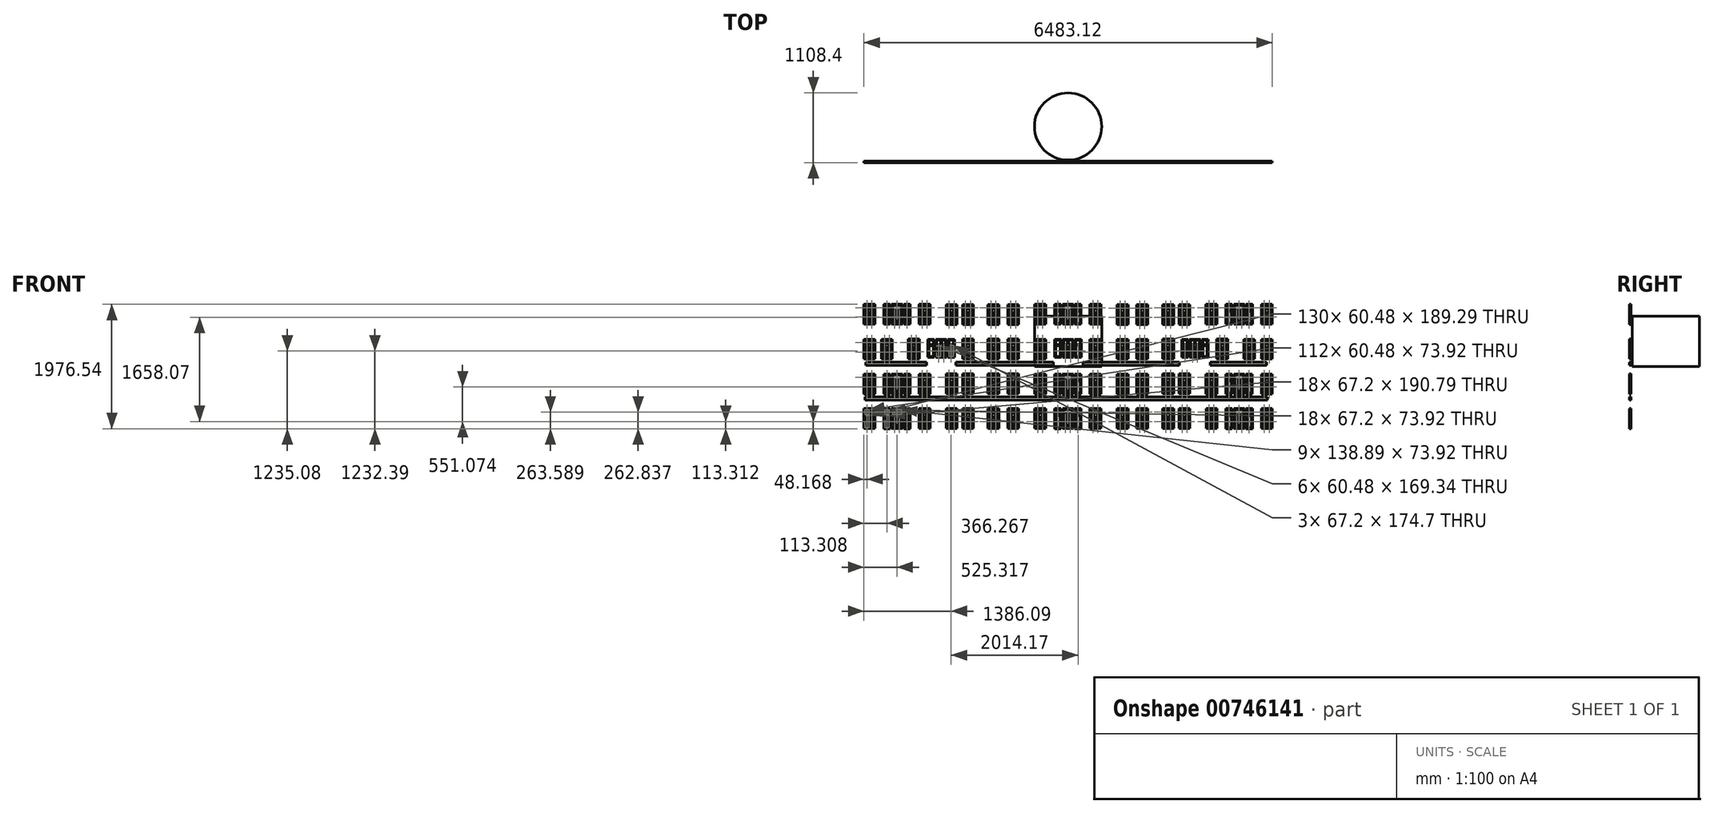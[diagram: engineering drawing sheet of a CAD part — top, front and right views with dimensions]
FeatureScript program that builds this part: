
annotation { "Feature Type Name" : "Feature", "Feature Type Description" : "" }
export const myFeature = defineFeature(function(context is Context, id is Id, definition is map)
    precondition{}
    {
        {
            var Q0;
            Q0=qCreatedBy(makeId("Top.planeOp"),FACE);
            var sketch = newSketch(context, id + "F0", { "sketchPlane" : qUnion([Q0])});
            skCircle(sketch, "E0", {"center": v(0, 0) * mm, "radius": 533.4 * mm});
            skSolve(sketch);
        }
        {
            var Q0;
            Q0 = qSketchRegion(id + "F0", true);
            extrude(context, id + "F1", {"entities" : qUnion([Q0]), "depth" : 800 * mm, "offsetDistance" : 25.4 * mm});
        }
        {
            var Q0;
            Q0=qCreatedBy(makeId("Front.planeOp"),FACE);
            cPlane(context, id + "F2", {"entities" : qUnion([Q0]), "cplaneType" : CPlaneType.OFFSET, "offset" : 50 * mm, "width" : 150 * mm, "height" : 150 * mm});
        }
        {
            var Q0;
            Q0=qCreatedBy(id+"F2.planeOp",FACE);
            cPlane(context, id + "F3", {"entities" : qUnion([Q0]), "cplaneType" : CPlaneType.OFFSET, "offset" : 500 * mm, "width" : 150 * mm, "height" : 150 * mm});
        }
        {
            var Q0;
            Q0=qCreatedBy(id+"F3.planeOp",FACE);
            var sketch = newSketch(context, id + "F4", { "sketchPlane" : qUnion([Q0])});
            skLineSegment(sketch, "E1", {"start": v(777, -987.53) * mm, "end": v(951.73, -987.53) * mm});
            skLineSegment(sketch, "E2", {"start": v(951.73, -987.53) * mm, "end": v(951.73, -670.55) * mm});
            skLineSegment(sketch, "E3", {"start": v(951.73, -670.55) * mm, "end": v(777, -670.55) * mm});
            skLineSegment(sketch, "E4", {"start": v(777, -670.55) * mm, "end": v(777, -987.53) * mm});
            skLineSegment(sketch, "E5", {"start": v(794.92, -780.32) * mm, "end": v(855.4, -780.32) * mm});
            skLineSegment(sketch, "E6", {"start": v(855.4, -780.32) * mm, "end": v(855.4, -969.6) * mm});
            skLineSegment(sketch, "E7", {"start": v(855.4, -969.6) * mm, "end": v(794.92, -969.6) * mm});
            skLineSegment(sketch, "E8", {"start": v(794.92, -969.6) * mm, "end": v(794.92, -780.32) * mm});
            skLineSegment(sketch, "E9", {"start": v(873.33, -969.6) * mm, "end": v(873.33, -780.32) * mm});
            skLineSegment(sketch, "E10", {"start": v(873.33, -780.32) * mm, "end": v(933.8, -780.32) * mm});
            skLineSegment(sketch, "E11", {"start": v(933.8, -780.32) * mm, "end": v(933.8, -969.6) * mm});
            skLineSegment(sketch, "E12", {"start": v(933.8, -969.6) * mm, "end": v(873.33, -969.6) * mm});
            skLineSegment(sketch, "E13", {"start": v(933.8, -762.4) * mm, "end": v(873.33, -762.4) * mm});
            skLineSegment(sketch, "E14", {"start": v(873.33, -762.4) * mm, "end": v(873.33, -688.47) * mm});
            skLineSegment(sketch, "E15", {"start": v(873.33, -688.47) * mm, "end": v(933.8, -688.47) * mm});
            skLineSegment(sketch, "E16", {"start": v(933.8, -688.47) * mm, "end": v(933.8, -762.4) * mm});
            skLineSegment(sketch, "E17", {"start": v(855.4, -688.47) * mm, "end": v(855.4, -762.4) * mm});
            skLineSegment(sketch, "E18", {"start": v(855.4, -762.4) * mm, "end": v(794.92, -762.4) * mm});
            skLineSegment(sketch, "E19", {"start": v(794.92, -762.4) * mm, "end": v(794.92, -688.47) * mm});
            skLineSegment(sketch, "E20", {"start": v(794.92, -688.47) * mm, "end": v(855.4, -688.47) * mm});
            skLineSegment(sketch, "E21", {"start": v(1090.62, -987.53) * mm, "end": v(1265.35, -987.53) * mm});
            skLineSegment(sketch, "E22", {"start": v(1265.35, -987.53) * mm, "end": v(1265.35, -670.55) * mm});
            skLineSegment(sketch, "E23", {"start": v(1265.35, -670.55) * mm, "end": v(1090.62, -670.55) * mm});
            skLineSegment(sketch, "E24", {"start": v(1090.62, -670.55) * mm, "end": v(1090.62, -987.53) * mm});
            skLineSegment(sketch, "E25", {"start": v(1108.54, -780.32) * mm, "end": v(1169.02, -780.32) * mm});
            skLineSegment(sketch, "E26", {"start": v(1169.02, -780.32) * mm, "end": v(1169.02, -969.6) * mm});
            skLineSegment(sketch, "E27", {"start": v(1169.02, -969.6) * mm, "end": v(1108.54, -969.6) * mm});
            skLineSegment(sketch, "E28", {"start": v(1108.54, -969.6) * mm, "end": v(1108.54, -780.32) * mm});
            skLineSegment(sketch, "E29", {"start": v(1186.95, -969.6) * mm, "end": v(1186.95, -780.32) * mm});
            skLineSegment(sketch, "E30", {"start": v(1186.95, -780.32) * mm, "end": v(1247.43, -780.32) * mm});
            skLineSegment(sketch, "E31", {"start": v(1247.43, -780.32) * mm, "end": v(1247.43, -969.6) * mm});
            skLineSegment(sketch, "E32", {"start": v(1247.43, -969.6) * mm, "end": v(1186.95, -969.6) * mm});
            skLineSegment(sketch, "E33", {"start": v(1247.43, -762.4) * mm, "end": v(1186.95, -762.4) * mm});
            skLineSegment(sketch, "E34", {"start": v(1186.95, -762.4) * mm, "end": v(1186.95, -688.47) * mm});
            skLineSegment(sketch, "E35", {"start": v(1186.95, -688.47) * mm, "end": v(1247.43, -688.47) * mm});
            skLineSegment(sketch, "E36", {"start": v(1247.43, -688.47) * mm, "end": v(1247.43, -762.4) * mm});
            skLineSegment(sketch, "E37", {"start": v(1169.02, -688.47) * mm, "end": v(1169.02, -762.4) * mm});
            skLineSegment(sketch, "E38", {"start": v(1169.02, -762.4) * mm, "end": v(1108.54, -762.4) * mm});
            skLineSegment(sketch, "E39", {"start": v(1108.54, -762.4) * mm, "end": v(1108.54, -688.47) * mm});
            skLineSegment(sketch, "E40", {"start": v(1108.54, -688.47) * mm, "end": v(1169.02, -688.47) * mm});
            skLineSegment(sketch, "E41", {"start": v(951.73, -436.46) * mm, "end": v(951.73, -119.48) * mm});
            skLineSegment(sketch, "E42", {"start": v(951.73, -119.48) * mm, "end": v(777, -119.48) * mm});
            skLineSegment(sketch, "E43", {"start": v(777, -119.48) * mm, "end": v(777, -436.46) * mm});
            skLineSegment(sketch, "E44", {"start": v(777, -436.46) * mm, "end": v(951.73, -436.46) * mm});
            skLineSegment(sketch, "E45", {"start": v(794.92, -229.24) * mm, "end": v(855.4, -229.24) * mm});
            skLineSegment(sketch, "E46", {"start": v(855.4, -229.24) * mm, "end": v(855.4, -418.53) * mm});
            skLineSegment(sketch, "E47", {"start": v(855.4, -418.53) * mm, "end": v(794.92, -418.53) * mm});
            skLineSegment(sketch, "E48", {"start": v(794.92, -418.53) * mm, "end": v(794.92, -229.24) * mm});
            skLineSegment(sketch, "E49", {"start": v(873.33, -418.53) * mm, "end": v(873.33, -229.24) * mm});
            skLineSegment(sketch, "E50", {"start": v(873.33, -229.24) * mm, "end": v(933.8, -229.24) * mm});
            skLineSegment(sketch, "E51", {"start": v(933.8, -229.24) * mm, "end": v(933.8, -418.53) * mm});
            skLineSegment(sketch, "E52", {"start": v(933.8, -418.53) * mm, "end": v(873.33, -418.53) * mm});
            skLineSegment(sketch, "E53", {"start": v(933.8, -211.32) * mm, "end": v(873.33, -211.32) * mm});
            skLineSegment(sketch, "E54", {"start": v(873.33, -211.32) * mm, "end": v(873.33, -137.4) * mm});
            skLineSegment(sketch, "E55", {"start": v(873.33, -137.4) * mm, "end": v(933.8, -137.4) * mm});
            skLineSegment(sketch, "E56", {"start": v(933.8, -137.4) * mm, "end": v(933.8, -211.32) * mm});
            skLineSegment(sketch, "E57", {"start": v(855.4, -137.4) * mm, "end": v(855.4, -211.32) * mm});
            skLineSegment(sketch, "E58", {"start": v(855.4, -211.32) * mm, "end": v(794.92, -211.32) * mm});
            skLineSegment(sketch, "E59", {"start": v(794.92, -211.32) * mm, "end": v(794.92, -137.4) * mm});
            skLineSegment(sketch, "E60", {"start": v(794.92, -137.4) * mm, "end": v(855.4, -137.4) * mm});
            skLineSegment(sketch, "E61", {"start": v(1265.35, -436.46) * mm, "end": v(1265.35, -119.48) * mm});
            skLineSegment(sketch, "E62", {"start": v(1265.35, -119.48) * mm, "end": v(1090.62, -119.48) * mm});
            skLineSegment(sketch, "E63", {"start": v(1090.62, -119.48) * mm, "end": v(1090.62, -436.46) * mm});
            skLineSegment(sketch, "E64", {"start": v(1090.62, -436.46) * mm, "end": v(1265.35, -436.46) * mm});
            skLineSegment(sketch, "E65", {"start": v(1108.54, -229.24) * mm, "end": v(1169.02, -229.24) * mm});
            skLineSegment(sketch, "E66", {"start": v(1169.02, -229.24) * mm, "end": v(1169.02, -418.53) * mm});
            skLineSegment(sketch, "E67", {"start": v(1169.02, -418.53) * mm, "end": v(1108.54, -418.53) * mm});
            skLineSegment(sketch, "E68", {"start": v(1108.54, -418.53) * mm, "end": v(1108.54, -229.24) * mm});
            skLineSegment(sketch, "E69", {"start": v(1186.95, -418.53) * mm, "end": v(1186.95, -229.24) * mm});
            skLineSegment(sketch, "E70", {"start": v(1186.95, -229.24) * mm, "end": v(1247.43, -229.24) * mm});
            skLineSegment(sketch, "E71", {"start": v(1247.43, -229.24) * mm, "end": v(1247.43, -418.53) * mm});
            skLineSegment(sketch, "E72", {"start": v(1247.43, -418.53) * mm, "end": v(1186.95, -418.53) * mm});
            skLineSegment(sketch, "E73", {"start": v(1247.43, -211.32) * mm, "end": v(1186.95, -211.32) * mm});
            skLineSegment(sketch, "E74", {"start": v(1186.95, -211.32) * mm, "end": v(1186.95, -137.4) * mm});
            skLineSegment(sketch, "E75", {"start": v(1186.95, -137.4) * mm, "end": v(1247.43, -137.4) * mm});
            skLineSegment(sketch, "E76", {"start": v(1247.43, -137.4) * mm, "end": v(1247.43, -211.32) * mm});
            skLineSegment(sketch, "E77", {"start": v(1169.02, -137.4) * mm, "end": v(1169.02, -211.32) * mm});
            skLineSegment(sketch, "E78", {"start": v(1169.02, -211.32) * mm, "end": v(1108.54, -211.32) * mm});
            skLineSegment(sketch, "E79", {"start": v(1108.54, -211.32) * mm, "end": v(1108.54, -137.4) * mm});
            skLineSegment(sketch, "E80", {"start": v(1108.54, -137.4) * mm, "end": v(1169.02, -137.4) * mm});
            skLineSegment(sketch, "E81", {"start": v(951.73, 433.84) * mm, "end": v(777, 433.84) * mm});
            skLineSegment(sketch, "E82", {"start": v(777, 433.84) * mm, "end": v(777, 116.86) * mm});
            skLineSegment(sketch, "E83", {"start": v(777, 116.86) * mm, "end": v(951.73, 116.86) * mm});
            skLineSegment(sketch, "E84", {"start": v(951.73, 116.86) * mm, "end": v(951.73, 433.84) * mm});
            skLineSegment(sketch, "E85", {"start": v(933.8, 342) * mm, "end": v(873.33, 342) * mm});
            skLineSegment(sketch, "E86", {"start": v(873.33, 342) * mm, "end": v(873.33, 415.92) * mm});
            skLineSegment(sketch, "E87", {"start": v(873.33, 415.92) * mm, "end": v(933.8, 415.92) * mm});
            skLineSegment(sketch, "E88", {"start": v(933.8, 415.92) * mm, "end": v(933.8, 342) * mm});
            skLineSegment(sketch, "E89", {"start": v(855.4, 415.92) * mm, "end": v(855.4, 342) * mm});
            skLineSegment(sketch, "E90", {"start": v(855.4, 342) * mm, "end": v(794.92, 342) * mm});
            skLineSegment(sketch, "E91", {"start": v(794.92, 342) * mm, "end": v(794.92, 415.92) * mm});
            skLineSegment(sketch, "E92", {"start": v(794.92, 415.92) * mm, "end": v(855.4, 415.92) * mm});
            skLineSegment(sketch, "E93", {"start": v(794.92, 324.07) * mm, "end": v(855.4, 324.07) * mm});
            skLineSegment(sketch, "E94", {"start": v(855.4, 324.07) * mm, "end": v(855.4, 134.78) * mm});
            skLineSegment(sketch, "E95", {"start": v(855.4, 134.78) * mm, "end": v(794.92, 134.78) * mm});
            skLineSegment(sketch, "E96", {"start": v(794.92, 134.78) * mm, "end": v(794.92, 324.07) * mm});
            skLineSegment(sketch, "E97", {"start": v(873.33, 134.78) * mm, "end": v(873.33, 324.07) * mm});
            skLineSegment(sketch, "E98", {"start": v(873.33, 324.07) * mm, "end": v(933.8, 324.07) * mm});
            skLineSegment(sketch, "E99", {"start": v(933.8, 324.07) * mm, "end": v(933.8, 134.78) * mm});
            skLineSegment(sketch, "E100", {"start": v(933.8, 134.78) * mm, "end": v(873.33, 134.78) * mm});
            skLineSegment(sketch, "E101", {"start": v(522.74, 433.84) * mm, "end": v(348.01, 433.84) * mm});
            skLineSegment(sketch, "E102", {"start": v(348.01, 433.84) * mm, "end": v(348.01, 116.86) * mm});
            skLineSegment(sketch, "E103", {"start": v(348.01, 116.86) * mm, "end": v(522.74, 116.86) * mm});
            skLineSegment(sketch, "E104", {"start": v(522.74, 116.86) * mm, "end": v(522.74, 433.84) * mm});
            skLineSegment(sketch, "E105", {"start": v(504.82, 342) * mm, "end": v(444.34, 342) * mm});
            skLineSegment(sketch, "E106", {"start": v(444.34, 342) * mm, "end": v(444.34, 415.92) * mm});
            skLineSegment(sketch, "E107", {"start": v(444.34, 415.92) * mm, "end": v(504.82, 415.92) * mm});
            skLineSegment(sketch, "E108", {"start": v(504.82, 415.92) * mm, "end": v(504.82, 342) * mm});
            skLineSegment(sketch, "E109", {"start": v(426.42, 415.92) * mm, "end": v(426.42, 342) * mm});
            skLineSegment(sketch, "E110", {"start": v(426.42, 342) * mm, "end": v(365.93, 342) * mm});
            skLineSegment(sketch, "E111", {"start": v(365.93, 342) * mm, "end": v(365.93, 415.92) * mm});
            skLineSegment(sketch, "E112", {"start": v(365.93, 415.92) * mm, "end": v(426.42, 415.92) * mm});
            skLineSegment(sketch, "E113", {"start": v(365.93, 324.07) * mm, "end": v(426.42, 324.07) * mm});
            skLineSegment(sketch, "E114", {"start": v(426.42, 324.07) * mm, "end": v(426.42, 134.78) * mm});
            skLineSegment(sketch, "E115", {"start": v(426.42, 134.78) * mm, "end": v(365.93, 134.78) * mm});
            skLineSegment(sketch, "E116", {"start": v(365.93, 134.78) * mm, "end": v(365.93, 324.07) * mm});
            skLineSegment(sketch, "E117", {"start": v(444.34, 134.78) * mm, "end": v(444.34, 324.07) * mm});
            skLineSegment(sketch, "E118", {"start": v(444.34, 324.07) * mm, "end": v(504.82, 324.07) * mm});
            skLineSegment(sketch, "E119", {"start": v(504.82, 324.07) * mm, "end": v(504.82, 134.78) * mm});
            skLineSegment(sketch, "E120", {"start": v(504.82, 134.78) * mm, "end": v(444.34, 134.78) * mm});
            skLineSegment(sketch, "E121", {"start": v(522.74, 988.27) * mm, "end": v(348.01, 988.27) * mm});
            skLineSegment(sketch, "E122", {"start": v(348.01, 988.27) * mm, "end": v(348.01, 671.3) * mm});
            skLineSegment(sketch, "E123", {"start": v(348.01, 671.3) * mm, "end": v(522.74, 671.3) * mm});
            skLineSegment(sketch, "E124", {"start": v(522.74, 671.3) * mm, "end": v(522.74, 988.27) * mm});
            skLineSegment(sketch, "E125", {"start": v(504.82, 896.43) * mm, "end": v(444.34, 896.43) * mm});
            skLineSegment(sketch, "E126", {"start": v(444.34, 896.43) * mm, "end": v(444.34, 970.35) * mm});
            skLineSegment(sketch, "E127", {"start": v(444.34, 970.35) * mm, "end": v(504.82, 970.35) * mm});
            skLineSegment(sketch, "E128", {"start": v(504.82, 970.35) * mm, "end": v(504.82, 896.43) * mm});
            skLineSegment(sketch, "E129", {"start": v(426.42, 970.35) * mm, "end": v(426.42, 896.43) * mm});
            skLineSegment(sketch, "E130", {"start": v(426.42, 896.43) * mm, "end": v(365.93, 896.43) * mm});
            skLineSegment(sketch, "E131", {"start": v(365.93, 896.43) * mm, "end": v(365.93, 970.35) * mm});
            skLineSegment(sketch, "E132", {"start": v(365.93, 970.35) * mm, "end": v(426.42, 970.35) * mm});
            skLineSegment(sketch, "E133", {"start": v(365.93, 878.5) * mm, "end": v(426.42, 878.5) * mm});
            skLineSegment(sketch, "E134", {"start": v(426.42, 878.5) * mm, "end": v(426.42, 689.21) * mm});
            skLineSegment(sketch, "E135", {"start": v(426.42, 689.21) * mm, "end": v(365.93, 689.21) * mm});
            skLineSegment(sketch, "E136", {"start": v(365.93, 689.21) * mm, "end": v(365.93, 878.5) * mm});
            skLineSegment(sketch, "E137", {"start": v(444.34, 689.21) * mm, "end": v(444.34, 878.5) * mm});
            skLineSegment(sketch, "E138", {"start": v(444.34, 878.5) * mm, "end": v(504.82, 878.5) * mm});
            skLineSegment(sketch, "E139", {"start": v(504.82, 878.5) * mm, "end": v(504.82, 689.21) * mm});
            skLineSegment(sketch, "E140", {"start": v(504.82, 689.21) * mm, "end": v(444.34, 689.21) * mm});
            skLineSegment(sketch, "E141", {"start": v(-355.39, 433.84) * mm, "end": v(-530.12, 433.84) * mm});
            skLineSegment(sketch, "E142", {"start": v(-530.12, 433.84) * mm, "end": v(-530.12, 116.86) * mm});
            skLineSegment(sketch, "E143", {"start": v(-530.12, 116.86) * mm, "end": v(-355.39, 116.86) * mm});
            skLineSegment(sketch, "E144", {"start": v(-355.39, 116.86) * mm, "end": v(-355.39, 433.84) * mm});
            skLineSegment(sketch, "E145", {"start": v(-373.3, 342) * mm, "end": v(-433.8, 342) * mm});
            skLineSegment(sketch, "E146", {"start": v(-433.8, 342) * mm, "end": v(-433.8, 415.92) * mm});
            skLineSegment(sketch, "E147", {"start": v(-433.8, 415.92) * mm, "end": v(-373.3, 415.92) * mm});
            skLineSegment(sketch, "E148", {"start": v(-373.3, 415.92) * mm, "end": v(-373.3, 342) * mm});
            skLineSegment(sketch, "E149", {"start": v(-451.71, 415.92) * mm, "end": v(-451.71, 342) * mm});
            skLineSegment(sketch, "E150", {"start": v(-451.71, 342) * mm, "end": v(-512.2, 342) * mm});
            skLineSegment(sketch, "E151", {"start": v(-512.2, 342) * mm, "end": v(-512.2, 415.92) * mm});
            skLineSegment(sketch, "E152", {"start": v(-512.2, 415.92) * mm, "end": v(-451.71, 415.92) * mm});
            skLineSegment(sketch, "E153", {"start": v(-512.2, 324.07) * mm, "end": v(-451.71, 324.07) * mm});
            skLineSegment(sketch, "E154", {"start": v(-451.71, 324.07) * mm, "end": v(-451.71, 134.78) * mm});
            skLineSegment(sketch, "E155", {"start": v(-451.71, 134.78) * mm, "end": v(-512.2, 134.78) * mm});
            skLineSegment(sketch, "E156", {"start": v(-512.2, 134.78) * mm, "end": v(-512.2, 324.07) * mm});
            skLineSegment(sketch, "E157", {"start": v(-433.8, 134.78) * mm, "end": v(-433.8, 324.07) * mm});
            skLineSegment(sketch, "E158", {"start": v(-433.8, 324.07) * mm, "end": v(-373.3, 324.07) * mm});
            skLineSegment(sketch, "E159", {"start": v(-373.3, 324.07) * mm, "end": v(-373.3, 134.78) * mm});
            skLineSegment(sketch, "E160", {"start": v(-373.3, 134.78) * mm, "end": v(-433.8, 134.78) * mm});
            skLineSegment(sketch, "E161", {"start": v(-355.39, -436.46) * mm, "end": v(-355.39, -119.48) * mm});
            skLineSegment(sketch, "E162", {"start": v(-355.39, -119.48) * mm, "end": v(-530.12, -119.48) * mm});
            skLineSegment(sketch, "E163", {"start": v(-530.12, -119.48) * mm, "end": v(-530.12, -436.46) * mm});
            skLineSegment(sketch, "E164", {"start": v(-530.12, -436.46) * mm, "end": v(-355.39, -436.46) * mm});
            skLineSegment(sketch, "E165", {"start": v(-512.2, -229.24) * mm, "end": v(-451.71, -229.24) * mm});
            skLineSegment(sketch, "E166", {"start": v(-451.71, -229.24) * mm, "end": v(-451.71, -418.53) * mm});
            skLineSegment(sketch, "E167", {"start": v(-451.71, -418.53) * mm, "end": v(-512.2, -418.53) * mm});
            skLineSegment(sketch, "E168", {"start": v(-512.2, -418.53) * mm, "end": v(-512.2, -229.24) * mm});
            skLineSegment(sketch, "E169", {"start": v(-433.8, -418.53) * mm, "end": v(-433.8, -229.24) * mm});
            skLineSegment(sketch, "E170", {"start": v(-433.8, -229.24) * mm, "end": v(-373.3, -229.24) * mm});
            skLineSegment(sketch, "E171", {"start": v(-373.3, -229.24) * mm, "end": v(-373.3, -418.53) * mm});
            skLineSegment(sketch, "E172", {"start": v(-373.3, -418.53) * mm, "end": v(-433.8, -418.53) * mm});
            skLineSegment(sketch, "E173", {"start": v(-373.3, -211.32) * mm, "end": v(-433.8, -211.32) * mm});
            skLineSegment(sketch, "E174", {"start": v(-433.8, -211.32) * mm, "end": v(-433.8, -137.4) * mm});
            skLineSegment(sketch, "E175", {"start": v(-433.8, -137.4) * mm, "end": v(-373.3, -137.4) * mm});
            skLineSegment(sketch, "E176", {"start": v(-373.3, -137.4) * mm, "end": v(-373.3, -211.32) * mm});
            skLineSegment(sketch, "E177", {"start": v(-451.71, -137.4) * mm, "end": v(-451.71, -211.32) * mm});
            skLineSegment(sketch, "E178", {"start": v(-451.71, -211.32) * mm, "end": v(-512.2, -211.32) * mm});
            skLineSegment(sketch, "E179", {"start": v(-512.2, -211.32) * mm, "end": v(-512.2, -137.4) * mm});
            skLineSegment(sketch, "E180", {"start": v(-512.2, -137.4) * mm, "end": v(-451.71, -137.4) * mm});
            skLineSegment(sketch, "E181", {"start": v(-355.39, 988.27) * mm, "end": v(-530.12, 988.27) * mm});
            skLineSegment(sketch, "E182", {"start": v(-530.12, 988.27) * mm, "end": v(-530.12, 671.3) * mm});
            skLineSegment(sketch, "E183", {"start": v(-530.12, 671.3) * mm, "end": v(-355.39, 671.3) * mm});
            skLineSegment(sketch, "E184", {"start": v(-355.39, 671.3) * mm, "end": v(-355.39, 988.27) * mm});
            skLineSegment(sketch, "E185", {"start": v(-373.3, 896.43) * mm, "end": v(-433.8, 896.43) * mm});
            skLineSegment(sketch, "E186", {"start": v(-433.8, 896.43) * mm, "end": v(-433.8, 970.35) * mm});
            skLineSegment(sketch, "E187", {"start": v(-433.8, 970.35) * mm, "end": v(-373.3, 970.35) * mm});
            skLineSegment(sketch, "E188", {"start": v(-373.3, 970.35) * mm, "end": v(-373.3, 896.43) * mm});
            skLineSegment(sketch, "E189", {"start": v(-451.71, 970.35) * mm, "end": v(-451.71, 896.43) * mm});
            skLineSegment(sketch, "E190", {"start": v(-451.71, 896.43) * mm, "end": v(-512.2, 896.43) * mm});
            skLineSegment(sketch, "E191", {"start": v(-512.2, 896.43) * mm, "end": v(-512.2, 970.35) * mm});
            skLineSegment(sketch, "E192", {"start": v(-512.2, 970.35) * mm, "end": v(-451.71, 970.35) * mm});
            skLineSegment(sketch, "E193", {"start": v(-512.2, 878.5) * mm, "end": v(-451.71, 878.5) * mm});
            skLineSegment(sketch, "E194", {"start": v(-451.71, 878.5) * mm, "end": v(-451.71, 689.21) * mm});
            skLineSegment(sketch, "E195", {"start": v(-451.71, 689.21) * mm, "end": v(-512.2, 689.21) * mm});
            skLineSegment(sketch, "E196", {"start": v(-512.2, 689.21) * mm, "end": v(-512.2, 878.5) * mm});
            skLineSegment(sketch, "E197", {"start": v(-433.8, 689.21) * mm, "end": v(-433.8, 878.5) * mm});
            skLineSegment(sketch, "E198", {"start": v(-433.8, 878.5) * mm, "end": v(-373.3, 878.5) * mm});
            skLineSegment(sketch, "E199", {"start": v(-373.3, 878.5) * mm, "end": v(-373.3, 689.21) * mm});
            skLineSegment(sketch, "E200", {"start": v(-373.3, 689.21) * mm, "end": v(-433.8, 689.21) * mm});
            skLineSegment(sketch, "E201", {"start": v(84.8, 988.27) * mm, "end": v(-89.93, 988.27) * mm});
            skLineSegment(sketch, "E202", {"start": v(-89.93, 988.27) * mm, "end": v(-89.93, 671.3) * mm});
            skLineSegment(sketch, "E203", {"start": v(-89.93, 671.3) * mm, "end": v(84.8, 671.3) * mm});
            skLineSegment(sketch, "E204", {"start": v(84.8, 671.3) * mm, "end": v(84.8, 988.27) * mm});
            skLineSegment(sketch, "E205", {"start": v(66.88, 970.35) * mm, "end": v(66.88, 896.43) * mm});
            skLineSegment(sketch, "E206", {"start": v(66.88, 896.43) * mm, "end": v(-72, 896.43) * mm});
            skLineSegment(sketch, "E207", {"start": v(-72, 896.43) * mm, "end": v(-72, 970.35) * mm});
            skLineSegment(sketch, "E208", {"start": v(-72, 970.35) * mm, "end": v(66.88, 970.35) * mm});
            skLineSegment(sketch, "E209", {"start": v(-72, 878.5) * mm, "end": v(-11.52, 878.5) * mm});
            skLineSegment(sketch, "E210", {"start": v(-11.52, 878.5) * mm, "end": v(-11.52, 689.21) * mm});
            skLineSegment(sketch, "E211", {"start": v(-11.52, 689.21) * mm, "end": v(-72, 689.21) * mm});
            skLineSegment(sketch, "E212", {"start": v(-72, 689.21) * mm, "end": v(-72, 878.5) * mm});
            skLineSegment(sketch, "E213", {"start": v(6.4, 689.21) * mm, "end": v(6.4, 878.5) * mm});
            skLineSegment(sketch, "E214", {"start": v(6.4, 878.5) * mm, "end": v(66.88, 878.5) * mm});
            skLineSegment(sketch, "E215", {"start": v(66.88, 878.5) * mm, "end": v(66.88, 689.21) * mm});
            skLineSegment(sketch, "E216", {"start": v(66.88, 689.21) * mm, "end": v(6.4, 689.21) * mm});
            skLineSegment(sketch, "E217", {"start": v(522.74, -436.46) * mm, "end": v(522.74, -119.48) * mm});
            skLineSegment(sketch, "E218", {"start": v(522.74, -119.48) * mm, "end": v(348.01, -119.48) * mm});
            skLineSegment(sketch, "E219", {"start": v(348.01, -119.48) * mm, "end": v(348.01, -436.46) * mm});
            skLineSegment(sketch, "E220", {"start": v(348.01, -436.46) * mm, "end": v(522.74, -436.46) * mm});
            skLineSegment(sketch, "E221", {"start": v(365.93, -229.24) * mm, "end": v(426.42, -229.24) * mm});
            skLineSegment(sketch, "E222", {"start": v(426.42, -229.24) * mm, "end": v(426.42, -418.53) * mm});
            skLineSegment(sketch, "E223", {"start": v(426.42, -418.53) * mm, "end": v(365.93, -418.53) * mm});
            skLineSegment(sketch, "E224", {"start": v(365.93, -418.53) * mm, "end": v(365.93, -229.24) * mm});
            skLineSegment(sketch, "E225", {"start": v(444.34, -418.53) * mm, "end": v(444.34, -229.24) * mm});
            skLineSegment(sketch, "E226", {"start": v(444.34, -229.24) * mm, "end": v(504.82, -229.24) * mm});
            skLineSegment(sketch, "E227", {"start": v(504.82, -229.24) * mm, "end": v(504.82, -418.53) * mm});
            skLineSegment(sketch, "E228", {"start": v(504.82, -418.53) * mm, "end": v(444.34, -418.53) * mm});
            skLineSegment(sketch, "E229", {"start": v(504.82, -211.32) * mm, "end": v(444.34, -211.32) * mm});
            skLineSegment(sketch, "E230", {"start": v(444.34, -211.32) * mm, "end": v(444.34, -137.4) * mm});
            skLineSegment(sketch, "E231", {"start": v(444.34, -137.4) * mm, "end": v(504.82, -137.4) * mm});
            skLineSegment(sketch, "E232", {"start": v(504.82, -137.4) * mm, "end": v(504.82, -211.32) * mm});
            skLineSegment(sketch, "E233", {"start": v(426.42, -137.4) * mm, "end": v(426.42, -211.32) * mm});
            skLineSegment(sketch, "E234", {"start": v(426.42, -211.32) * mm, "end": v(365.93, -211.32) * mm});
            skLineSegment(sketch, "E235", {"start": v(365.93, -211.32) * mm, "end": v(365.93, -137.4) * mm});
            skLineSegment(sketch, "E236", {"start": v(365.93, -137.4) * mm, "end": v(426.42, -137.4) * mm});
            skLineSegment(sketch, "E237", {"start": v(1265.35, 433.84) * mm, "end": v(1090.62, 433.84) * mm});
            skLineSegment(sketch, "E238", {"start": v(1090.62, 433.84) * mm, "end": v(1090.62, 116.86) * mm});
            skLineSegment(sketch, "E239", {"start": v(1090.62, 116.86) * mm, "end": v(1265.35, 116.86) * mm});
            skLineSegment(sketch, "E240", {"start": v(1265.35, 116.86) * mm, "end": v(1265.35, 433.84) * mm});
            skLineSegment(sketch, "E241", {"start": v(1247.43, 342) * mm, "end": v(1186.95, 342) * mm});
            skLineSegment(sketch, "E242", {"start": v(1186.95, 342) * mm, "end": v(1186.95, 415.92) * mm});
            skLineSegment(sketch, "E243", {"start": v(1186.95, 415.92) * mm, "end": v(1247.43, 415.92) * mm});
            skLineSegment(sketch, "E244", {"start": v(1247.43, 415.92) * mm, "end": v(1247.43, 342) * mm});
            skLineSegment(sketch, "E245", {"start": v(1169.02, 415.92) * mm, "end": v(1169.02, 342) * mm});
            skLineSegment(sketch, "E246", {"start": v(1169.02, 342) * mm, "end": v(1108.54, 342) * mm});
            skLineSegment(sketch, "E247", {"start": v(1108.54, 342) * mm, "end": v(1108.54, 415.92) * mm});
            skLineSegment(sketch, "E248", {"start": v(1108.54, 415.92) * mm, "end": v(1169.02, 415.92) * mm});
            skLineSegment(sketch, "E249", {"start": v(1108.54, 324.07) * mm, "end": v(1169.02, 324.07) * mm});
            skLineSegment(sketch, "E250", {"start": v(1169.02, 324.07) * mm, "end": v(1169.02, 134.78) * mm});
            skLineSegment(sketch, "E251", {"start": v(1169.02, 134.78) * mm, "end": v(1108.54, 134.78) * mm});
            skLineSegment(sketch, "E252", {"start": v(1108.54, 134.78) * mm, "end": v(1108.54, 324.07) * mm});
            skLineSegment(sketch, "E253", {"start": v(1186.95, 134.78) * mm, "end": v(1186.95, 324.07) * mm});
            skLineSegment(sketch, "E254", {"start": v(1186.95, 324.07) * mm, "end": v(1247.43, 324.07) * mm});
            skLineSegment(sketch, "E255", {"start": v(1247.43, 324.07) * mm, "end": v(1247.43, 134.78) * mm});
            skLineSegment(sketch, "E256", {"start": v(1247.43, 134.78) * mm, "end": v(1186.95, 134.78) * mm});
            skLineSegment(sketch, "E257", {"start": v(951.73, 983.8) * mm, "end": v(777, 983.8) * mm});
            skLineSegment(sketch, "E258", {"start": v(777, 983.8) * mm, "end": v(777, 666.81) * mm});
            skLineSegment(sketch, "E259", {"start": v(777, 666.81) * mm, "end": v(951.73, 666.81) * mm});
            skLineSegment(sketch, "E260", {"start": v(951.73, 666.81) * mm, "end": v(951.73, 983.8) * mm});
            skLineSegment(sketch, "E261", {"start": v(933.8, 891.95) * mm, "end": v(873.33, 891.95) * mm});
            skLineSegment(sketch, "E262", {"start": v(873.33, 891.95) * mm, "end": v(873.33, 965.87) * mm});
            skLineSegment(sketch, "E263", {"start": v(873.33, 965.87) * mm, "end": v(933.8, 965.87) * mm});
            skLineSegment(sketch, "E264", {"start": v(933.8, 965.87) * mm, "end": v(933.8, 891.95) * mm});
            skLineSegment(sketch, "E265", {"start": v(855.4, 965.87) * mm, "end": v(855.4, 891.95) * mm});
            skLineSegment(sketch, "E266", {"start": v(855.4, 891.95) * mm, "end": v(794.92, 891.95) * mm});
            skLineSegment(sketch, "E267", {"start": v(794.92, 891.95) * mm, "end": v(794.92, 965.87) * mm});
            skLineSegment(sketch, "E268", {"start": v(794.92, 965.87) * mm, "end": v(855.4, 965.87) * mm});
            skLineSegment(sketch, "E269", {"start": v(794.92, 874.03) * mm, "end": v(855.4, 874.03) * mm});
            skLineSegment(sketch, "E270", {"start": v(855.4, 874.03) * mm, "end": v(855.4, 684.73) * mm});
            skLineSegment(sketch, "E271", {"start": v(855.4, 684.73) * mm, "end": v(794.92, 684.73) * mm});
            skLineSegment(sketch, "E272", {"start": v(794.92, 684.73) * mm, "end": v(794.92, 874.03) * mm});
            skLineSegment(sketch, "E273", {"start": v(873.33, 684.73) * mm, "end": v(873.33, 874.03) * mm});
            skLineSegment(sketch, "E274", {"start": v(873.33, 874.03) * mm, "end": v(933.8, 874.03) * mm});
            skLineSegment(sketch, "E275", {"start": v(933.8, 874.03) * mm, "end": v(933.8, 684.73) * mm});
            skLineSegment(sketch, "E276", {"start": v(933.8, 684.73) * mm, "end": v(873.33, 684.73) * mm});
            skLineSegment(sketch, "E277", {"start": v(1265.35, 983.8) * mm, "end": v(1090.62, 983.8) * mm});
            skLineSegment(sketch, "E278", {"start": v(1090.62, 983.8) * mm, "end": v(1090.62, 666.81) * mm});
            skLineSegment(sketch, "E279", {"start": v(1090.62, 666.81) * mm, "end": v(1265.35, 666.81) * mm});
            skLineSegment(sketch, "E280", {"start": v(1265.35, 666.81) * mm, "end": v(1265.35, 983.8) * mm});
            skLineSegment(sketch, "E281", {"start": v(1247.43, 891.95) * mm, "end": v(1186.95, 891.95) * mm});
            skLineSegment(sketch, "E282", {"start": v(1186.95, 891.95) * mm, "end": v(1186.95, 965.87) * mm});
            skLineSegment(sketch, "E283", {"start": v(1186.95, 965.87) * mm, "end": v(1247.43, 965.87) * mm});
            skLineSegment(sketch, "E284", {"start": v(1247.43, 965.87) * mm, "end": v(1247.43, 891.95) * mm});
            skLineSegment(sketch, "E285", {"start": v(1169.02, 965.87) * mm, "end": v(1169.02, 891.95) * mm});
            skLineSegment(sketch, "E286", {"start": v(1169.02, 891.95) * mm, "end": v(1108.54, 891.95) * mm});
            skLineSegment(sketch, "E287", {"start": v(1108.54, 891.95) * mm, "end": v(1108.54, 965.87) * mm});
            skLineSegment(sketch, "E288", {"start": v(1108.54, 965.87) * mm, "end": v(1169.02, 965.87) * mm});
            skLineSegment(sketch, "E289", {"start": v(1108.54, 874.03) * mm, "end": v(1169.02, 874.03) * mm});
            skLineSegment(sketch, "E290", {"start": v(1169.02, 874.03) * mm, "end": v(1169.02, 684.73) * mm});
            skLineSegment(sketch, "E291", {"start": v(1169.02, 684.73) * mm, "end": v(1108.54, 684.73) * mm});
            skLineSegment(sketch, "E292", {"start": v(1108.54, 684.73) * mm, "end": v(1108.54, 874.03) * mm});
            skLineSegment(sketch, "E293", {"start": v(1186.95, 684.73) * mm, "end": v(1186.95, 874.03) * mm});
            skLineSegment(sketch, "E294", {"start": v(1186.95, 874.03) * mm, "end": v(1247.43, 874.03) * mm});
            skLineSegment(sketch, "E295", {"start": v(1247.43, 874.03) * mm, "end": v(1247.43, 684.73) * mm});
            skLineSegment(sketch, "E296", {"start": v(1247.43, 684.73) * mm, "end": v(1186.95, 684.73) * mm});
            skLineSegment(sketch, "E297", {"start": v(-1096.87, -434.78) * mm, "end": v(-1096.87, -117.8) * mm});
            skLineSegment(sketch, "E298", {"start": v(-1096.87, -117.8) * mm, "end": v(-1271.6, -117.8) * mm});
            skLineSegment(sketch, "E299", {"start": v(-1271.6, -117.8) * mm, "end": v(-1271.6, -434.78) * mm});
            skLineSegment(sketch, "E300", {"start": v(-1271.6, -434.78) * mm, "end": v(-1096.87, -434.78) * mm});
            skLineSegment(sketch, "E301", {"start": v(-1253.68, -227.56) * mm, "end": v(-1193.2, -227.56) * mm});
            skLineSegment(sketch, "E302", {"start": v(-1193.2, -227.56) * mm, "end": v(-1193.2, -416.85) * mm});
            skLineSegment(sketch, "E303", {"start": v(-1193.2, -416.85) * mm, "end": v(-1253.68, -416.85) * mm});
            skLineSegment(sketch, "E304", {"start": v(-1253.68, -416.85) * mm, "end": v(-1253.68, -227.56) * mm});
            skLineSegment(sketch, "E305", {"start": v(-1175.28, -416.85) * mm, "end": v(-1175.28, -227.56) * mm});
            skLineSegment(sketch, "E306", {"start": v(-1175.28, -227.56) * mm, "end": v(-1114.8, -227.56) * mm});
            skLineSegment(sketch, "E307", {"start": v(-1114.8, -227.56) * mm, "end": v(-1114.8, -416.85) * mm});
            skLineSegment(sketch, "E308", {"start": v(-1114.8, -416.85) * mm, "end": v(-1175.28, -416.85) * mm});
            skLineSegment(sketch, "E309", {"start": v(-1114.8, -209.64) * mm, "end": v(-1175.28, -209.64) * mm});
            skLineSegment(sketch, "E310", {"start": v(-1175.28, -209.64) * mm, "end": v(-1175.28, -135.72) * mm});
            skLineSegment(sketch, "E311", {"start": v(-1175.28, -135.72) * mm, "end": v(-1114.8, -135.72) * mm});
            skLineSegment(sketch, "E312", {"start": v(-1114.8, -135.72) * mm, "end": v(-1114.8, -209.64) * mm});
            skLineSegment(sketch, "E313", {"start": v(-1193.2, -135.72) * mm, "end": v(-1193.2, -209.64) * mm});
            skLineSegment(sketch, "E314", {"start": v(-1193.2, -209.64) * mm, "end": v(-1253.68, -209.64) * mm});
            skLineSegment(sketch, "E315", {"start": v(-1253.68, -209.64) * mm, "end": v(-1253.68, -135.72) * mm});
            skLineSegment(sketch, "E316", {"start": v(-1253.68, -135.72) * mm, "end": v(-1193.2, -135.72) * mm});
            skLineSegment(sketch, "E317", {"start": v(-783.25, -434.78) * mm, "end": v(-783.25, -117.8) * mm});
            skLineSegment(sketch, "E318", {"start": v(-783.25, -117.8) * mm, "end": v(-957.98, -117.8) * mm});
            skLineSegment(sketch, "E319", {"start": v(-957.98, -117.8) * mm, "end": v(-957.98, -434.78) * mm});
            skLineSegment(sketch, "E320", {"start": v(-957.98, -434.78) * mm, "end": v(-783.25, -434.78) * mm});
            skLineSegment(sketch, "E321", {"start": v(-940.06, -227.56) * mm, "end": v(-879.58, -227.56) * mm});
            skLineSegment(sketch, "E322", {"start": v(-879.58, -227.56) * mm, "end": v(-879.58, -416.85) * mm});
            skLineSegment(sketch, "E323", {"start": v(-879.58, -416.85) * mm, "end": v(-940.06, -416.85) * mm});
            skLineSegment(sketch, "E324", {"start": v(-940.06, -416.85) * mm, "end": v(-940.06, -227.56) * mm});
            skLineSegment(sketch, "E325", {"start": v(-861.66, -416.85) * mm, "end": v(-861.66, -227.56) * mm});
            skLineSegment(sketch, "E326", {"start": v(-861.66, -227.56) * mm, "end": v(-801.17, -227.56) * mm});
            skLineSegment(sketch, "E327", {"start": v(-801.17, -227.56) * mm, "end": v(-801.17, -416.85) * mm});
            skLineSegment(sketch, "E328", {"start": v(-801.17, -416.85) * mm, "end": v(-861.66, -416.85) * mm});
            skLineSegment(sketch, "E329", {"start": v(-801.17, -209.64) * mm, "end": v(-861.66, -209.64) * mm});
            skLineSegment(sketch, "E330", {"start": v(-861.66, -209.64) * mm, "end": v(-861.66, -135.72) * mm});
            skLineSegment(sketch, "E331", {"start": v(-861.66, -135.72) * mm, "end": v(-801.17, -135.72) * mm});
            skLineSegment(sketch, "E332", {"start": v(-801.17, -135.72) * mm, "end": v(-801.17, -209.64) * mm});
            skLineSegment(sketch, "E333", {"start": v(-879.58, -135.72) * mm, "end": v(-879.58, -209.64) * mm});
            skLineSegment(sketch, "E334", {"start": v(-879.58, -209.64) * mm, "end": v(-940.06, -209.64) * mm});
            skLineSegment(sketch, "E335", {"start": v(-940.06, -209.64) * mm, "end": v(-940.06, -135.72) * mm});
            skLineSegment(sketch, "E336", {"start": v(-940.06, -135.72) * mm, "end": v(-879.58, -135.72) * mm});
            skLineSegment(sketch, "E337", {"start": v(-1096.87, 435.52) * mm, "end": v(-1271.6, 435.52) * mm});
            skLineSegment(sketch, "E338", {"start": v(-1271.6, 435.52) * mm, "end": v(-1271.6, 118.54) * mm});
            skLineSegment(sketch, "E339", {"start": v(-1271.6, 118.54) * mm, "end": v(-1096.87, 118.54) * mm});
            skLineSegment(sketch, "E340", {"start": v(-1096.87, 118.54) * mm, "end": v(-1096.87, 435.52) * mm});
            skLineSegment(sketch, "E341", {"start": v(-1114.8, 343.67) * mm, "end": v(-1175.28, 343.67) * mm});
            skLineSegment(sketch, "E342", {"start": v(-1175.28, 343.67) * mm, "end": v(-1175.28, 417.6) * mm});
            skLineSegment(sketch, "E343", {"start": v(-1175.28, 417.6) * mm, "end": v(-1114.8, 417.6) * mm});
            skLineSegment(sketch, "E344", {"start": v(-1114.8, 417.6) * mm, "end": v(-1114.8, 343.67) * mm});
            skLineSegment(sketch, "E345", {"start": v(-1193.2, 417.6) * mm, "end": v(-1193.2, 343.67) * mm});
            skLineSegment(sketch, "E346", {"start": v(-1193.2, 343.67) * mm, "end": v(-1253.68, 343.67) * mm});
            skLineSegment(sketch, "E347", {"start": v(-1253.68, 343.67) * mm, "end": v(-1253.68, 417.6) * mm});
            skLineSegment(sketch, "E348", {"start": v(-1253.68, 417.6) * mm, "end": v(-1193.2, 417.6) * mm});
            skLineSegment(sketch, "E349", {"start": v(-1253.68, 325.75) * mm, "end": v(-1193.2, 325.75) * mm});
            skLineSegment(sketch, "E350", {"start": v(-1193.2, 325.75) * mm, "end": v(-1193.2, 136.46) * mm});
            skLineSegment(sketch, "E351", {"start": v(-1193.2, 136.46) * mm, "end": v(-1253.68, 136.46) * mm});
            skLineSegment(sketch, "E352", {"start": v(-1253.68, 136.46) * mm, "end": v(-1253.68, 325.75) * mm});
            skLineSegment(sketch, "E353", {"start": v(-1175.28, 136.46) * mm, "end": v(-1175.28, 325.75) * mm});
            skLineSegment(sketch, "E354", {"start": v(-1175.28, 325.75) * mm, "end": v(-1114.8, 325.75) * mm});
            skLineSegment(sketch, "E355", {"start": v(-1114.8, 325.75) * mm, "end": v(-1114.8, 136.46) * mm});
            skLineSegment(sketch, "E356", {"start": v(-1114.8, 136.46) * mm, "end": v(-1175.28, 136.46) * mm});
            skLineSegment(sketch, "E357", {"start": v(-783.25, 435.52) * mm, "end": v(-957.98, 435.52) * mm});
            skLineSegment(sketch, "E358", {"start": v(-957.98, 435.52) * mm, "end": v(-957.98, 118.54) * mm});
            skLineSegment(sketch, "E359", {"start": v(-957.98, 118.54) * mm, "end": v(-783.25, 118.54) * mm});
            skLineSegment(sketch, "E360", {"start": v(-783.25, 118.54) * mm, "end": v(-783.25, 435.52) * mm});
            skLineSegment(sketch, "E361", {"start": v(-801.17, 343.67) * mm, "end": v(-861.66, 343.67) * mm});
            skLineSegment(sketch, "E362", {"start": v(-861.66, 343.67) * mm, "end": v(-861.66, 417.6) * mm});
            skLineSegment(sketch, "E363", {"start": v(-861.66, 417.6) * mm, "end": v(-801.17, 417.6) * mm});
            skLineSegment(sketch, "E364", {"start": v(-801.17, 417.6) * mm, "end": v(-801.17, 343.67) * mm});
            skLineSegment(sketch, "E365", {"start": v(-879.58, 417.6) * mm, "end": v(-879.58, 343.67) * mm});
            skLineSegment(sketch, "E366", {"start": v(-879.58, 343.67) * mm, "end": v(-940.06, 343.67) * mm});
            skLineSegment(sketch, "E367", {"start": v(-940.06, 343.67) * mm, "end": v(-940.06, 417.6) * mm});
            skLineSegment(sketch, "E368", {"start": v(-940.06, 417.6) * mm, "end": v(-879.58, 417.6) * mm});
            skLineSegment(sketch, "E369", {"start": v(-940.06, 325.75) * mm, "end": v(-879.58, 325.75) * mm});
            skLineSegment(sketch, "E370", {"start": v(-879.58, 325.75) * mm, "end": v(-879.58, 136.46) * mm});
            skLineSegment(sketch, "E371", {"start": v(-879.58, 136.46) * mm, "end": v(-940.06, 136.46) * mm});
            skLineSegment(sketch, "E372", {"start": v(-940.06, 136.46) * mm, "end": v(-940.06, 325.75) * mm});
            skLineSegment(sketch, "E373", {"start": v(-861.66, 136.46) * mm, "end": v(-861.66, 325.75) * mm});
            skLineSegment(sketch, "E374", {"start": v(-861.66, 325.75) * mm, "end": v(-801.17, 325.75) * mm});
            skLineSegment(sketch, "E375", {"start": v(-801.17, 325.75) * mm, "end": v(-801.17, 136.46) * mm});
            skLineSegment(sketch, "E376", {"start": v(-801.17, 136.46) * mm, "end": v(-861.66, 136.46) * mm});
            skLineSegment(sketch, "E377", {"start": v(-1096.87, 985.47) * mm, "end": v(-1271.6, 985.47) * mm});
            skLineSegment(sketch, "E378", {"start": v(-1271.6, 985.47) * mm, "end": v(-1271.6, 668.5) * mm});
            skLineSegment(sketch, "E379", {"start": v(-1271.6, 668.5) * mm, "end": v(-1096.87, 668.5) * mm});
            skLineSegment(sketch, "E380", {"start": v(-1096.87, 668.5) * mm, "end": v(-1096.87, 985.47) * mm});
            skLineSegment(sketch, "E381", {"start": v(-1114.8, 893.63) * mm, "end": v(-1175.28, 893.63) * mm});
            skLineSegment(sketch, "E382", {"start": v(-1175.28, 893.63) * mm, "end": v(-1175.28, 967.55) * mm});
            skLineSegment(sketch, "E383", {"start": v(-1175.28, 967.55) * mm, "end": v(-1114.8, 967.55) * mm});
            skLineSegment(sketch, "E384", {"start": v(-1114.8, 967.55) * mm, "end": v(-1114.8, 893.63) * mm});
            skLineSegment(sketch, "E385", {"start": v(-1193.2, 967.55) * mm, "end": v(-1193.2, 893.63) * mm});
            skLineSegment(sketch, "E386", {"start": v(-1193.2, 893.63) * mm, "end": v(-1253.68, 893.63) * mm});
            skLineSegment(sketch, "E387", {"start": v(-1253.68, 893.63) * mm, "end": v(-1253.68, 967.55) * mm});
            skLineSegment(sketch, "E388", {"start": v(-1253.68, 967.55) * mm, "end": v(-1193.2, 967.55) * mm});
            skLineSegment(sketch, "E389", {"start": v(-1253.68, 875.7) * mm, "end": v(-1193.2, 875.7) * mm});
            skLineSegment(sketch, "E390", {"start": v(-1193.2, 875.7) * mm, "end": v(-1193.2, 686.41) * mm});
            skLineSegment(sketch, "E391", {"start": v(-1193.2, 686.41) * mm, "end": v(-1253.68, 686.41) * mm});
            skLineSegment(sketch, "E392", {"start": v(-1253.68, 686.41) * mm, "end": v(-1253.68, 875.7) * mm});
            skLineSegment(sketch, "E393", {"start": v(-1175.28, 686.41) * mm, "end": v(-1175.28, 875.7) * mm});
            skLineSegment(sketch, "E394", {"start": v(-1175.28, 875.7) * mm, "end": v(-1114.8, 875.7) * mm});
            skLineSegment(sketch, "E395", {"start": v(-1114.8, 875.7) * mm, "end": v(-1114.8, 686.41) * mm});
            skLineSegment(sketch, "E396", {"start": v(-1114.8, 686.41) * mm, "end": v(-1175.28, 686.41) * mm});
            skLineSegment(sketch, "E397", {"start": v(-783.25, 985.47) * mm, "end": v(-957.98, 985.47) * mm});
            skLineSegment(sketch, "E398", {"start": v(-957.98, 985.47) * mm, "end": v(-957.98, 668.5) * mm});
            skLineSegment(sketch, "E399", {"start": v(-957.98, 668.5) * mm, "end": v(-783.25, 668.5) * mm});
            skLineSegment(sketch, "E400", {"start": v(-783.25, 668.5) * mm, "end": v(-783.25, 985.47) * mm});
            skLineSegment(sketch, "E401", {"start": v(-801.17, 893.63) * mm, "end": v(-861.66, 893.63) * mm});
            skLineSegment(sketch, "E402", {"start": v(-861.66, 893.63) * mm, "end": v(-861.66, 967.55) * mm});
            skLineSegment(sketch, "E403", {"start": v(-861.66, 967.55) * mm, "end": v(-801.17, 967.55) * mm});
            skLineSegment(sketch, "E404", {"start": v(-801.17, 967.55) * mm, "end": v(-801.17, 893.63) * mm});
            skLineSegment(sketch, "E405", {"start": v(-879.58, 967.55) * mm, "end": v(-879.58, 893.63) * mm});
            skLineSegment(sketch, "E406", {"start": v(-879.58, 893.63) * mm, "end": v(-940.06, 893.63) * mm});
            skLineSegment(sketch, "E407", {"start": v(-940.06, 893.63) * mm, "end": v(-940.06, 967.55) * mm});
            skLineSegment(sketch, "E408", {"start": v(-940.06, 967.55) * mm, "end": v(-879.58, 967.55) * mm});
            skLineSegment(sketch, "E409", {"start": v(-940.06, 875.7) * mm, "end": v(-879.58, 875.7) * mm});
            skLineSegment(sketch, "E410", {"start": v(-879.58, 875.7) * mm, "end": v(-879.58, 686.41) * mm});
            skLineSegment(sketch, "E411", {"start": v(-879.58, 686.41) * mm, "end": v(-940.06, 686.41) * mm});
            skLineSegment(sketch, "E412", {"start": v(-940.06, 686.41) * mm, "end": v(-940.06, 875.7) * mm});
            skLineSegment(sketch, "E413", {"start": v(-861.66, 686.41) * mm, "end": v(-861.66, 875.7) * mm});
            skLineSegment(sketch, "E414", {"start": v(-861.66, 875.7) * mm, "end": v(-801.17, 875.7) * mm});
            skLineSegment(sketch, "E415", {"start": v(-801.17, 875.7) * mm, "end": v(-801.17, 686.41) * mm});
            skLineSegment(sketch, "E416", {"start": v(-801.17, 686.41) * mm, "end": v(-861.66, 686.41) * mm});
            skLineSegment(sketch, "E417", {"start": v(348.01, -987.53) * mm, "end": v(522.74, -987.53) * mm});
            skLineSegment(sketch, "E418", {"start": v(522.74, -987.53) * mm, "end": v(522.74, -670.55) * mm});
            skLineSegment(sketch, "E419", {"start": v(522.74, -670.55) * mm, "end": v(348.01, -670.55) * mm});
            skLineSegment(sketch, "E420", {"start": v(348.01, -670.55) * mm, "end": v(348.01, -987.53) * mm});
            skLineSegment(sketch, "E421", {"start": v(365.93, -780.32) * mm, "end": v(426.42, -780.32) * mm});
            skLineSegment(sketch, "E422", {"start": v(426.42, -780.32) * mm, "end": v(426.42, -969.6) * mm});
            skLineSegment(sketch, "E423", {"start": v(426.42, -969.6) * mm, "end": v(365.93, -969.6) * mm});
            skLineSegment(sketch, "E424", {"start": v(365.93, -969.6) * mm, "end": v(365.93, -780.32) * mm});
            skLineSegment(sketch, "E425", {"start": v(444.34, -969.6) * mm, "end": v(444.34, -780.32) * mm});
            skLineSegment(sketch, "E426", {"start": v(444.34, -780.32) * mm, "end": v(504.82, -780.32) * mm});
            skLineSegment(sketch, "E427", {"start": v(504.82, -780.32) * mm, "end": v(504.82, -969.6) * mm});
            skLineSegment(sketch, "E428", {"start": v(504.82, -969.6) * mm, "end": v(444.34, -969.6) * mm});
            skLineSegment(sketch, "E429", {"start": v(504.82, -762.4) * mm, "end": v(444.34, -762.4) * mm});
            skLineSegment(sketch, "E430", {"start": v(444.34, -762.4) * mm, "end": v(444.34, -688.47) * mm});
            skLineSegment(sketch, "E431", {"start": v(444.34, -688.47) * mm, "end": v(504.82, -688.47) * mm});
            skLineSegment(sketch, "E432", {"start": v(504.82, -688.47) * mm, "end": v(504.82, -762.4) * mm});
            skLineSegment(sketch, "E433", {"start": v(426.42, -688.47) * mm, "end": v(426.42, -762.4) * mm});
            skLineSegment(sketch, "E434", {"start": v(426.42, -762.4) * mm, "end": v(365.93, -762.4) * mm});
            skLineSegment(sketch, "E435", {"start": v(365.93, -762.4) * mm, "end": v(365.93, -688.47) * mm});
            skLineSegment(sketch, "E436", {"start": v(365.93, -688.47) * mm, "end": v(426.42, -688.47) * mm});
            skLineSegment(sketch, "E437", {"start": v(-529, -987.53) * mm, "end": v(-354.27, -987.53) * mm});
            skLineSegment(sketch, "E438", {"start": v(-354.27, -987.53) * mm, "end": v(-354.27, -670.55) * mm});
            skLineSegment(sketch, "E439", {"start": v(-354.27, -670.55) * mm, "end": v(-529, -670.55) * mm});
            skLineSegment(sketch, "E440", {"start": v(-529, -670.55) * mm, "end": v(-529, -987.53) * mm});
            skLineSegment(sketch, "E441", {"start": v(-511.08, -780.32) * mm, "end": v(-450.6, -780.32) * mm});
            skLineSegment(sketch, "E442", {"start": v(-450.6, -780.32) * mm, "end": v(-450.6, -969.6) * mm});
            skLineSegment(sketch, "E443", {"start": v(-450.6, -969.6) * mm, "end": v(-511.08, -969.6) * mm});
            skLineSegment(sketch, "E444", {"start": v(-511.08, -969.6) * mm, "end": v(-511.08, -780.32) * mm});
            skLineSegment(sketch, "E445", {"start": v(-432.67, -969.6) * mm, "end": v(-432.67, -780.32) * mm});
            skLineSegment(sketch, "E446", {"start": v(-432.67, -780.32) * mm, "end": v(-372.19, -780.32) * mm});
            skLineSegment(sketch, "E447", {"start": v(-372.19, -780.32) * mm, "end": v(-372.19, -969.6) * mm});
            skLineSegment(sketch, "E448", {"start": v(-372.19, -969.6) * mm, "end": v(-432.67, -969.6) * mm});
            skLineSegment(sketch, "E449", {"start": v(-372.19, -762.4) * mm, "end": v(-432.67, -762.4) * mm});
            skLineSegment(sketch, "E450", {"start": v(-432.67, -762.4) * mm, "end": v(-432.67, -688.47) * mm});
            skLineSegment(sketch, "E451", {"start": v(-432.67, -688.47) * mm, "end": v(-372.19, -688.47) * mm});
            skLineSegment(sketch, "E452", {"start": v(-372.19, -688.47) * mm, "end": v(-372.19, -762.4) * mm});
            skLineSegment(sketch, "E453", {"start": v(-450.6, -688.47) * mm, "end": v(-450.6, -762.4) * mm});
            skLineSegment(sketch, "E454", {"start": v(-450.6, -762.4) * mm, "end": v(-511.08, -762.4) * mm});
            skLineSegment(sketch, "E455", {"start": v(-511.08, -762.4) * mm, "end": v(-511.08, -688.47) * mm});
            skLineSegment(sketch, "E456", {"start": v(-511.08, -688.47) * mm, "end": v(-450.6, -688.47) * mm});
            skLineSegment(sketch, "E457", {"start": v(-957.98, -987.53) * mm, "end": v(-783.25, -987.53) * mm});
            skLineSegment(sketch, "E458", {"start": v(-783.25, -987.53) * mm, "end": v(-783.25, -670.55) * mm});
            skLineSegment(sketch, "E459", {"start": v(-783.25, -670.55) * mm, "end": v(-957.98, -670.55) * mm});
            skLineSegment(sketch, "E460", {"start": v(-957.98, -670.55) * mm, "end": v(-957.98, -987.53) * mm});
            skLineSegment(sketch, "E461", {"start": v(-940.06, -780.32) * mm, "end": v(-879.58, -780.32) * mm});
            skLineSegment(sketch, "E462", {"start": v(-879.58, -780.32) * mm, "end": v(-879.58, -969.6) * mm});
            skLineSegment(sketch, "E463", {"start": v(-879.58, -969.6) * mm, "end": v(-940.06, -969.6) * mm});
            skLineSegment(sketch, "E464", {"start": v(-940.06, -969.6) * mm, "end": v(-940.06, -780.32) * mm});
            skLineSegment(sketch, "E465", {"start": v(-861.66, -969.6) * mm, "end": v(-861.66, -780.32) * mm});
            skLineSegment(sketch, "E466", {"start": v(-861.66, -780.32) * mm, "end": v(-801.17, -780.32) * mm});
            skLineSegment(sketch, "E467", {"start": v(-801.17, -780.32) * mm, "end": v(-801.17, -969.6) * mm});
            skLineSegment(sketch, "E468", {"start": v(-801.17, -969.6) * mm, "end": v(-861.66, -969.6) * mm});
            skLineSegment(sketch, "E469", {"start": v(-801.17, -762.4) * mm, "end": v(-861.66, -762.4) * mm});
            skLineSegment(sketch, "E470", {"start": v(-861.66, -762.4) * mm, "end": v(-861.66, -688.47) * mm});
            skLineSegment(sketch, "E471", {"start": v(-861.66, -688.47) * mm, "end": v(-801.17, -688.47) * mm});
            skLineSegment(sketch, "E472", {"start": v(-801.17, -688.47) * mm, "end": v(-801.17, -762.4) * mm});
            skLineSegment(sketch, "E473", {"start": v(-879.58, -688.47) * mm, "end": v(-879.58, -762.4) * mm});
            skLineSegment(sketch, "E474", {"start": v(-879.58, -762.4) * mm, "end": v(-940.06, -762.4) * mm});
            skLineSegment(sketch, "E475", {"start": v(-940.06, -762.4) * mm, "end": v(-940.06, -688.47) * mm});
            skLineSegment(sketch, "E476", {"start": v(-940.06, -688.47) * mm, "end": v(-879.58, -688.47) * mm});
            skLineSegment(sketch, "E477", {"start": v(-1271.6, -987.53) * mm, "end": v(-1096.87, -987.53) * mm});
            skLineSegment(sketch, "E478", {"start": v(-1096.87, -987.53) * mm, "end": v(-1096.87, -670.55) * mm});
            skLineSegment(sketch, "E479", {"start": v(-1096.87, -670.55) * mm, "end": v(-1271.6, -670.55) * mm});
            skLineSegment(sketch, "E480", {"start": v(-1271.6, -670.55) * mm, "end": v(-1271.6, -987.53) * mm});
            skLineSegment(sketch, "E481", {"start": v(-1253.68, -780.32) * mm, "end": v(-1193.2, -780.32) * mm});
            skLineSegment(sketch, "E482", {"start": v(-1193.2, -780.32) * mm, "end": v(-1193.2, -969.6) * mm});
            skLineSegment(sketch, "E483", {"start": v(-1193.2, -969.6) * mm, "end": v(-1253.68, -969.6) * mm});
            skLineSegment(sketch, "E484", {"start": v(-1253.68, -969.6) * mm, "end": v(-1253.68, -780.32) * mm});
            skLineSegment(sketch, "E485", {"start": v(-1175.28, -969.6) * mm, "end": v(-1175.28, -780.32) * mm});
            skLineSegment(sketch, "E486", {"start": v(-1175.28, -780.32) * mm, "end": v(-1114.8, -780.32) * mm});
            skLineSegment(sketch, "E487", {"start": v(-1114.8, -780.32) * mm, "end": v(-1114.8, -969.6) * mm});
            skLineSegment(sketch, "E488", {"start": v(-1114.8, -969.6) * mm, "end": v(-1175.28, -969.6) * mm});
            skLineSegment(sketch, "E489", {"start": v(-1114.8, -762.4) * mm, "end": v(-1175.28, -762.4) * mm});
            skLineSegment(sketch, "E490", {"start": v(-1175.28, -762.4) * mm, "end": v(-1175.28, -688.47) * mm});
            skLineSegment(sketch, "E491", {"start": v(-1175.28, -688.47) * mm, "end": v(-1114.8, -688.47) * mm});
            skLineSegment(sketch, "E492", {"start": v(-1114.8, -688.47) * mm, "end": v(-1114.8, -762.4) * mm});
            skLineSegment(sketch, "E493", {"start": v(-1193.2, -688.47) * mm, "end": v(-1193.2, -762.4) * mm});
            skLineSegment(sketch, "E494", {"start": v(-1193.2, -762.4) * mm, "end": v(-1253.68, -762.4) * mm});
            skLineSegment(sketch, "E495", {"start": v(-1253.68, -762.4) * mm, "end": v(-1253.68, -688.47) * mm});
            skLineSegment(sketch, "E496", {"start": v(-1253.68, -688.47) * mm, "end": v(-1193.2, -688.47) * mm});
            skLineSegment(sketch, "E497", {"start": v(208, 988.27) * mm, "end": v(104.97, 988.27) * mm});
            skLineSegment(sketch, "E498", {"start": v(104.97, 988.27) * mm, "end": v(104.97, 669.8) * mm});
            skLineSegment(sketch, "E499", {"start": v(104.97, 669.8) * mm, "end": v(208, 669.8) * mm});
            skLineSegment(sketch, "E500", {"start": v(208, 669.8) * mm, "end": v(208, 988.27) * mm});
            skLineSegment(sketch, "E501", {"start": v(190.08, 970.35) * mm, "end": v(190.08, 896.43) * mm});
            skLineSegment(sketch, "E502", {"start": v(190.08, 896.43) * mm, "end": v(122.88, 896.43) * mm});
            skLineSegment(sketch, "E503", {"start": v(122.88, 896.43) * mm, "end": v(122.88, 970.35) * mm});
            skLineSegment(sketch, "E504", {"start": v(122.88, 970.35) * mm, "end": v(190.08, 970.35) * mm});
            skLineSegment(sketch, "E505", {"start": v(122.88, 687.72) * mm, "end": v(122.88, 878.5) * mm});
            skLineSegment(sketch, "E506", {"start": v(122.88, 878.5) * mm, "end": v(190.08, 878.5) * mm});
            skLineSegment(sketch, "E507", {"start": v(190.08, 878.5) * mm, "end": v(190.08, 687.72) * mm});
            skLineSegment(sketch, "E508", {"start": v(190.08, 687.72) * mm, "end": v(122.88, 687.72) * mm});
            skLineSegment(sketch, "E509", {"start": v(-110.1, 988.27) * mm, "end": v(-213.14, 988.27) * mm});
            skLineSegment(sketch, "E510", {"start": v(-213.14, 988.27) * mm, "end": v(-213.14, 669.8) * mm});
            skLineSegment(sketch, "E511", {"start": v(-213.14, 669.8) * mm, "end": v(-110.1, 669.8) * mm});
            skLineSegment(sketch, "E512", {"start": v(-110.1, 669.8) * mm, "end": v(-110.1, 988.27) * mm});
            skLineSegment(sketch, "E513", {"start": v(-128.01, 970.35) * mm, "end": v(-128.01, 896.43) * mm});
            skLineSegment(sketch, "E514", {"start": v(-128.01, 896.43) * mm, "end": v(-195.22, 896.43) * mm});
            skLineSegment(sketch, "E515", {"start": v(-195.22, 896.43) * mm, "end": v(-195.22, 970.35) * mm});
            skLineSegment(sketch, "E516", {"start": v(-195.22, 970.35) * mm, "end": v(-128.01, 970.35) * mm});
            skLineSegment(sketch, "E517", {"start": v(-195.22, 687.72) * mm, "end": v(-195.22, 878.5) * mm});
            skLineSegment(sketch, "E518", {"start": v(-195.22, 878.5) * mm, "end": v(-128.01, 878.5) * mm});
            skLineSegment(sketch, "E519", {"start": v(-128.01, 878.5) * mm, "end": v(-128.01, 687.72) * mm});
            skLineSegment(sketch, "E520", {"start": v(-128.01, 687.72) * mm, "end": v(-195.22, 687.72) * mm});
            skLineSegment(sketch, "E521", {"start": v(84.25, -118.72) * mm, "end": v(-90.49, -118.72) * mm});
            skLineSegment(sketch, "E522", {"start": v(-90.49, -118.72) * mm, "end": v(-90.49, -435.7) * mm});
            skLineSegment(sketch, "E523", {"start": v(-90.49, -435.7) * mm, "end": v(84.25, -435.7) * mm});
            skLineSegment(sketch, "E524", {"start": v(84.25, -435.7) * mm, "end": v(84.25, -118.72) * mm});
            skLineSegment(sketch, "E525", {"start": v(66.32, -136.64) * mm, "end": v(66.32, -210.57) * mm});
            skLineSegment(sketch, "E526", {"start": v(66.32, -210.57) * mm, "end": v(-72.57, -210.57) * mm});
            skLineSegment(sketch, "E527", {"start": v(-72.57, -210.57) * mm, "end": v(-72.57, -136.64) * mm});
            skLineSegment(sketch, "E528", {"start": v(-72.57, -136.64) * mm, "end": v(66.32, -136.64) * mm});
            skLineSegment(sketch, "E529", {"start": v(-72.57, -228.49) * mm, "end": v(-12.08, -228.49) * mm});
            skLineSegment(sketch, "E530", {"start": v(-12.08, -228.49) * mm, "end": v(-12.08, -417.78) * mm});
            skLineSegment(sketch, "E531", {"start": v(-12.08, -417.78) * mm, "end": v(-72.57, -417.78) * mm});
            skLineSegment(sketch, "E532", {"start": v(-72.57, -417.78) * mm, "end": v(-72.57, -228.49) * mm});
            skLineSegment(sketch, "E533", {"start": v(5.84, -417.78) * mm, "end": v(5.84, -228.49) * mm});
            skLineSegment(sketch, "E534", {"start": v(5.84, -228.49) * mm, "end": v(66.32, -228.49) * mm});
            skLineSegment(sketch, "E535", {"start": v(66.32, -228.49) * mm, "end": v(66.32, -417.78) * mm});
            skLineSegment(sketch, "E536", {"start": v(66.32, -417.78) * mm, "end": v(5.84, -417.78) * mm});
            skLineSegment(sketch, "E537", {"start": v(207.44, -118.72) * mm, "end": v(104.4, -118.72) * mm});
            skLineSegment(sketch, "E538", {"start": v(104.4, -118.72) * mm, "end": v(104.4, -437.2) * mm});
            skLineSegment(sketch, "E539", {"start": v(104.4, -437.2) * mm, "end": v(207.44, -437.2) * mm});
            skLineSegment(sketch, "E540", {"start": v(207.44, -437.2) * mm, "end": v(207.44, -118.72) * mm});
            skLineSegment(sketch, "E541", {"start": v(189.52, -136.64) * mm, "end": v(189.52, -210.57) * mm});
            skLineSegment(sketch, "E542", {"start": v(189.52, -210.57) * mm, "end": v(122.32, -210.57) * mm});
            skLineSegment(sketch, "E543", {"start": v(122.32, -210.57) * mm, "end": v(122.32, -136.64) * mm});
            skLineSegment(sketch, "E544", {"start": v(122.32, -136.64) * mm, "end": v(189.52, -136.64) * mm});
            skLineSegment(sketch, "E545", {"start": v(122.32, -419.28) * mm, "end": v(122.32, -228.49) * mm});
            skLineSegment(sketch, "E546", {"start": v(122.32, -228.49) * mm, "end": v(189.52, -228.49) * mm});
            skLineSegment(sketch, "E547", {"start": v(189.52, -228.49) * mm, "end": v(189.52, -419.28) * mm});
            skLineSegment(sketch, "E548", {"start": v(189.52, -419.28) * mm, "end": v(122.32, -419.28) * mm});
            skLineSegment(sketch, "E549", {"start": v(-110.65, -118.72) * mm, "end": v(-213.7, -118.72) * mm});
            skLineSegment(sketch, "E550", {"start": v(-213.7, -118.72) * mm, "end": v(-213.7, -437.2) * mm});
            skLineSegment(sketch, "E551", {"start": v(-213.7, -437.2) * mm, "end": v(-110.65, -437.2) * mm});
            skLineSegment(sketch, "E552", {"start": v(-110.65, -437.2) * mm, "end": v(-110.65, -118.72) * mm});
            skLineSegment(sketch, "E553", {"start": v(-128.57, -136.64) * mm, "end": v(-128.57, -210.57) * mm});
            skLineSegment(sketch, "E554", {"start": v(-128.57, -210.57) * mm, "end": v(-195.78, -210.57) * mm});
            skLineSegment(sketch, "E555", {"start": v(-195.78, -210.57) * mm, "end": v(-195.78, -136.64) * mm});
            skLineSegment(sketch, "E556", {"start": v(-195.78, -136.64) * mm, "end": v(-128.57, -136.64) * mm});
            skLineSegment(sketch, "E557", {"start": v(-195.78, -419.28) * mm, "end": v(-195.78, -228.49) * mm});
            skLineSegment(sketch, "E558", {"start": v(-195.78, -228.49) * mm, "end": v(-128.57, -228.49) * mm});
            skLineSegment(sketch, "E559", {"start": v(-128.57, -228.49) * mm, "end": v(-128.57, -419.28) * mm});
            skLineSegment(sketch, "E560", {"start": v(-128.57, -419.28) * mm, "end": v(-195.78, -419.28) * mm});
            skLineSegment(sketch, "E561", {"start": v(-89.93, -986.78) * mm, "end": v(84.8, -986.78) * mm});
            skLineSegment(sketch, "E562", {"start": v(84.8, -986.78) * mm, "end": v(84.8, -669.8) * mm});
            skLineSegment(sketch, "E563", {"start": v(84.8, -669.8) * mm, "end": v(-89.93, -669.8) * mm});
            skLineSegment(sketch, "E564", {"start": v(-89.93, -669.8) * mm, "end": v(-89.93, -986.78) * mm});
            skLineSegment(sketch, "E565", {"start": v(-72, -779.56) * mm, "end": v(-11.52, -779.56) * mm});
            skLineSegment(sketch, "E566", {"start": v(-11.52, -779.56) * mm, "end": v(-11.52, -968.86) * mm});
            skLineSegment(sketch, "E567", {"start": v(-11.52, -968.86) * mm, "end": v(-72, -968.86) * mm});
            skLineSegment(sketch, "E568", {"start": v(-72, -968.86) * mm, "end": v(-72, -779.56) * mm});
            skLineSegment(sketch, "E569", {"start": v(6.4, -968.86) * mm, "end": v(6.4, -779.56) * mm});
            skLineSegment(sketch, "E570", {"start": v(6.4, -779.56) * mm, "end": v(66.88, -779.56) * mm});
            skLineSegment(sketch, "E571", {"start": v(66.88, -779.56) * mm, "end": v(66.88, -968.86) * mm});
            skLineSegment(sketch, "E572", {"start": v(66.88, -968.86) * mm, "end": v(6.4, -968.86) * mm});
            skLineSegment(sketch, "E573", {"start": v(66.88, -687.72) * mm, "end": v(66.88, -761.64) * mm});
            skLineSegment(sketch, "E574", {"start": v(66.88, -761.64) * mm, "end": v(-72, -761.64) * mm});
            skLineSegment(sketch, "E575", {"start": v(-72, -761.64) * mm, "end": v(-72, -687.72) * mm});
            skLineSegment(sketch, "E576", {"start": v(-72, -687.72) * mm, "end": v(66.88, -687.72) * mm});
            skLineSegment(sketch, "E577", {"start": v(104.97, -988.27) * mm, "end": v(208, -988.27) * mm});
            skLineSegment(sketch, "E578", {"start": v(208, -988.27) * mm, "end": v(208, -669.8) * mm});
            skLineSegment(sketch, "E579", {"start": v(208, -669.8) * mm, "end": v(104.97, -669.8) * mm});
            skLineSegment(sketch, "E580", {"start": v(104.97, -669.8) * mm, "end": v(104.97, -988.27) * mm});
            skLineSegment(sketch, "E581", {"start": v(122.88, -970.35) * mm, "end": v(122.88, -779.56) * mm});
            skLineSegment(sketch, "E582", {"start": v(122.88, -779.56) * mm, "end": v(190.08, -779.56) * mm});
            skLineSegment(sketch, "E583", {"start": v(190.08, -779.56) * mm, "end": v(190.08, -970.35) * mm});
            skLineSegment(sketch, "E584", {"start": v(190.08, -970.35) * mm, "end": v(122.88, -970.35) * mm});
            skLineSegment(sketch, "E585", {"start": v(190.08, -687.72) * mm, "end": v(190.08, -761.64) * mm});
            skLineSegment(sketch, "E586", {"start": v(190.08, -761.64) * mm, "end": v(122.88, -761.64) * mm});
            skLineSegment(sketch, "E587", {"start": v(122.88, -761.64) * mm, "end": v(122.88, -687.72) * mm});
            skLineSegment(sketch, "E588", {"start": v(122.88, -687.72) * mm, "end": v(190.08, -687.72) * mm});
            skLineSegment(sketch, "E589", {"start": v(-213.14, -988.27) * mm, "end": v(-110.1, -988.27) * mm});
            skLineSegment(sketch, "E590", {"start": v(-110.1, -988.27) * mm, "end": v(-110.1, -669.8) * mm});
            skLineSegment(sketch, "E591", {"start": v(-110.1, -669.8) * mm, "end": v(-213.14, -669.8) * mm});
            skLineSegment(sketch, "E592", {"start": v(-213.14, -669.8) * mm, "end": v(-213.14, -988.27) * mm});
            skLineSegment(sketch, "E593", {"start": v(-195.22, -970.35) * mm, "end": v(-195.22, -779.56) * mm});
            skLineSegment(sketch, "E594", {"start": v(-195.22, -779.56) * mm, "end": v(-128.01, -779.56) * mm});
            skLineSegment(sketch, "E595", {"start": v(-128.01, -779.56) * mm, "end": v(-128.01, -970.35) * mm});
            skLineSegment(sketch, "E596", {"start": v(-128.01, -970.35) * mm, "end": v(-195.22, -970.35) * mm});
            skLineSegment(sketch, "E597", {"start": v(-128.01, -687.72) * mm, "end": v(-128.01, -761.64) * mm});
            skLineSegment(sketch, "E598", {"start": v(-128.01, -761.64) * mm, "end": v(-195.22, -761.64) * mm});
            skLineSegment(sketch, "E599", {"start": v(-195.22, -761.64) * mm, "end": v(-195.22, -687.72) * mm});
            skLineSegment(sketch, "E600", {"start": v(-195.22, -687.72) * mm, "end": v(-128.01, -687.72) * mm});
            skLineSegment(sketch, "E601", {"start": v(3163.15, -482.38) * mm, "end": v(1424.02, -482.38) * mm});
            skLineSegment(sketch, "E602", {"start": v(1424.02, -482.38) * mm, "end": v(1374, -482.38) * mm});
            skLineSegment(sketch, "E603", {"start": v(1374, -482.38) * mm, "end": v(1321.36, -482.38) * mm});
            skLineSegment(sketch, "E604", {"start": v(1321.36, -482.38) * mm, "end": v(-1323.31, -482.38) * mm});
            skLineSegment(sketch, "E605", {"start": v(-1323.31, -482.38) * mm, "end": v(-3221.18, -482.38) * mm});
            skLineSegment(sketch, "E606", {"start": v(-3221.18, -482.38) * mm, "end": v(-3221.18, -535.39) * mm});
            skLineSegment(sketch, "E607", {"start": v(-3221.18, -535.39) * mm, "end": v(-1323.31, -535.39) * mm});
            skLineSegment(sketch, "E608", {"start": v(-1323.31, -535.39) * mm, "end": v(1321.36, -535.39) * mm});
            skLineSegment(sketch, "E609", {"start": v(1321.36, -535.39) * mm, "end": v(1374, -535.39) * mm});
            skLineSegment(sketch, "E610", {"start": v(1374, -535.39) * mm, "end": v(1424.02, -535.39) * mm});
            skLineSegment(sketch, "E611", {"start": v(1424.02, -535.39) * mm, "end": v(3163.15, -535.39) * mm});
            skLineSegment(sketch, "E612", {"start": v(3163.15, -535.39) * mm, "end": v(3163.15, -482.38) * mm});
            skLineSegment(sketch, "E613", {"start": v(-2246.37, 70.18) * mm, "end": v(-3207.95, 70.18) * mm});
            skLineSegment(sketch, "E614", {"start": v(-3207.95, 70.18) * mm, "end": v(-3207.95, 17.17) * mm});
            skLineSegment(sketch, "E615", {"start": v(-3207.95, 17.17) * mm, "end": v(-2246.37, 17.17) * mm});
            skLineSegment(sketch, "E616", {"start": v(-2246.37, 17.17) * mm, "end": v(-2246.37, 70.18) * mm});
            skLineSegment(sketch, "E617", {"start": v(-1783.01, 17.17) * mm, "end": v(-1323.31, 17.17) * mm});
            skLineSegment(sketch, "E618", {"start": v(-1323.31, 17.17) * mm, "end": v(-235.54, 17.17) * mm});
            skLineSegment(sketch, "E619", {"start": v(-235.54, 17.17) * mm, "end": v(-235.54, 70.18) * mm});
            skLineSegment(sketch, "E620", {"start": v(-235.54, 70.18) * mm, "end": v(-1323.31, 70.18) * mm});
            skLineSegment(sketch, "E621", {"start": v(-1323.31, 70.18) * mm, "end": v(-1783.01, 70.18) * mm});
            skLineSegment(sketch, "E622", {"start": v(-1783.01, 70.18) * mm, "end": v(-1783.01, 17.17) * mm});
            skLineSegment(sketch, "E623", {"start": v(1374, 17.17) * mm, "end": v(1433.66, 17.17) * mm});
            skLineSegment(sketch, "E624", {"start": v(1433.66, 17.17) * mm, "end": v(1769.78, 17.17) * mm});
            skLineSegment(sketch, "E625", {"start": v(1769.78, 17.17) * mm, "end": v(1769.78, 70.18) * mm});
            skLineSegment(sketch, "E626", {"start": v(1769.78, 70.18) * mm, "end": v(1433.66, 70.18) * mm});
            skLineSegment(sketch, "E627", {"start": v(1433.66, 70.18) * mm, "end": v(1374, 70.18) * mm});
            skLineSegment(sketch, "E628", {"start": v(1374, 70.18) * mm, "end": v(1318.75, 70.18) * mm});
            skLineSegment(sketch, "E629", {"start": v(1318.75, 70.18) * mm, "end": v(238.92, 70.18) * mm});
            skLineSegment(sketch, "E630", {"start": v(238.92, 70.18) * mm, "end": v(238.92, 17.17) * mm});
            skLineSegment(sketch, "E631", {"start": v(238.92, 17.17) * mm, "end": v(1321.36, 17.17) * mm});
            skLineSegment(sketch, "E632", {"start": v(1321.36, 17.17) * mm, "end": v(1374, 17.17) * mm});
            skLineSegment(sketch, "E633", {"start": v(-3066.82, 433.84) * mm, "end": v(-3241.56, 433.84) * mm});
            skLineSegment(sketch, "E634", {"start": v(-3241.56, 433.84) * mm, "end": v(-3241.56, 116.86) * mm});
            skLineSegment(sketch, "E635", {"start": v(-3241.56, 116.86) * mm, "end": v(-3066.82, 116.86) * mm});
            skLineSegment(sketch, "E636", {"start": v(-3066.82, 116.86) * mm, "end": v(-3066.82, 433.84) * mm});
            skLineSegment(sketch, "E637", {"start": v(-3084.75, 342) * mm, "end": v(-3145.23, 342) * mm});
            skLineSegment(sketch, "E638", {"start": v(-3145.23, 342) * mm, "end": v(-3145.23, 415.92) * mm});
            skLineSegment(sketch, "E639", {"start": v(-3145.23, 415.92) * mm, "end": v(-3084.75, 415.92) * mm});
            skLineSegment(sketch, "E640", {"start": v(-3084.75, 415.92) * mm, "end": v(-3084.75, 342) * mm});
            skLineSegment(sketch, "E641", {"start": v(-3163.15, 415.92) * mm, "end": v(-3163.15, 342) * mm});
            skLineSegment(sketch, "E642", {"start": v(-3163.15, 342) * mm, "end": v(-3223.63, 342) * mm});
            skLineSegment(sketch, "E643", {"start": v(-3223.63, 342) * mm, "end": v(-3223.63, 415.92) * mm});
            skLineSegment(sketch, "E644", {"start": v(-3223.63, 415.92) * mm, "end": v(-3163.15, 415.92) * mm});
            skLineSegment(sketch, "E645", {"start": v(-3223.63, 324.07) * mm, "end": v(-3163.15, 324.07) * mm});
            skLineSegment(sketch, "E646", {"start": v(-3163.15, 324.07) * mm, "end": v(-3163.15, 134.78) * mm});
            skLineSegment(sketch, "E647", {"start": v(-3163.15, 134.78) * mm, "end": v(-3223.63, 134.78) * mm});
            skLineSegment(sketch, "E648", {"start": v(-3223.63, 134.78) * mm, "end": v(-3223.63, 324.07) * mm});
            skLineSegment(sketch, "E649", {"start": v(-3145.23, 134.78) * mm, "end": v(-3145.23, 324.07) * mm});
            skLineSegment(sketch, "E650", {"start": v(-3145.23, 324.07) * mm, "end": v(-3084.75, 324.07) * mm});
            skLineSegment(sketch, "E651", {"start": v(-3084.75, 324.07) * mm, "end": v(-3084.75, 134.78) * mm});
            skLineSegment(sketch, "E652", {"start": v(-3084.75, 134.78) * mm, "end": v(-3145.23, 134.78) * mm});
            skLineSegment(sketch, "E653", {"start": v(-3066.82, 988.27) * mm, "end": v(-3241.56, 988.27) * mm});
            skLineSegment(sketch, "E654", {"start": v(-3241.56, 988.27) * mm, "end": v(-3241.56, 671.3) * mm});
            skLineSegment(sketch, "E655", {"start": v(-3241.56, 671.3) * mm, "end": v(-3066.82, 671.3) * mm});
            skLineSegment(sketch, "E656", {"start": v(-3066.82, 671.3) * mm, "end": v(-3066.82, 988.27) * mm});
            skLineSegment(sketch, "E657", {"start": v(-3084.75, 896.43) * mm, "end": v(-3145.23, 896.43) * mm});
            skLineSegment(sketch, "E658", {"start": v(-3145.23, 896.43) * mm, "end": v(-3145.23, 970.35) * mm});
            skLineSegment(sketch, "E659", {"start": v(-3145.23, 970.35) * mm, "end": v(-3084.75, 970.35) * mm});
            skLineSegment(sketch, "E660", {"start": v(-3084.75, 970.35) * mm, "end": v(-3084.75, 896.43) * mm});
            skLineSegment(sketch, "E661", {"start": v(-3163.15, 970.35) * mm, "end": v(-3163.15, 896.43) * mm});
            skLineSegment(sketch, "E662", {"start": v(-3163.15, 896.43) * mm, "end": v(-3223.63, 896.43) * mm});
            skLineSegment(sketch, "E663", {"start": v(-3223.63, 896.43) * mm, "end": v(-3223.63, 970.35) * mm});
            skLineSegment(sketch, "E664", {"start": v(-3223.63, 970.35) * mm, "end": v(-3163.15, 970.35) * mm});
            skLineSegment(sketch, "E665", {"start": v(-3223.63, 878.5) * mm, "end": v(-3163.15, 878.5) * mm});
            skLineSegment(sketch, "E666", {"start": v(-3163.15, 878.5) * mm, "end": v(-3163.15, 689.21) * mm});
            skLineSegment(sketch, "E667", {"start": v(-3163.15, 689.21) * mm, "end": v(-3223.63, 689.21) * mm});
            skLineSegment(sketch, "E668", {"start": v(-3223.63, 689.21) * mm, "end": v(-3223.63, 878.5) * mm});
            skLineSegment(sketch, "E669", {"start": v(-3145.23, 689.21) * mm, "end": v(-3145.23, 878.5) * mm});
            skLineSegment(sketch, "E670", {"start": v(-3145.23, 878.5) * mm, "end": v(-3084.75, 878.5) * mm});
            skLineSegment(sketch, "E671", {"start": v(-3084.75, 878.5) * mm, "end": v(-3084.75, 689.21) * mm});
            skLineSegment(sketch, "E672", {"start": v(-3084.75, 689.21) * mm, "end": v(-3145.23, 689.21) * mm});
            skLineSegment(sketch, "E673", {"start": v(-2789.05, 433.84) * mm, "end": v(-2963.78, 433.84) * mm});
            skLineSegment(sketch, "E674", {"start": v(-2963.78, 433.84) * mm, "end": v(-2963.78, 116.86) * mm});
            skLineSegment(sketch, "E675", {"start": v(-2963.78, 116.86) * mm, "end": v(-2789.05, 116.86) * mm});
            skLineSegment(sketch, "E676", {"start": v(-2789.05, 116.86) * mm, "end": v(-2789.05, 433.84) * mm});
            skLineSegment(sketch, "E677", {"start": v(-2806.97, 342) * mm, "end": v(-2867.45, 342) * mm});
            skLineSegment(sketch, "E678", {"start": v(-2867.45, 342) * mm, "end": v(-2867.45, 415.92) * mm});
            skLineSegment(sketch, "E679", {"start": v(-2867.45, 415.92) * mm, "end": v(-2806.97, 415.92) * mm});
            skLineSegment(sketch, "E680", {"start": v(-2806.97, 415.92) * mm, "end": v(-2806.97, 342) * mm});
            skLineSegment(sketch, "E681", {"start": v(-2885.37, 415.92) * mm, "end": v(-2885.37, 342) * mm});
            skLineSegment(sketch, "E682", {"start": v(-2885.37, 342) * mm, "end": v(-2945.86, 342) * mm});
            skLineSegment(sketch, "E683", {"start": v(-2945.86, 342) * mm, "end": v(-2945.86, 415.92) * mm});
            skLineSegment(sketch, "E684", {"start": v(-2945.86, 415.92) * mm, "end": v(-2885.37, 415.92) * mm});
            skLineSegment(sketch, "E685", {"start": v(-2945.86, 324.07) * mm, "end": v(-2885.37, 324.07) * mm});
            skLineSegment(sketch, "E686", {"start": v(-2885.37, 324.07) * mm, "end": v(-2885.37, 134.78) * mm});
            skLineSegment(sketch, "E687", {"start": v(-2885.37, 134.78) * mm, "end": v(-2945.86, 134.78) * mm});
            skLineSegment(sketch, "E688", {"start": v(-2945.86, 134.78) * mm, "end": v(-2945.86, 324.07) * mm});
            skLineSegment(sketch, "E689", {"start": v(-2867.45, 134.78) * mm, "end": v(-2867.45, 324.07) * mm});
            skLineSegment(sketch, "E690", {"start": v(-2867.45, 324.07) * mm, "end": v(-2806.97, 324.07) * mm});
            skLineSegment(sketch, "E691", {"start": v(-2806.97, 324.07) * mm, "end": v(-2806.97, 134.78) * mm});
            skLineSegment(sketch, "E692", {"start": v(-2806.97, 134.78) * mm, "end": v(-2867.45, 134.78) * mm});
            skLineSegment(sketch, "E693", {"start": v(-2188.7, -119.48) * mm, "end": v(-2363.42, -119.48) * mm});
            skLineSegment(sketch, "E694", {"start": v(-2363.42, -119.48) * mm, "end": v(-2363.42, -436.46) * mm});
            skLineSegment(sketch, "E695", {"start": v(-2363.42, -436.46) * mm, "end": v(-2188.7, -436.46) * mm});
            skLineSegment(sketch, "E696", {"start": v(-2188.7, -436.46) * mm, "end": v(-2188.7, -119.48) * mm});
            skLineSegment(sketch, "E697", {"start": v(-2206.61, -211.32) * mm, "end": v(-2267.1, -211.32) * mm});
            skLineSegment(sketch, "E698", {"start": v(-2267.1, -211.32) * mm, "end": v(-2267.1, -137.4) * mm});
            skLineSegment(sketch, "E699", {"start": v(-2267.1, -137.4) * mm, "end": v(-2206.61, -137.4) * mm});
            skLineSegment(sketch, "E700", {"start": v(-2206.61, -137.4) * mm, "end": v(-2206.61, -211.32) * mm});
            skLineSegment(sketch, "E701", {"start": v(-2285.02, -137.4) * mm, "end": v(-2285.02, -211.32) * mm});
            skLineSegment(sketch, "E702", {"start": v(-2285.02, -211.32) * mm, "end": v(-2345.5, -211.32) * mm});
            skLineSegment(sketch, "E703", {"start": v(-2345.5, -211.32) * mm, "end": v(-2345.5, -137.4) * mm});
            skLineSegment(sketch, "E704", {"start": v(-2345.5, -137.4) * mm, "end": v(-2285.02, -137.4) * mm});
            skLineSegment(sketch, "E705", {"start": v(-2345.5, -229.24) * mm, "end": v(-2285.02, -229.24) * mm});
            skLineSegment(sketch, "E706", {"start": v(-2285.02, -229.24) * mm, "end": v(-2285.02, -418.53) * mm});
            skLineSegment(sketch, "E707", {"start": v(-2285.02, -418.53) * mm, "end": v(-2345.5, -418.53) * mm});
            skLineSegment(sketch, "E708", {"start": v(-2345.5, -418.53) * mm, "end": v(-2345.5, -229.24) * mm});
            skLineSegment(sketch, "E709", {"start": v(-2267.1, -418.53) * mm, "end": v(-2267.1, -229.24) * mm});
            skLineSegment(sketch, "E710", {"start": v(-2267.1, -229.24) * mm, "end": v(-2206.61, -229.24) * mm});
            skLineSegment(sketch, "E711", {"start": v(-2206.61, -229.24) * mm, "end": v(-2206.61, -418.53) * mm});
            skLineSegment(sketch, "E712", {"start": v(-2206.61, -418.53) * mm, "end": v(-2267.1, -418.53) * mm});
            skLineSegment(sketch, "E713", {"start": v(-2188.7, 988.27) * mm, "end": v(-2363.42, 988.27) * mm});
            skLineSegment(sketch, "E714", {"start": v(-2363.42, 988.27) * mm, "end": v(-2363.42, 671.3) * mm});
            skLineSegment(sketch, "E715", {"start": v(-2363.42, 671.3) * mm, "end": v(-2188.7, 671.3) * mm});
            skLineSegment(sketch, "E716", {"start": v(-2188.7, 671.3) * mm, "end": v(-2188.7, 988.27) * mm});
            skLineSegment(sketch, "E717", {"start": v(-2206.61, 896.43) * mm, "end": v(-2267.1, 896.43) * mm});
            skLineSegment(sketch, "E718", {"start": v(-2267.1, 896.43) * mm, "end": v(-2267.1, 970.35) * mm});
            skLineSegment(sketch, "E719", {"start": v(-2267.1, 970.35) * mm, "end": v(-2206.61, 970.35) * mm});
            skLineSegment(sketch, "E720", {"start": v(-2206.61, 970.35) * mm, "end": v(-2206.61, 896.43) * mm});
            skLineSegment(sketch, "E721", {"start": v(-2285.02, 970.35) * mm, "end": v(-2285.02, 896.43) * mm});
            skLineSegment(sketch, "E722", {"start": v(-2285.02, 896.43) * mm, "end": v(-2345.5, 896.43) * mm});
            skLineSegment(sketch, "E723", {"start": v(-2345.5, 896.43) * mm, "end": v(-2345.5, 970.35) * mm});
            skLineSegment(sketch, "E724", {"start": v(-2345.5, 970.35) * mm, "end": v(-2285.02, 970.35) * mm});
            skLineSegment(sketch, "E725", {"start": v(-2345.5, 878.5) * mm, "end": v(-2285.02, 878.5) * mm});
            skLineSegment(sketch, "E726", {"start": v(-2285.02, 878.5) * mm, "end": v(-2285.02, 689.21) * mm});
            skLineSegment(sketch, "E727", {"start": v(-2285.02, 689.21) * mm, "end": v(-2345.5, 689.21) * mm});
            skLineSegment(sketch, "E728", {"start": v(-2345.5, 689.21) * mm, "end": v(-2345.5, 878.5) * mm});
            skLineSegment(sketch, "E729", {"start": v(-2267.1, 689.21) * mm, "end": v(-2267.1, 878.5) * mm});
            skLineSegment(sketch, "E730", {"start": v(-2267.1, 878.5) * mm, "end": v(-2206.61, 878.5) * mm});
            skLineSegment(sketch, "E731", {"start": v(-2206.61, 878.5) * mm, "end": v(-2206.61, 689.21) * mm});
            skLineSegment(sketch, "E732", {"start": v(-2206.61, 689.21) * mm, "end": v(-2267.1, 689.21) * mm});
            skLineSegment(sketch, "E733", {"start": v(-2628.88, 988.27) * mm, "end": v(-2803.6, 988.27) * mm});
            skLineSegment(sketch, "E734", {"start": v(-2803.6, 988.27) * mm, "end": v(-2803.6, 671.3) * mm});
            skLineSegment(sketch, "E735", {"start": v(-2803.6, 671.3) * mm, "end": v(-2628.88, 671.3) * mm});
            skLineSegment(sketch, "E736", {"start": v(-2628.88, 671.3) * mm, "end": v(-2628.88, 988.27) * mm});
            skLineSegment(sketch, "E737", {"start": v(-2646.8, 970.35) * mm, "end": v(-2646.8, 896.43) * mm});
            skLineSegment(sketch, "E738", {"start": v(-2646.8, 896.43) * mm, "end": v(-2785.69, 896.43) * mm});
            skLineSegment(sketch, "E739", {"start": v(-2785.69, 896.43) * mm, "end": v(-2785.69, 970.35) * mm});
            skLineSegment(sketch, "E740", {"start": v(-2785.69, 970.35) * mm, "end": v(-2646.8, 970.35) * mm});
            skLineSegment(sketch, "E741", {"start": v(-2785.69, 878.5) * mm, "end": v(-2725.2, 878.5) * mm});
            skLineSegment(sketch, "E742", {"start": v(-2725.2, 878.5) * mm, "end": v(-2725.2, 689.21) * mm});
            skLineSegment(sketch, "E743", {"start": v(-2725.2, 689.21) * mm, "end": v(-2785.69, 689.21) * mm});
            skLineSegment(sketch, "E744", {"start": v(-2785.69, 689.21) * mm, "end": v(-2785.69, 878.5) * mm});
            skLineSegment(sketch, "E745", {"start": v(-2707.28, 689.21) * mm, "end": v(-2707.28, 878.5) * mm});
            skLineSegment(sketch, "E746", {"start": v(-2707.28, 878.5) * mm, "end": v(-2646.8, 878.5) * mm});
            skLineSegment(sketch, "E747", {"start": v(-2646.8, 878.5) * mm, "end": v(-2646.8, 689.21) * mm});
            skLineSegment(sketch, "E748", {"start": v(-2646.8, 689.21) * mm, "end": v(-2707.28, 689.21) * mm});
            skLineSegment(sketch, "E749", {"start": v(-3066.82, -119.48) * mm, "end": v(-3241.56, -119.48) * mm});
            skLineSegment(sketch, "E750", {"start": v(-3241.56, -119.48) * mm, "end": v(-3241.56, -436.46) * mm});
            skLineSegment(sketch, "E751", {"start": v(-3241.56, -436.46) * mm, "end": v(-3066.82, -436.46) * mm});
            skLineSegment(sketch, "E752", {"start": v(-3066.82, -436.46) * mm, "end": v(-3066.82, -119.48) * mm});
            skLineSegment(sketch, "E753", {"start": v(-3084.75, -211.32) * mm, "end": v(-3145.23, -211.32) * mm});
            skLineSegment(sketch, "E754", {"start": v(-3145.23, -211.32) * mm, "end": v(-3145.23, -137.4) * mm});
            skLineSegment(sketch, "E755", {"start": v(-3145.23, -137.4) * mm, "end": v(-3084.75, -137.4) * mm});
            skLineSegment(sketch, "E756", {"start": v(-3084.75, -137.4) * mm, "end": v(-3084.75, -211.32) * mm});
            skLineSegment(sketch, "E757", {"start": v(-3163.15, -137.4) * mm, "end": v(-3163.15, -211.32) * mm});
            skLineSegment(sketch, "E758", {"start": v(-3163.15, -211.32) * mm, "end": v(-3223.63, -211.32) * mm});
            skLineSegment(sketch, "E759", {"start": v(-3223.63, -211.32) * mm, "end": v(-3223.63, -137.4) * mm});
            skLineSegment(sketch, "E760", {"start": v(-3223.63, -137.4) * mm, "end": v(-3163.15, -137.4) * mm});
            skLineSegment(sketch, "E761", {"start": v(-3223.63, -229.24) * mm, "end": v(-3163.15, -229.24) * mm});
            skLineSegment(sketch, "E762", {"start": v(-3163.15, -229.24) * mm, "end": v(-3163.15, -418.53) * mm});
            skLineSegment(sketch, "E763", {"start": v(-3163.15, -418.53) * mm, "end": v(-3223.63, -418.53) * mm});
            skLineSegment(sketch, "E764", {"start": v(-3223.63, -418.53) * mm, "end": v(-3223.63, -229.24) * mm});
            skLineSegment(sketch, "E765", {"start": v(-3145.23, -418.53) * mm, "end": v(-3145.23, -229.24) * mm});
            skLineSegment(sketch, "E766", {"start": v(-3145.23, -229.24) * mm, "end": v(-3084.75, -229.24) * mm});
            skLineSegment(sketch, "E767", {"start": v(-3084.75, -229.24) * mm, "end": v(-3084.75, -418.53) * mm});
            skLineSegment(sketch, "E768", {"start": v(-3084.75, -418.53) * mm, "end": v(-3145.23, -418.53) * mm});
            skLineSegment(sketch, "E769", {"start": v(-1500.97, -434.78) * mm, "end": v(-1500.97, -117.8) * mm});
            skLineSegment(sketch, "E770", {"start": v(-1500.97, -117.8) * mm, "end": v(-1675.7, -117.8) * mm});
            skLineSegment(sketch, "E771", {"start": v(-1675.7, -117.8) * mm, "end": v(-1675.7, -434.78) * mm});
            skLineSegment(sketch, "E772", {"start": v(-1675.7, -434.78) * mm, "end": v(-1500.97, -434.78) * mm});
            skLineSegment(sketch, "E773", {"start": v(-1657.78, -227.56) * mm, "end": v(-1597.3, -227.56) * mm});
            skLineSegment(sketch, "E774", {"start": v(-1597.3, -227.56) * mm, "end": v(-1597.3, -416.85) * mm});
            skLineSegment(sketch, "E775", {"start": v(-1597.3, -416.85) * mm, "end": v(-1657.78, -416.85) * mm});
            skLineSegment(sketch, "E776", {"start": v(-1657.78, -416.85) * mm, "end": v(-1657.78, -227.56) * mm});
            skLineSegment(sketch, "E777", {"start": v(-1579.37, -416.85) * mm, "end": v(-1579.37, -227.56) * mm});
            skLineSegment(sketch, "E778", {"start": v(-1579.37, -227.56) * mm, "end": v(-1518.89, -227.56) * mm});
            skLineSegment(sketch, "E779", {"start": v(-1518.89, -227.56) * mm, "end": v(-1518.89, -416.85) * mm});
            skLineSegment(sketch, "E780", {"start": v(-1518.89, -416.85) * mm, "end": v(-1579.37, -416.85) * mm});
            skLineSegment(sketch, "E781", {"start": v(-1518.89, -209.64) * mm, "end": v(-1579.37, -209.64) * mm});
            skLineSegment(sketch, "E782", {"start": v(-1579.37, -209.64) * mm, "end": v(-1579.37, -135.72) * mm});
            skLineSegment(sketch, "E783", {"start": v(-1579.37, -135.72) * mm, "end": v(-1518.89, -135.72) * mm});
            skLineSegment(sketch, "E784", {"start": v(-1518.89, -135.72) * mm, "end": v(-1518.89, -209.64) * mm});
            skLineSegment(sketch, "E785", {"start": v(-1597.3, -135.72) * mm, "end": v(-1597.3, -209.64) * mm});
            skLineSegment(sketch, "E786", {"start": v(-1597.3, -209.64) * mm, "end": v(-1657.78, -209.64) * mm});
            skLineSegment(sketch, "E787", {"start": v(-1657.78, -209.64) * mm, "end": v(-1657.78, -135.72) * mm});
            skLineSegment(sketch, "E788", {"start": v(-1657.78, -135.72) * mm, "end": v(-1597.3, -135.72) * mm});
            skLineSegment(sketch, "E789", {"start": v(-1935.55, -434.78) * mm, "end": v(-1760.82, -434.78) * mm});
            skLineSegment(sketch, "E790", {"start": v(-1760.82, -434.78) * mm, "end": v(-1760.82, -117.8) * mm});
            skLineSegment(sketch, "E791", {"start": v(-1760.82, -117.8) * mm, "end": v(-1935.55, -117.8) * mm});
            skLineSegment(sketch, "E792", {"start": v(-1935.55, -117.8) * mm, "end": v(-1935.55, -434.78) * mm});
            skLineSegment(sketch, "E793", {"start": v(-1917.63, -227.56) * mm, "end": v(-1857.15, -227.56) * mm});
            skLineSegment(sketch, "E794", {"start": v(-1857.15, -227.56) * mm, "end": v(-1857.15, -416.85) * mm});
            skLineSegment(sketch, "E795", {"start": v(-1857.15, -416.85) * mm, "end": v(-1917.63, -416.85) * mm});
            skLineSegment(sketch, "E796", {"start": v(-1917.63, -416.85) * mm, "end": v(-1917.63, -227.56) * mm});
            skLineSegment(sketch, "E797", {"start": v(-1839.23, -416.85) * mm, "end": v(-1839.23, -227.56) * mm});
            skLineSegment(sketch, "E798", {"start": v(-1839.23, -227.56) * mm, "end": v(-1778.74, -227.56) * mm});
            skLineSegment(sketch, "E799", {"start": v(-1778.74, -227.56) * mm, "end": v(-1778.74, -416.85) * mm});
            skLineSegment(sketch, "E800", {"start": v(-1778.74, -416.85) * mm, "end": v(-1839.23, -416.85) * mm});
            skLineSegment(sketch, "E801", {"start": v(-1778.74, -209.64) * mm, "end": v(-1839.23, -209.64) * mm});
            skLineSegment(sketch, "E802", {"start": v(-1839.23, -209.64) * mm, "end": v(-1839.23, -135.72) * mm});
            skLineSegment(sketch, "E803", {"start": v(-1839.23, -135.72) * mm, "end": v(-1778.74, -135.72) * mm});
            skLineSegment(sketch, "E804", {"start": v(-1778.74, -135.72) * mm, "end": v(-1778.74, -209.64) * mm});
            skLineSegment(sketch, "E805", {"start": v(-1857.15, -135.72) * mm, "end": v(-1857.15, -209.64) * mm});
            skLineSegment(sketch, "E806", {"start": v(-1857.15, -209.64) * mm, "end": v(-1917.63, -209.64) * mm});
            skLineSegment(sketch, "E807", {"start": v(-1917.63, -209.64) * mm, "end": v(-1917.63, -135.72) * mm});
            skLineSegment(sketch, "E808", {"start": v(-1917.63, -135.72) * mm, "end": v(-1857.15, -135.72) * mm});
            skLineSegment(sketch, "E809", {"start": v(-1500.97, 435.52) * mm, "end": v(-1675.7, 435.52) * mm});
            skLineSegment(sketch, "E810", {"start": v(-1675.7, 435.52) * mm, "end": v(-1675.7, 118.54) * mm});
            skLineSegment(sketch, "E811", {"start": v(-1675.7, 118.54) * mm, "end": v(-1500.97, 118.54) * mm});
            skLineSegment(sketch, "E812", {"start": v(-1500.97, 118.54) * mm, "end": v(-1500.97, 435.52) * mm});
            skLineSegment(sketch, "E813", {"start": v(-1518.89, 343.67) * mm, "end": v(-1579.37, 343.67) * mm});
            skLineSegment(sketch, "E814", {"start": v(-1579.37, 343.67) * mm, "end": v(-1579.37, 417.6) * mm});
            skLineSegment(sketch, "E815", {"start": v(-1579.37, 417.6) * mm, "end": v(-1518.89, 417.6) * mm});
            skLineSegment(sketch, "E816", {"start": v(-1518.89, 417.6) * mm, "end": v(-1518.89, 343.67) * mm});
            skLineSegment(sketch, "E817", {"start": v(-1597.3, 417.6) * mm, "end": v(-1597.3, 343.67) * mm});
            skLineSegment(sketch, "E818", {"start": v(-1597.3, 343.67) * mm, "end": v(-1657.78, 343.67) * mm});
            skLineSegment(sketch, "E819", {"start": v(-1657.78, 343.67) * mm, "end": v(-1657.78, 417.6) * mm});
            skLineSegment(sketch, "E820", {"start": v(-1657.78, 417.6) * mm, "end": v(-1597.3, 417.6) * mm});
            skLineSegment(sketch, "E821", {"start": v(-1657.78, 325.75) * mm, "end": v(-1597.3, 325.75) * mm});
            skLineSegment(sketch, "E822", {"start": v(-1597.3, 325.75) * mm, "end": v(-1597.3, 136.46) * mm});
            skLineSegment(sketch, "E823", {"start": v(-1597.3, 136.46) * mm, "end": v(-1657.78, 136.46) * mm});
            skLineSegment(sketch, "E824", {"start": v(-1657.78, 136.46) * mm, "end": v(-1657.78, 325.75) * mm});
            skLineSegment(sketch, "E825", {"start": v(-1579.37, 136.46) * mm, "end": v(-1579.37, 325.75) * mm});
            skLineSegment(sketch, "E826", {"start": v(-1579.37, 325.75) * mm, "end": v(-1518.89, 325.75) * mm});
            skLineSegment(sketch, "E827", {"start": v(-1518.89, 325.75) * mm, "end": v(-1518.89, 136.46) * mm});
            skLineSegment(sketch, "E828", {"start": v(-1518.89, 136.46) * mm, "end": v(-1579.37, 136.46) * mm});
            skLineSegment(sketch, "E829", {"start": v(-2535.91, 435.52) * mm, "end": v(-2535.91, 118.54) * mm});
            skLineSegment(sketch, "E830", {"start": v(-2535.91, 118.54) * mm, "end": v(-2361.18, 118.54) * mm});
            skLineSegment(sketch, "E831", {"start": v(-2361.18, 118.54) * mm, "end": v(-2361.18, 435.52) * mm});
            skLineSegment(sketch, "E832", {"start": v(-2361.18, 435.52) * mm, "end": v(-2535.91, 435.52) * mm});
            skLineSegment(sketch, "E833", {"start": v(-2379.1, 343.67) * mm, "end": v(-2439.59, 343.67) * mm});
            skLineSegment(sketch, "E834", {"start": v(-2439.59, 343.67) * mm, "end": v(-2439.59, 417.6) * mm});
            skLineSegment(sketch, "E835", {"start": v(-2439.59, 417.6) * mm, "end": v(-2379.1, 417.6) * mm});
            skLineSegment(sketch, "E836", {"start": v(-2379.1, 417.6) * mm, "end": v(-2379.1, 343.67) * mm});
            skLineSegment(sketch, "E837", {"start": v(-2457.5, 417.6) * mm, "end": v(-2457.5, 343.67) * mm});
            skLineSegment(sketch, "E838", {"start": v(-2457.5, 343.67) * mm, "end": v(-2518, 343.67) * mm});
            skLineSegment(sketch, "E839", {"start": v(-2518, 343.67) * mm, "end": v(-2518, 417.6) * mm});
            skLineSegment(sketch, "E840", {"start": v(-2518, 417.6) * mm, "end": v(-2457.5, 417.6) * mm});
            skLineSegment(sketch, "E841", {"start": v(-2518, 325.75) * mm, "end": v(-2457.5, 325.75) * mm});
            skLineSegment(sketch, "E842", {"start": v(-2457.5, 325.75) * mm, "end": v(-2457.5, 136.46) * mm});
            skLineSegment(sketch, "E843", {"start": v(-2457.5, 136.46) * mm, "end": v(-2518, 136.46) * mm});
            skLineSegment(sketch, "E844", {"start": v(-2518, 136.46) * mm, "end": v(-2518, 325.75) * mm});
            skLineSegment(sketch, "E845", {"start": v(-2439.59, 136.46) * mm, "end": v(-2439.59, 325.75) * mm});
            skLineSegment(sketch, "E846", {"start": v(-2439.59, 325.75) * mm, "end": v(-2379.1, 325.75) * mm});
            skLineSegment(sketch, "E847", {"start": v(-2379.1, 325.75) * mm, "end": v(-2379.1, 136.46) * mm});
            skLineSegment(sketch, "E848", {"start": v(-2379.1, 136.46) * mm, "end": v(-2439.59, 136.46) * mm});
            skLineSegment(sketch, "E849", {"start": v(-1500.97, 985.47) * mm, "end": v(-1675.7, 985.47) * mm});
            skLineSegment(sketch, "E850", {"start": v(-1675.7, 985.47) * mm, "end": v(-1675.7, 668.5) * mm});
            skLineSegment(sketch, "E851", {"start": v(-1675.7, 668.5) * mm, "end": v(-1500.97, 668.5) * mm});
            skLineSegment(sketch, "E852", {"start": v(-1500.97, 668.5) * mm, "end": v(-1500.97, 985.47) * mm});
            skLineSegment(sketch, "E853", {"start": v(-1518.89, 893.63) * mm, "end": v(-1579.37, 893.63) * mm});
            skLineSegment(sketch, "E854", {"start": v(-1579.37, 893.63) * mm, "end": v(-1579.37, 967.55) * mm});
            skLineSegment(sketch, "E855", {"start": v(-1579.37, 967.55) * mm, "end": v(-1518.89, 967.55) * mm});
            skLineSegment(sketch, "E856", {"start": v(-1518.89, 967.55) * mm, "end": v(-1518.89, 893.63) * mm});
            skLineSegment(sketch, "E857", {"start": v(-1597.3, 967.55) * mm, "end": v(-1597.3, 893.63) * mm});
            skLineSegment(sketch, "E858", {"start": v(-1597.3, 893.63) * mm, "end": v(-1657.78, 893.63) * mm});
            skLineSegment(sketch, "E859", {"start": v(-1657.78, 893.63) * mm, "end": v(-1657.78, 967.55) * mm});
            skLineSegment(sketch, "E860", {"start": v(-1657.78, 967.55) * mm, "end": v(-1597.3, 967.55) * mm});
            skLineSegment(sketch, "E861", {"start": v(-1657.78, 875.7) * mm, "end": v(-1597.3, 875.7) * mm});
            skLineSegment(sketch, "E862", {"start": v(-1597.3, 875.7) * mm, "end": v(-1597.3, 686.41) * mm});
            skLineSegment(sketch, "E863", {"start": v(-1597.3, 686.41) * mm, "end": v(-1657.78, 686.41) * mm});
            skLineSegment(sketch, "E864", {"start": v(-1657.78, 686.41) * mm, "end": v(-1657.78, 875.7) * mm});
            skLineSegment(sketch, "E865", {"start": v(-1579.37, 686.41) * mm, "end": v(-1579.37, 875.7) * mm});
            skLineSegment(sketch, "E866", {"start": v(-1579.37, 875.7) * mm, "end": v(-1518.89, 875.7) * mm});
            skLineSegment(sketch, "E867", {"start": v(-1518.89, 875.7) * mm, "end": v(-1518.89, 686.41) * mm});
            skLineSegment(sketch, "E868", {"start": v(-1518.89, 686.41) * mm, "end": v(-1579.37, 686.41) * mm});
            skLineSegment(sketch, "E869", {"start": v(-1760.82, 985.47) * mm, "end": v(-1935.55, 985.47) * mm});
            skLineSegment(sketch, "E870", {"start": v(-1935.55, 985.47) * mm, "end": v(-1935.55, 668.5) * mm});
            skLineSegment(sketch, "E871", {"start": v(-1935.55, 668.5) * mm, "end": v(-1760.82, 668.5) * mm});
            skLineSegment(sketch, "E872", {"start": v(-1760.82, 668.5) * mm, "end": v(-1760.82, 985.47) * mm});
            skLineSegment(sketch, "E873", {"start": v(-1778.74, 893.63) * mm, "end": v(-1839.23, 893.63) * mm});
            skLineSegment(sketch, "E874", {"start": v(-1839.23, 893.63) * mm, "end": v(-1839.23, 967.55) * mm});
            skLineSegment(sketch, "E875", {"start": v(-1839.23, 967.55) * mm, "end": v(-1778.74, 967.55) * mm});
            skLineSegment(sketch, "E876", {"start": v(-1778.74, 967.55) * mm, "end": v(-1778.74, 893.63) * mm});
            skLineSegment(sketch, "E877", {"start": v(-1857.15, 967.55) * mm, "end": v(-1857.15, 893.63) * mm});
            skLineSegment(sketch, "E878", {"start": v(-1857.15, 893.63) * mm, "end": v(-1917.63, 893.63) * mm});
            skLineSegment(sketch, "E879", {"start": v(-1917.63, 893.63) * mm, "end": v(-1917.63, 967.55) * mm});
            skLineSegment(sketch, "E880", {"start": v(-1917.63, 967.55) * mm, "end": v(-1857.15, 967.55) * mm});
            skLineSegment(sketch, "E881", {"start": v(-1917.63, 875.7) * mm, "end": v(-1857.15, 875.7) * mm});
            skLineSegment(sketch, "E882", {"start": v(-1857.15, 875.7) * mm, "end": v(-1857.15, 686.41) * mm});
            skLineSegment(sketch, "E883", {"start": v(-1857.15, 686.41) * mm, "end": v(-1917.63, 686.41) * mm});
            skLineSegment(sketch, "E884", {"start": v(-1917.63, 686.41) * mm, "end": v(-1917.63, 875.7) * mm});
            skLineSegment(sketch, "E885", {"start": v(-1839.23, 686.41) * mm, "end": v(-1839.23, 875.7) * mm});
            skLineSegment(sketch, "E886", {"start": v(-1839.23, 875.7) * mm, "end": v(-1778.74, 875.7) * mm});
            skLineSegment(sketch, "E887", {"start": v(-1778.74, 875.7) * mm, "end": v(-1778.74, 686.41) * mm});
            skLineSegment(sketch, "E888", {"start": v(-1778.74, 686.41) * mm, "end": v(-1839.23, 686.41) * mm});
            skLineSegment(sketch, "E889", {"start": v(-3241.56, -987.53) * mm, "end": v(-3066.82, -987.53) * mm});
            skLineSegment(sketch, "E890", {"start": v(-3066.82, -987.53) * mm, "end": v(-3066.82, -670.55) * mm});
            skLineSegment(sketch, "E891", {"start": v(-3066.82, -670.55) * mm, "end": v(-3241.56, -670.55) * mm});
            skLineSegment(sketch, "E892", {"start": v(-3241.56, -670.55) * mm, "end": v(-3241.56, -987.53) * mm});
            skLineSegment(sketch, "E893", {"start": v(-3223.63, -780.32) * mm, "end": v(-3163.15, -780.32) * mm});
            skLineSegment(sketch, "E894", {"start": v(-3163.15, -780.32) * mm, "end": v(-3163.15, -969.6) * mm});
            skLineSegment(sketch, "E895", {"start": v(-3163.15, -969.6) * mm, "end": v(-3223.63, -969.6) * mm});
            skLineSegment(sketch, "E896", {"start": v(-3223.63, -969.6) * mm, "end": v(-3223.63, -780.32) * mm});
            skLineSegment(sketch, "E897", {"start": v(-3145.23, -969.6) * mm, "end": v(-3145.23, -780.32) * mm});
            skLineSegment(sketch, "E898", {"start": v(-3145.23, -780.32) * mm, "end": v(-3084.75, -780.32) * mm});
            skLineSegment(sketch, "E899", {"start": v(-3084.75, -780.32) * mm, "end": v(-3084.75, -969.6) * mm});
            skLineSegment(sketch, "E900", {"start": v(-3084.75, -969.6) * mm, "end": v(-3145.23, -969.6) * mm});
            skLineSegment(sketch, "E901", {"start": v(-3084.75, -762.4) * mm, "end": v(-3145.23, -762.4) * mm});
            skLineSegment(sketch, "E902", {"start": v(-3145.23, -762.4) * mm, "end": v(-3145.23, -688.47) * mm});
            skLineSegment(sketch, "E903", {"start": v(-3145.23, -688.47) * mm, "end": v(-3084.75, -688.47) * mm});
            skLineSegment(sketch, "E904", {"start": v(-3084.75, -688.47) * mm, "end": v(-3084.75, -762.4) * mm});
            skLineSegment(sketch, "E905", {"start": v(-3163.15, -688.47) * mm, "end": v(-3163.15, -762.4) * mm});
            skLineSegment(sketch, "E906", {"start": v(-3163.15, -762.4) * mm, "end": v(-3223.63, -762.4) * mm});
            skLineSegment(sketch, "E907", {"start": v(-3223.63, -762.4) * mm, "end": v(-3223.63, -688.47) * mm});
            skLineSegment(sketch, "E908", {"start": v(-3223.63, -688.47) * mm, "end": v(-3163.15, -688.47) * mm});
            skLineSegment(sketch, "E909", {"start": v(-2364.54, -987.53) * mm, "end": v(-2189.81, -987.53) * mm});
            skLineSegment(sketch, "E910", {"start": v(-2189.81, -987.53) * mm, "end": v(-2189.81, -670.55) * mm});
            skLineSegment(sketch, "E911", {"start": v(-2189.81, -670.55) * mm, "end": v(-2364.54, -670.55) * mm});
            skLineSegment(sketch, "E912", {"start": v(-2364.54, -670.55) * mm, "end": v(-2364.54, -987.53) * mm});
            skLineSegment(sketch, "E913", {"start": v(-2346.62, -780.32) * mm, "end": v(-2286.14, -780.32) * mm});
            skLineSegment(sketch, "E914", {"start": v(-2286.14, -780.32) * mm, "end": v(-2286.14, -969.6) * mm});
            skLineSegment(sketch, "E915", {"start": v(-2286.14, -969.6) * mm, "end": v(-2346.62, -969.6) * mm});
            skLineSegment(sketch, "E916", {"start": v(-2346.62, -969.6) * mm, "end": v(-2346.62, -780.32) * mm});
            skLineSegment(sketch, "E917", {"start": v(-2268.22, -969.6) * mm, "end": v(-2268.22, -780.32) * mm});
            skLineSegment(sketch, "E918", {"start": v(-2268.22, -780.32) * mm, "end": v(-2207.73, -780.32) * mm});
            skLineSegment(sketch, "E919", {"start": v(-2207.73, -780.32) * mm, "end": v(-2207.73, -969.6) * mm});
            skLineSegment(sketch, "E920", {"start": v(-2207.73, -969.6) * mm, "end": v(-2268.22, -969.6) * mm});
            skLineSegment(sketch, "E921", {"start": v(-2207.73, -762.4) * mm, "end": v(-2268.22, -762.4) * mm});
            skLineSegment(sketch, "E922", {"start": v(-2268.22, -762.4) * mm, "end": v(-2268.22, -688.47) * mm});
            skLineSegment(sketch, "E923", {"start": v(-2268.22, -688.47) * mm, "end": v(-2207.73, -688.47) * mm});
            skLineSegment(sketch, "E924", {"start": v(-2207.73, -688.47) * mm, "end": v(-2207.73, -762.4) * mm});
            skLineSegment(sketch, "E925", {"start": v(-2286.14, -688.47) * mm, "end": v(-2286.14, -762.4) * mm});
            skLineSegment(sketch, "E926", {"start": v(-2286.14, -762.4) * mm, "end": v(-2346.62, -762.4) * mm});
            skLineSegment(sketch, "E927", {"start": v(-2346.62, -762.4) * mm, "end": v(-2346.62, -688.47) * mm});
            skLineSegment(sketch, "E928", {"start": v(-2346.62, -688.47) * mm, "end": v(-2286.14, -688.47) * mm});
            skLineSegment(sketch, "E929", {"start": v(-1935.55, -987.53) * mm, "end": v(-1760.82, -987.53) * mm});
            skLineSegment(sketch, "E930", {"start": v(-1760.82, -987.53) * mm, "end": v(-1760.82, -670.55) * mm});
            skLineSegment(sketch, "E931", {"start": v(-1760.82, -670.55) * mm, "end": v(-1935.55, -670.55) * mm});
            skLineSegment(sketch, "E932", {"start": v(-1935.55, -670.55) * mm, "end": v(-1935.55, -987.53) * mm});
            skLineSegment(sketch, "E933", {"start": v(-1917.63, -780.32) * mm, "end": v(-1857.15, -780.32) * mm});
            skLineSegment(sketch, "E934", {"start": v(-1857.15, -780.32) * mm, "end": v(-1857.15, -969.6) * mm});
            skLineSegment(sketch, "E935", {"start": v(-1857.15, -969.6) * mm, "end": v(-1917.63, -969.6) * mm});
            skLineSegment(sketch, "E936", {"start": v(-1917.63, -969.6) * mm, "end": v(-1917.63, -780.32) * mm});
            skLineSegment(sketch, "E937", {"start": v(-1839.23, -969.6) * mm, "end": v(-1839.23, -780.32) * mm});
            skLineSegment(sketch, "E938", {"start": v(-1839.23, -780.32) * mm, "end": v(-1778.74, -780.32) * mm});
            skLineSegment(sketch, "E939", {"start": v(-1778.74, -780.32) * mm, "end": v(-1778.74, -969.6) * mm});
            skLineSegment(sketch, "E940", {"start": v(-1778.74, -969.6) * mm, "end": v(-1839.23, -969.6) * mm});
            skLineSegment(sketch, "E941", {"start": v(-1778.74, -762.4) * mm, "end": v(-1839.23, -762.4) * mm});
            skLineSegment(sketch, "E942", {"start": v(-1839.23, -762.4) * mm, "end": v(-1839.23, -688.47) * mm});
            skLineSegment(sketch, "E943", {"start": v(-1839.23, -688.47) * mm, "end": v(-1778.74, -688.47) * mm});
            skLineSegment(sketch, "E944", {"start": v(-1778.74, -688.47) * mm, "end": v(-1778.74, -762.4) * mm});
            skLineSegment(sketch, "E945", {"start": v(-1857.15, -688.47) * mm, "end": v(-1857.15, -762.4) * mm});
            skLineSegment(sketch, "E946", {"start": v(-1857.15, -762.4) * mm, "end": v(-1917.63, -762.4) * mm});
            skLineSegment(sketch, "E947", {"start": v(-1917.63, -762.4) * mm, "end": v(-1917.63, -688.47) * mm});
            skLineSegment(sketch, "E948", {"start": v(-1917.63, -688.47) * mm, "end": v(-1857.15, -688.47) * mm});
            skLineSegment(sketch, "E949", {"start": v(-1675.7, -987.53) * mm, "end": v(-1500.97, -987.53) * mm});
            skLineSegment(sketch, "E950", {"start": v(-1500.97, -987.53) * mm, "end": v(-1500.97, -670.55) * mm});
            skLineSegment(sketch, "E951", {"start": v(-1500.97, -670.55) * mm, "end": v(-1675.7, -670.55) * mm});
            skLineSegment(sketch, "E952", {"start": v(-1675.7, -670.55) * mm, "end": v(-1675.7, -987.53) * mm});
            skLineSegment(sketch, "E953", {"start": v(-1657.78, -780.32) * mm, "end": v(-1597.3, -780.32) * mm});
            skLineSegment(sketch, "E954", {"start": v(-1597.3, -780.32) * mm, "end": v(-1597.3, -969.6) * mm});
            skLineSegment(sketch, "E955", {"start": v(-1597.3, -969.6) * mm, "end": v(-1657.78, -969.6) * mm});
            skLineSegment(sketch, "E956", {"start": v(-1657.78, -969.6) * mm, "end": v(-1657.78, -780.32) * mm});
            skLineSegment(sketch, "E957", {"start": v(-1579.37, -969.6) * mm, "end": v(-1579.37, -780.32) * mm});
            skLineSegment(sketch, "E958", {"start": v(-1579.37, -780.32) * mm, "end": v(-1518.89, -780.32) * mm});
            skLineSegment(sketch, "E959", {"start": v(-1518.89, -780.32) * mm, "end": v(-1518.89, -969.6) * mm});
            skLineSegment(sketch, "E960", {"start": v(-1518.89, -969.6) * mm, "end": v(-1579.37, -969.6) * mm});
            skLineSegment(sketch, "E961", {"start": v(-1518.89, -762.4) * mm, "end": v(-1579.37, -762.4) * mm});
            skLineSegment(sketch, "E962", {"start": v(-1579.37, -762.4) * mm, "end": v(-1579.37, -688.47) * mm});
            skLineSegment(sketch, "E963", {"start": v(-1579.37, -688.47) * mm, "end": v(-1518.89, -688.47) * mm});
            skLineSegment(sketch, "E964", {"start": v(-1518.89, -688.47) * mm, "end": v(-1518.89, -762.4) * mm});
            skLineSegment(sketch, "E965", {"start": v(-1597.3, -688.47) * mm, "end": v(-1597.3, -762.4) * mm});
            skLineSegment(sketch, "E966", {"start": v(-1597.3, -762.4) * mm, "end": v(-1657.78, -762.4) * mm});
            skLineSegment(sketch, "E967", {"start": v(-1657.78, -762.4) * mm, "end": v(-1657.78, -688.47) * mm});
            skLineSegment(sketch, "E968", {"start": v(-1657.78, -688.47) * mm, "end": v(-1597.3, -688.47) * mm});
            skLineSegment(sketch, "E969", {"start": v(-2823.77, 988.27) * mm, "end": v(-2926.82, 988.27) * mm});
            skLineSegment(sketch, "E970", {"start": v(-2926.82, 988.27) * mm, "end": v(-2926.82, 669.8) * mm});
            skLineSegment(sketch, "E971", {"start": v(-2926.82, 669.8) * mm, "end": v(-2823.77, 669.8) * mm});
            skLineSegment(sketch, "E972", {"start": v(-2823.77, 669.8) * mm, "end": v(-2823.77, 988.27) * mm});
            skLineSegment(sketch, "E973", {"start": v(-2841.7, 970.35) * mm, "end": v(-2841.7, 896.43) * mm});
            skLineSegment(sketch, "E974", {"start": v(-2841.7, 896.43) * mm, "end": v(-2908.9, 896.43) * mm});
            skLineSegment(sketch, "E975", {"start": v(-2908.9, 896.43) * mm, "end": v(-2908.9, 970.35) * mm});
            skLineSegment(sketch, "E976", {"start": v(-2908.9, 970.35) * mm, "end": v(-2841.7, 970.35) * mm});
            skLineSegment(sketch, "E977", {"start": v(-2908.9, 687.72) * mm, "end": v(-2908.9, 878.5) * mm});
            skLineSegment(sketch, "E978", {"start": v(-2908.9, 878.5) * mm, "end": v(-2841.7, 878.5) * mm});
            skLineSegment(sketch, "E979", {"start": v(-2841.7, 878.5) * mm, "end": v(-2841.7, 687.72) * mm});
            skLineSegment(sketch, "E980", {"start": v(-2841.7, 687.72) * mm, "end": v(-2908.9, 687.72) * mm});
            skLineSegment(sketch, "E981", {"start": v(-2505.67, 988.27) * mm, "end": v(-2608.72, 988.27) * mm});
            skLineSegment(sketch, "E982", {"start": v(-2608.72, 988.27) * mm, "end": v(-2608.72, 669.8) * mm});
            skLineSegment(sketch, "E983", {"start": v(-2608.72, 669.8) * mm, "end": v(-2505.67, 669.8) * mm});
            skLineSegment(sketch, "E984", {"start": v(-2505.67, 669.8) * mm, "end": v(-2505.67, 988.27) * mm});
            skLineSegment(sketch, "E985", {"start": v(-2523.6, 970.35) * mm, "end": v(-2523.6, 896.43) * mm});
            skLineSegment(sketch, "E986", {"start": v(-2523.6, 896.43) * mm, "end": v(-2590.8, 896.43) * mm});
            skLineSegment(sketch, "E987", {"start": v(-2590.8, 896.43) * mm, "end": v(-2590.8, 970.35) * mm});
            skLineSegment(sketch, "E988", {"start": v(-2590.8, 970.35) * mm, "end": v(-2523.6, 970.35) * mm});
            skLineSegment(sketch, "E989", {"start": v(-2590.8, 687.72) * mm, "end": v(-2590.8, 878.5) * mm});
            skLineSegment(sketch, "E990", {"start": v(-2590.8, 878.5) * mm, "end": v(-2523.6, 878.5) * mm});
            skLineSegment(sketch, "E991", {"start": v(-2523.6, 878.5) * mm, "end": v(-2523.6, 687.72) * mm});
            skLineSegment(sketch, "E992", {"start": v(-2523.6, 687.72) * mm, "end": v(-2590.8, 687.72) * mm});
            skLineSegment(sketch, "E993", {"start": v(-2628.32, -435.7) * mm, "end": v(-2628.32, -118.72) * mm});
            skLineSegment(sketch, "E994", {"start": v(-2628.32, -118.72) * mm, "end": v(-2803.05, -118.72) * mm});
            skLineSegment(sketch, "E995", {"start": v(-2803.05, -118.72) * mm, "end": v(-2803.05, -435.7) * mm});
            skLineSegment(sketch, "E996", {"start": v(-2803.05, -435.7) * mm, "end": v(-2628.32, -435.7) * mm});
            skLineSegment(sketch, "E997", {"start": v(-2785.13, -228.49) * mm, "end": v(-2724.64, -228.49) * mm});
            skLineSegment(sketch, "E998", {"start": v(-2724.64, -228.49) * mm, "end": v(-2724.64, -417.78) * mm});
            skLineSegment(sketch, "E999", {"start": v(-2724.64, -417.78) * mm, "end": v(-2785.13, -417.78) * mm});
            skLineSegment(sketch, "E1000", {"start": v(-2785.13, -417.78) * mm, "end": v(-2785.13, -228.49) * mm});
            skLineSegment(sketch, "E1001", {"start": v(-2706.72, -417.78) * mm, "end": v(-2706.72, -228.49) * mm});
            skLineSegment(sketch, "E1002", {"start": v(-2706.72, -228.49) * mm, "end": v(-2646.24, -228.49) * mm});
            skLineSegment(sketch, "E1003", {"start": v(-2646.24, -228.49) * mm, "end": v(-2646.24, -417.78) * mm});
            skLineSegment(sketch, "E1004", {"start": v(-2646.24, -417.78) * mm, "end": v(-2706.72, -417.78) * mm});
            skLineSegment(sketch, "E1005", {"start": v(-2646.24, -136.64) * mm, "end": v(-2646.24, -210.57) * mm});
            skLineSegment(sketch, "E1006", {"start": v(-2646.24, -210.57) * mm, "end": v(-2785.13, -210.57) * mm});
            skLineSegment(sketch, "E1007", {"start": v(-2785.13, -210.57) * mm, "end": v(-2785.13, -136.64) * mm});
            skLineSegment(sketch, "E1008", {"start": v(-2785.13, -136.64) * mm, "end": v(-2646.24, -136.64) * mm});
            skLineSegment(sketch, "E1009", {"start": v(-2823.2, -437.2) * mm, "end": v(-2823.2, -118.72) * mm});
            skLineSegment(sketch, "E1010", {"start": v(-2823.2, -118.72) * mm, "end": v(-2926.26, -118.72) * mm});
            skLineSegment(sketch, "E1011", {"start": v(-2926.26, -118.72) * mm, "end": v(-2926.26, -437.2) * mm});
            skLineSegment(sketch, "E1012", {"start": v(-2926.26, -437.2) * mm, "end": v(-2823.2, -437.2) * mm});
            skLineSegment(sketch, "E1013", {"start": v(-2908.33, -419.28) * mm, "end": v(-2908.33, -228.49) * mm});
            skLineSegment(sketch, "E1014", {"start": v(-2908.33, -228.49) * mm, "end": v(-2841.13, -228.49) * mm});
            skLineSegment(sketch, "E1015", {"start": v(-2841.13, -228.49) * mm, "end": v(-2841.13, -419.28) * mm});
            skLineSegment(sketch, "E1016", {"start": v(-2841.13, -419.28) * mm, "end": v(-2908.33, -419.28) * mm});
            skLineSegment(sketch, "E1017", {"start": v(-2841.13, -136.64) * mm, "end": v(-2841.13, -210.57) * mm});
            skLineSegment(sketch, "E1018", {"start": v(-2841.13, -210.57) * mm, "end": v(-2908.33, -210.57) * mm});
            skLineSegment(sketch, "E1019", {"start": v(-2908.33, -210.57) * mm, "end": v(-2908.33, -136.64) * mm});
            skLineSegment(sketch, "E1020", {"start": v(-2908.33, -136.64) * mm, "end": v(-2841.13, -136.64) * mm});
            skLineSegment(sketch, "E1021", {"start": v(-2505.1, -437.2) * mm, "end": v(-2505.1, -118.72) * mm});
            skLineSegment(sketch, "E1022", {"start": v(-2505.1, -118.72) * mm, "end": v(-2608.16, -118.72) * mm});
            skLineSegment(sketch, "E1023", {"start": v(-2608.16, -118.72) * mm, "end": v(-2608.16, -437.2) * mm});
            skLineSegment(sketch, "E1024", {"start": v(-2608.16, -437.2) * mm, "end": v(-2505.1, -437.2) * mm});
            skLineSegment(sketch, "E1025", {"start": v(-2590.23, -419.28) * mm, "end": v(-2590.23, -228.49) * mm});
            skLineSegment(sketch, "E1026", {"start": v(-2590.23, -228.49) * mm, "end": v(-2523.03, -228.49) * mm});
            skLineSegment(sketch, "E1027", {"start": v(-2523.03, -228.49) * mm, "end": v(-2523.03, -419.28) * mm});
            skLineSegment(sketch, "E1028", {"start": v(-2523.03, -419.28) * mm, "end": v(-2590.23, -419.28) * mm});
            skLineSegment(sketch, "E1029", {"start": v(-2523.03, -136.64) * mm, "end": v(-2523.03, -210.57) * mm});
            skLineSegment(sketch, "E1030", {"start": v(-2523.03, -210.57) * mm, "end": v(-2590.23, -210.57) * mm});
            skLineSegment(sketch, "E1031", {"start": v(-2590.23, -210.57) * mm, "end": v(-2590.23, -136.64) * mm});
            skLineSegment(sketch, "E1032", {"start": v(-2590.23, -136.64) * mm, "end": v(-2523.03, -136.64) * mm});
            skLineSegment(sketch, "E1033", {"start": v(-2803.6, -986.78) * mm, "end": v(-2628.88, -986.78) * mm});
            skLineSegment(sketch, "E1034", {"start": v(-2628.88, -986.78) * mm, "end": v(-2628.88, -669.8) * mm});
            skLineSegment(sketch, "E1035", {"start": v(-2628.88, -669.8) * mm, "end": v(-2803.6, -669.8) * mm});
            skLineSegment(sketch, "E1036", {"start": v(-2803.6, -669.8) * mm, "end": v(-2803.6, -986.78) * mm});
            skLineSegment(sketch, "E1037", {"start": v(-2785.69, -779.56) * mm, "end": v(-2725.2, -779.56) * mm});
            skLineSegment(sketch, "E1038", {"start": v(-2725.2, -779.56) * mm, "end": v(-2725.2, -968.86) * mm});
            skLineSegment(sketch, "E1039", {"start": v(-2725.2, -968.86) * mm, "end": v(-2785.69, -968.86) * mm});
            skLineSegment(sketch, "E1040", {"start": v(-2785.69, -968.86) * mm, "end": v(-2785.69, -779.56) * mm});
            skLineSegment(sketch, "E1041", {"start": v(-2707.28, -968.86) * mm, "end": v(-2707.28, -779.56) * mm});
            skLineSegment(sketch, "E1042", {"start": v(-2707.28, -779.56) * mm, "end": v(-2646.8, -779.56) * mm});
            skLineSegment(sketch, "E1043", {"start": v(-2646.8, -779.56) * mm, "end": v(-2646.8, -968.86) * mm});
            skLineSegment(sketch, "E1044", {"start": v(-2646.8, -968.86) * mm, "end": v(-2707.28, -968.86) * mm});
            skLineSegment(sketch, "E1045", {"start": v(-2646.8, -687.72) * mm, "end": v(-2646.8, -761.64) * mm});
            skLineSegment(sketch, "E1046", {"start": v(-2646.8, -761.64) * mm, "end": v(-2785.69, -761.64) * mm});
            skLineSegment(sketch, "E1047", {"start": v(-2785.69, -761.64) * mm, "end": v(-2785.69, -687.72) * mm});
            skLineSegment(sketch, "E1048", {"start": v(-2785.69, -687.72) * mm, "end": v(-2646.8, -687.72) * mm});
            skLineSegment(sketch, "E1049", {"start": v(-2926.82, -988.27) * mm, "end": v(-2823.77, -988.27) * mm});
            skLineSegment(sketch, "E1050", {"start": v(-2823.77, -988.27) * mm, "end": v(-2823.77, -669.8) * mm});
            skLineSegment(sketch, "E1051", {"start": v(-2823.77, -669.8) * mm, "end": v(-2926.82, -669.8) * mm});
            skLineSegment(sketch, "E1052", {"start": v(-2926.82, -669.8) * mm, "end": v(-2926.82, -988.27) * mm});
            skLineSegment(sketch, "E1053", {"start": v(-2908.9, -970.35) * mm, "end": v(-2908.9, -779.56) * mm});
            skLineSegment(sketch, "E1054", {"start": v(-2908.9, -779.56) * mm, "end": v(-2841.7, -779.56) * mm});
            skLineSegment(sketch, "E1055", {"start": v(-2841.7, -779.56) * mm, "end": v(-2841.7, -970.35) * mm});
            skLineSegment(sketch, "E1056", {"start": v(-2841.7, -970.35) * mm, "end": v(-2908.9, -970.35) * mm});
            skLineSegment(sketch, "E1057", {"start": v(-2841.7, -687.72) * mm, "end": v(-2841.7, -761.64) * mm});
            skLineSegment(sketch, "E1058", {"start": v(-2841.7, -761.64) * mm, "end": v(-2908.9, -761.64) * mm});
            skLineSegment(sketch, "E1059", {"start": v(-2908.9, -761.64) * mm, "end": v(-2908.9, -687.72) * mm});
            skLineSegment(sketch, "E1060", {"start": v(-2908.9, -687.72) * mm, "end": v(-2841.7, -687.72) * mm});
            skLineSegment(sketch, "E1061", {"start": v(-2608.72, -988.27) * mm, "end": v(-2505.67, -988.27) * mm});
            skLineSegment(sketch, "E1062", {"start": v(-2505.67, -988.27) * mm, "end": v(-2505.67, -669.8) * mm});
            skLineSegment(sketch, "E1063", {"start": v(-2505.67, -669.8) * mm, "end": v(-2608.72, -669.8) * mm});
            skLineSegment(sketch, "E1064", {"start": v(-2608.72, -669.8) * mm, "end": v(-2608.72, -988.27) * mm});
            skLineSegment(sketch, "E1065", {"start": v(-2590.8, -970.35) * mm, "end": v(-2590.8, -779.56) * mm});
            skLineSegment(sketch, "E1066", {"start": v(-2590.8, -779.56) * mm, "end": v(-2523.6, -779.56) * mm});
            skLineSegment(sketch, "E1067", {"start": v(-2523.6, -779.56) * mm, "end": v(-2523.6, -970.35) * mm});
            skLineSegment(sketch, "E1068", {"start": v(-2523.6, -970.35) * mm, "end": v(-2590.8, -970.35) * mm});
            skLineSegment(sketch, "E1069", {"start": v(-2523.6, -687.72) * mm, "end": v(-2523.6, -761.64) * mm});
            skLineSegment(sketch, "E1070", {"start": v(-2523.6, -761.64) * mm, "end": v(-2590.8, -761.64) * mm});
            skLineSegment(sketch, "E1071", {"start": v(-2590.8, -761.64) * mm, "end": v(-2590.8, -687.72) * mm});
            skLineSegment(sketch, "E1072", {"start": v(-2590.8, -687.72) * mm, "end": v(-2523.6, -687.72) * mm});
            skLineSegment(sketch, "E1073", {"start": v(-2005.56, 142.3) * mm, "end": v(-1927.15, 142.3) * mm});
            skLineSegment(sketch, "E1074", {"start": v(-1927.15, 142.3) * mm, "end": v(-1927.15, 433.84) * mm});
            skLineSegment(sketch, "E1075", {"start": v(-1927.15, 433.84) * mm, "end": v(-2101.88, 433.84) * mm});
            skLineSegment(sketch, "E1076", {"start": v(-2101.88, 433.84) * mm, "end": v(-2101.88, 142.3) * mm});
            skLineSegment(sketch, "E1077", {"start": v(-2101.88, 142.3) * mm, "end": v(-2023.48, 142.3) * mm});
            skLineSegment(sketch, "E1078", {"start": v(-2023.48, 142.3) * mm, "end": v(-2005.56, 142.3) * mm});
            skLineSegment(sketch, "E1079", {"start": v(-2005.56, 416.69) * mm, "end": v(-1945.07, 416.69) * mm});
            skLineSegment(sketch, "E1080", {"start": v(-1945.07, 416.69) * mm, "end": v(-1945.07, 345.95) * mm});
            skLineSegment(sketch, "E1081", {"start": v(-1945.07, 345.95) * mm, "end": v(-2005.56, 345.95) * mm});
            skLineSegment(sketch, "E1082", {"start": v(-2005.56, 345.95) * mm, "end": v(-2005.56, 416.69) * mm});
            skLineSegment(sketch, "E1083", {"start": v(-2005.56, 328.8) * mm, "end": v(-1945.07, 328.8) * mm});
            skLineSegment(sketch, "E1084", {"start": v(-1945.07, 328.8) * mm, "end": v(-1945.07, 159.45) * mm});
            skLineSegment(sketch, "E1085", {"start": v(-1945.07, 159.45) * mm, "end": v(-2005.56, 159.45) * mm});
            skLineSegment(sketch, "E1086", {"start": v(-2005.56, 159.45) * mm, "end": v(-2005.56, 328.8) * mm});
            skLineSegment(sketch, "E1087", {"start": v(-2083.96, 416.69) * mm, "end": v(-2023.48, 416.69) * mm});
            skLineSegment(sketch, "E1088", {"start": v(-2023.48, 416.69) * mm, "end": v(-2023.48, 345.95) * mm});
            skLineSegment(sketch, "E1089", {"start": v(-2023.48, 345.95) * mm, "end": v(-2083.96, 345.95) * mm});
            skLineSegment(sketch, "E1090", {"start": v(-2083.96, 345.95) * mm, "end": v(-2083.96, 416.69) * mm});
            skLineSegment(sketch, "E1091", {"start": v(-2083.96, 328.8) * mm, "end": v(-2023.48, 328.8) * mm});
            skLineSegment(sketch, "E1092", {"start": v(-2023.48, 328.8) * mm, "end": v(-2023.48, 159.45) * mm});
            skLineSegment(sketch, "E1093", {"start": v(-2023.48, 159.45) * mm, "end": v(-2083.96, 159.45) * mm});
            skLineSegment(sketch, "E1094", {"start": v(-2083.96, 159.45) * mm, "end": v(-2083.96, 328.8) * mm});
            skLineSegment(sketch, "E1095", {"start": v(-2122.05, 433.84) * mm, "end": v(-2225.1, 433.84) * mm});
            skLineSegment(sketch, "E1096", {"start": v(-2225.1, 433.84) * mm, "end": v(-2225.1, 142.3) * mm});
            skLineSegment(sketch, "E1097", {"start": v(-2225.1, 142.3) * mm, "end": v(-2122.05, 142.3) * mm});
            skLineSegment(sketch, "E1098", {"start": v(-2122.05, 142.3) * mm, "end": v(-2122.05, 433.84) * mm});
            skLineSegment(sketch, "E1099", {"start": v(-2139.97, 416.69) * mm, "end": v(-2139.97, 347.6) * mm});
            skLineSegment(sketch, "E1100", {"start": v(-2139.97, 347.6) * mm, "end": v(-2207.17, 347.6) * mm});
            skLineSegment(sketch, "E1101", {"start": v(-2207.17, 347.6) * mm, "end": v(-2207.17, 416.69) * mm});
            skLineSegment(sketch, "E1102", {"start": v(-2207.17, 416.69) * mm, "end": v(-2139.97, 416.69) * mm});
            skLineSegment(sketch, "E1103", {"start": v(-2207.17, 159.45) * mm, "end": v(-2207.17, 329.67) * mm});
            skLineSegment(sketch, "E1104", {"start": v(-2207.17, 329.67) * mm, "end": v(-2139.97, 329.67) * mm});
            skLineSegment(sketch, "E1105", {"start": v(-2139.97, 329.67) * mm, "end": v(-2139.97, 159.45) * mm});
            skLineSegment(sketch, "E1106", {"start": v(-2139.97, 159.45) * mm, "end": v(-2207.17, 159.45) * mm});
            skLineSegment(sketch, "E1107", {"start": v(-1907, 433.84) * mm, "end": v(-1907, 142.3) * mm});
            skLineSegment(sketch, "E1108", {"start": v(-1907, 142.3) * mm, "end": v(-1803.95, 142.3) * mm});
            skLineSegment(sketch, "E1109", {"start": v(-1803.95, 142.3) * mm, "end": v(-1803.95, 433.84) * mm});
            skLineSegment(sketch, "E1110", {"start": v(-1803.95, 433.84) * mm, "end": v(-1907, 433.84) * mm});
            skLineSegment(sketch, "E1111", {"start": v(-1821.87, 159.45) * mm, "end": v(-1889.07, 159.45) * mm});
            skLineSegment(sketch, "E1112", {"start": v(-1889.07, 159.45) * mm, "end": v(-1889.07, 334.16) * mm});
            skLineSegment(sketch, "E1113", {"start": v(-1889.07, 334.16) * mm, "end": v(-1821.87, 334.16) * mm});
            skLineSegment(sketch, "E1114", {"start": v(-1821.87, 334.16) * mm, "end": v(-1821.87, 159.45) * mm});
            skLineSegment(sketch, "E1115", {"start": v(-1821.87, 351.3) * mm, "end": v(-1889.07, 351.3) * mm});
            skLineSegment(sketch, "E1116", {"start": v(-1889.07, 351.3) * mm, "end": v(-1889.07, 416.69) * mm});
            skLineSegment(sketch, "E1117", {"start": v(-1889.07, 416.69) * mm, "end": v(-1821.87, 416.69) * mm});
            skLineSegment(sketch, "E1118", {"start": v(-1821.87, 416.69) * mm, "end": v(-1821.87, 351.3) * mm});
            skLineSegment(sketch, "E1119", {"start": v(3066.82, 116.86) * mm, "end": v(3241.56, 116.86) * mm});
            skLineSegment(sketch, "E1120", {"start": v(3241.56, 116.86) * mm, "end": v(3241.56, 433.84) * mm});
            skLineSegment(sketch, "E1121", {"start": v(3241.56, 433.84) * mm, "end": v(3066.82, 433.84) * mm});
            skLineSegment(sketch, "E1122", {"start": v(3066.82, 433.84) * mm, "end": v(3066.82, 116.86) * mm});
            skLineSegment(sketch, "E1123", {"start": v(3084.75, 324.07) * mm, "end": v(3145.23, 324.07) * mm});
            skLineSegment(sketch, "E1124", {"start": v(3145.23, 324.07) * mm, "end": v(3145.23, 134.78) * mm});
            skLineSegment(sketch, "E1125", {"start": v(3145.23, 134.78) * mm, "end": v(3084.75, 134.78) * mm});
            skLineSegment(sketch, "E1126", {"start": v(3084.75, 134.78) * mm, "end": v(3084.75, 324.07) * mm});
            skLineSegment(sketch, "E1127", {"start": v(3163.15, 134.78) * mm, "end": v(3163.15, 324.07) * mm});
            skLineSegment(sketch, "E1128", {"start": v(3163.15, 324.07) * mm, "end": v(3223.63, 324.07) * mm});
            skLineSegment(sketch, "E1129", {"start": v(3223.63, 324.07) * mm, "end": v(3223.63, 134.78) * mm});
            skLineSegment(sketch, "E1130", {"start": v(3223.63, 134.78) * mm, "end": v(3163.15, 134.78) * mm});
            skLineSegment(sketch, "E1131", {"start": v(3223.63, 342) * mm, "end": v(3163.15, 342) * mm});
            skLineSegment(sketch, "E1132", {"start": v(3163.15, 342) * mm, "end": v(3163.15, 415.92) * mm});
            skLineSegment(sketch, "E1133", {"start": v(3163.15, 415.92) * mm, "end": v(3223.63, 415.92) * mm});
            skLineSegment(sketch, "E1134", {"start": v(3223.63, 415.92) * mm, "end": v(3223.63, 342) * mm});
            skLineSegment(sketch, "E1135", {"start": v(3145.23, 415.92) * mm, "end": v(3145.23, 342) * mm});
            skLineSegment(sketch, "E1136", {"start": v(3145.23, 342) * mm, "end": v(3084.75, 342) * mm});
            skLineSegment(sketch, "E1137", {"start": v(3084.75, 342) * mm, "end": v(3084.75, 415.92) * mm});
            skLineSegment(sketch, "E1138", {"start": v(3084.75, 415.92) * mm, "end": v(3145.23, 415.92) * mm});
            skLineSegment(sketch, "E1139", {"start": v(3066.82, 988.27) * mm, "end": v(3066.82, 671.3) * mm});
            skLineSegment(sketch, "E1140", {"start": v(3066.82, 671.3) * mm, "end": v(3241.56, 671.3) * mm});
            skLineSegment(sketch, "E1141", {"start": v(3241.56, 671.3) * mm, "end": v(3241.56, 988.27) * mm});
            skLineSegment(sketch, "E1142", {"start": v(3241.56, 988.27) * mm, "end": v(3066.82, 988.27) * mm});
            skLineSegment(sketch, "E1143", {"start": v(3223.63, 896.43) * mm, "end": v(3163.15, 896.43) * mm});
            skLineSegment(sketch, "E1144", {"start": v(3163.15, 896.43) * mm, "end": v(3163.15, 970.35) * mm});
            skLineSegment(sketch, "E1145", {"start": v(3163.15, 970.35) * mm, "end": v(3223.63, 970.35) * mm});
            skLineSegment(sketch, "E1146", {"start": v(3223.63, 970.35) * mm, "end": v(3223.63, 896.43) * mm});
            skLineSegment(sketch, "E1147", {"start": v(3145.23, 970.35) * mm, "end": v(3145.23, 896.43) * mm});
            skLineSegment(sketch, "E1148", {"start": v(3145.23, 896.43) * mm, "end": v(3084.75, 896.43) * mm});
            skLineSegment(sketch, "E1149", {"start": v(3084.75, 896.43) * mm, "end": v(3084.75, 970.35) * mm});
            skLineSegment(sketch, "E1150", {"start": v(3084.75, 970.35) * mm, "end": v(3145.23, 970.35) * mm});
            skLineSegment(sketch, "E1151", {"start": v(3084.75, 878.5) * mm, "end": v(3145.23, 878.5) * mm});
            skLineSegment(sketch, "E1152", {"start": v(3145.23, 878.5) * mm, "end": v(3145.23, 689.21) * mm});
            skLineSegment(sketch, "E1153", {"start": v(3145.23, 689.21) * mm, "end": v(3084.75, 689.21) * mm});
            skLineSegment(sketch, "E1154", {"start": v(3084.75, 689.21) * mm, "end": v(3084.75, 878.5) * mm});
            skLineSegment(sketch, "E1155", {"start": v(3163.15, 689.21) * mm, "end": v(3163.15, 878.5) * mm});
            skLineSegment(sketch, "E1156", {"start": v(3163.15, 878.5) * mm, "end": v(3223.63, 878.5) * mm});
            skLineSegment(sketch, "E1157", {"start": v(3223.63, 878.5) * mm, "end": v(3223.63, 689.21) * mm});
            skLineSegment(sketch, "E1158", {"start": v(3223.63, 689.21) * mm, "end": v(3163.15, 689.21) * mm});
            skLineSegment(sketch, "E1159", {"start": v(2789.05, 116.86) * mm, "end": v(2963.78, 116.86) * mm});
            skLineSegment(sketch, "E1160", {"start": v(2963.78, 116.86) * mm, "end": v(2963.78, 433.84) * mm});
            skLineSegment(sketch, "E1161", {"start": v(2963.78, 433.84) * mm, "end": v(2789.05, 433.84) * mm});
            skLineSegment(sketch, "E1162", {"start": v(2789.05, 433.84) * mm, "end": v(2789.05, 116.86) * mm});
            skLineSegment(sketch, "E1163", {"start": v(2806.97, 324.07) * mm, "end": v(2867.45, 324.07) * mm});
            skLineSegment(sketch, "E1164", {"start": v(2867.45, 324.07) * mm, "end": v(2867.45, 134.78) * mm});
            skLineSegment(sketch, "E1165", {"start": v(2867.45, 134.78) * mm, "end": v(2806.97, 134.78) * mm});
            skLineSegment(sketch, "E1166", {"start": v(2806.97, 134.78) * mm, "end": v(2806.97, 324.07) * mm});
            skLineSegment(sketch, "E1167", {"start": v(2885.37, 134.78) * mm, "end": v(2885.37, 324.07) * mm});
            skLineSegment(sketch, "E1168", {"start": v(2885.37, 324.07) * mm, "end": v(2945.86, 324.07) * mm});
            skLineSegment(sketch, "E1169", {"start": v(2945.86, 324.07) * mm, "end": v(2945.86, 134.78) * mm});
            skLineSegment(sketch, "E1170", {"start": v(2945.86, 134.78) * mm, "end": v(2885.37, 134.78) * mm});
            skLineSegment(sketch, "E1171", {"start": v(2945.86, 342) * mm, "end": v(2885.37, 342) * mm});
            skLineSegment(sketch, "E1172", {"start": v(2885.37, 342) * mm, "end": v(2885.37, 415.92) * mm});
            skLineSegment(sketch, "E1173", {"start": v(2885.37, 415.92) * mm, "end": v(2945.86, 415.92) * mm});
            skLineSegment(sketch, "E1174", {"start": v(2945.86, 415.92) * mm, "end": v(2945.86, 342) * mm});
            skLineSegment(sketch, "E1175", {"start": v(2867.45, 415.92) * mm, "end": v(2867.45, 342) * mm});
            skLineSegment(sketch, "E1176", {"start": v(2867.45, 342) * mm, "end": v(2806.97, 342) * mm});
            skLineSegment(sketch, "E1177", {"start": v(2806.97, 342) * mm, "end": v(2806.97, 415.92) * mm});
            skLineSegment(sketch, "E1178", {"start": v(2806.97, 415.92) * mm, "end": v(2867.45, 415.92) * mm});
            skLineSegment(sketch, "E1179", {"start": v(2188.7, -436.46) * mm, "end": v(2363.42, -436.46) * mm});
            skLineSegment(sketch, "E1180", {"start": v(2363.42, -436.46) * mm, "end": v(2363.42, -119.48) * mm});
            skLineSegment(sketch, "E1181", {"start": v(2363.42, -119.48) * mm, "end": v(2188.7, -119.48) * mm});
            skLineSegment(sketch, "E1182", {"start": v(2188.7, -119.48) * mm, "end": v(2188.7, -436.46) * mm});
            skLineSegment(sketch, "E1183", {"start": v(2206.61, -229.24) * mm, "end": v(2267.1, -229.24) * mm});
            skLineSegment(sketch, "E1184", {"start": v(2267.1, -229.24) * mm, "end": v(2267.1, -418.53) * mm});
            skLineSegment(sketch, "E1185", {"start": v(2267.1, -418.53) * mm, "end": v(2206.61, -418.53) * mm});
            skLineSegment(sketch, "E1186", {"start": v(2206.61, -418.53) * mm, "end": v(2206.61, -229.24) * mm});
            skLineSegment(sketch, "E1187", {"start": v(2285.02, -418.53) * mm, "end": v(2285.02, -229.24) * mm});
            skLineSegment(sketch, "E1188", {"start": v(2285.02, -229.24) * mm, "end": v(2345.5, -229.24) * mm});
            skLineSegment(sketch, "E1189", {"start": v(2345.5, -229.24) * mm, "end": v(2345.5, -418.53) * mm});
            skLineSegment(sketch, "E1190", {"start": v(2345.5, -418.53) * mm, "end": v(2285.02, -418.53) * mm});
            skLineSegment(sketch, "E1191", {"start": v(2345.5, -211.32) * mm, "end": v(2285.02, -211.32) * mm});
            skLineSegment(sketch, "E1192", {"start": v(2285.02, -211.32) * mm, "end": v(2285.02, -137.4) * mm});
            skLineSegment(sketch, "E1193", {"start": v(2285.02, -137.4) * mm, "end": v(2345.5, -137.4) * mm});
            skLineSegment(sketch, "E1194", {"start": v(2345.5, -137.4) * mm, "end": v(2345.5, -211.32) * mm});
            skLineSegment(sketch, "E1195", {"start": v(2267.1, -137.4) * mm, "end": v(2267.1, -211.32) * mm});
            skLineSegment(sketch, "E1196", {"start": v(2267.1, -211.32) * mm, "end": v(2206.61, -211.32) * mm});
            skLineSegment(sketch, "E1197", {"start": v(2206.61, -211.32) * mm, "end": v(2206.61, -137.4) * mm});
            skLineSegment(sketch, "E1198", {"start": v(2206.61, -137.4) * mm, "end": v(2267.1, -137.4) * mm});
            skLineSegment(sketch, "E1199", {"start": v(2363.42, 988.27) * mm, "end": v(2188.7, 988.27) * mm});
            skLineSegment(sketch, "E1200", {"start": v(2188.7, 988.27) * mm, "end": v(2188.7, 671.3) * mm});
            skLineSegment(sketch, "E1201", {"start": v(2188.7, 671.3) * mm, "end": v(2363.42, 671.3) * mm});
            skLineSegment(sketch, "E1202", {"start": v(2363.42, 671.3) * mm, "end": v(2363.42, 988.27) * mm});
            skLineSegment(sketch, "E1203", {"start": v(2345.5, 896.43) * mm, "end": v(2285.02, 896.43) * mm});
            skLineSegment(sketch, "E1204", {"start": v(2285.02, 896.43) * mm, "end": v(2285.02, 970.35) * mm});
            skLineSegment(sketch, "E1205", {"start": v(2285.02, 970.35) * mm, "end": v(2345.5, 970.35) * mm});
            skLineSegment(sketch, "E1206", {"start": v(2345.5, 970.35) * mm, "end": v(2345.5, 896.43) * mm});
            skLineSegment(sketch, "E1207", {"start": v(2267.1, 970.35) * mm, "end": v(2267.1, 896.43) * mm});
            skLineSegment(sketch, "E1208", {"start": v(2267.1, 896.43) * mm, "end": v(2206.61, 896.43) * mm});
            skLineSegment(sketch, "E1209", {"start": v(2206.61, 896.43) * mm, "end": v(2206.61, 970.35) * mm});
            skLineSegment(sketch, "E1210", {"start": v(2206.61, 970.35) * mm, "end": v(2267.1, 970.35) * mm});
            skLineSegment(sketch, "E1211", {"start": v(2206.61, 878.5) * mm, "end": v(2267.1, 878.5) * mm});
            skLineSegment(sketch, "E1212", {"start": v(2267.1, 878.5) * mm, "end": v(2267.1, 689.21) * mm});
            skLineSegment(sketch, "E1213", {"start": v(2267.1, 689.21) * mm, "end": v(2206.61, 689.21) * mm});
            skLineSegment(sketch, "E1214", {"start": v(2206.61, 689.21) * mm, "end": v(2206.61, 878.5) * mm});
            skLineSegment(sketch, "E1215", {"start": v(2285.02, 689.21) * mm, "end": v(2285.02, 878.5) * mm});
            skLineSegment(sketch, "E1216", {"start": v(2285.02, 878.5) * mm, "end": v(2345.5, 878.5) * mm});
            skLineSegment(sketch, "E1217", {"start": v(2345.5, 878.5) * mm, "end": v(2345.5, 689.21) * mm});
            skLineSegment(sketch, "E1218", {"start": v(2345.5, 689.21) * mm, "end": v(2285.02, 689.21) * mm});
            skLineSegment(sketch, "E1219", {"start": v(2803.6, 988.27) * mm, "end": v(2628.88, 988.27) * mm});
            skLineSegment(sketch, "E1220", {"start": v(2628.88, 988.27) * mm, "end": v(2628.88, 671.3) * mm});
            skLineSegment(sketch, "E1221", {"start": v(2628.88, 671.3) * mm, "end": v(2803.6, 671.3) * mm});
            skLineSegment(sketch, "E1222", {"start": v(2803.6, 671.3) * mm, "end": v(2803.6, 988.27) * mm});
            skLineSegment(sketch, "E1223", {"start": v(2785.69, 970.35) * mm, "end": v(2785.69, 896.43) * mm});
            skLineSegment(sketch, "E1224", {"start": v(2785.69, 896.43) * mm, "end": v(2646.8, 896.43) * mm});
            skLineSegment(sketch, "E1225", {"start": v(2646.8, 896.43) * mm, "end": v(2646.8, 970.35) * mm});
            skLineSegment(sketch, "E1226", {"start": v(2646.8, 970.35) * mm, "end": v(2785.69, 970.35) * mm});
            skLineSegment(sketch, "E1227", {"start": v(2646.8, 878.5) * mm, "end": v(2707.28, 878.5) * mm});
            skLineSegment(sketch, "E1228", {"start": v(2707.28, 878.5) * mm, "end": v(2707.28, 689.21) * mm});
            skLineSegment(sketch, "E1229", {"start": v(2707.28, 689.21) * mm, "end": v(2646.8, 689.21) * mm});
            skLineSegment(sketch, "E1230", {"start": v(2646.8, 689.21) * mm, "end": v(2646.8, 878.5) * mm});
            skLineSegment(sketch, "E1231", {"start": v(2725.2, 689.21) * mm, "end": v(2725.2, 878.5) * mm});
            skLineSegment(sketch, "E1232", {"start": v(2725.2, 878.5) * mm, "end": v(2785.69, 878.5) * mm});
            skLineSegment(sketch, "E1233", {"start": v(2785.69, 878.5) * mm, "end": v(2785.69, 689.21) * mm});
            skLineSegment(sketch, "E1234", {"start": v(2785.69, 689.21) * mm, "end": v(2725.2, 689.21) * mm});
            skLineSegment(sketch, "E1235", {"start": v(3066.82, -436.46) * mm, "end": v(3241.56, -436.46) * mm});
            skLineSegment(sketch, "E1236", {"start": v(3241.56, -436.46) * mm, "end": v(3241.56, -119.48) * mm});
            skLineSegment(sketch, "E1237", {"start": v(3241.56, -119.48) * mm, "end": v(3066.82, -119.48) * mm});
            skLineSegment(sketch, "E1238", {"start": v(3066.82, -119.48) * mm, "end": v(3066.82, -436.46) * mm});
            skLineSegment(sketch, "E1239", {"start": v(3084.75, -229.24) * mm, "end": v(3145.23, -229.24) * mm});
            skLineSegment(sketch, "E1240", {"start": v(3145.23, -229.24) * mm, "end": v(3145.23, -418.53) * mm});
            skLineSegment(sketch, "E1241", {"start": v(3145.23, -418.53) * mm, "end": v(3084.75, -418.53) * mm});
            skLineSegment(sketch, "E1242", {"start": v(3084.75, -418.53) * mm, "end": v(3084.75, -229.24) * mm});
            skLineSegment(sketch, "E1243", {"start": v(3163.15, -418.53) * mm, "end": v(3163.15, -229.24) * mm});
            skLineSegment(sketch, "E1244", {"start": v(3163.15, -229.24) * mm, "end": v(3223.63, -229.24) * mm});
            skLineSegment(sketch, "E1245", {"start": v(3223.63, -229.24) * mm, "end": v(3223.63, -418.53) * mm});
            skLineSegment(sketch, "E1246", {"start": v(3223.63, -418.53) * mm, "end": v(3163.15, -418.53) * mm});
            skLineSegment(sketch, "E1247", {"start": v(3223.63, -211.32) * mm, "end": v(3163.15, -211.32) * mm});
            skLineSegment(sketch, "E1248", {"start": v(3163.15, -211.32) * mm, "end": v(3163.15, -137.4) * mm});
            skLineSegment(sketch, "E1249", {"start": v(3163.15, -137.4) * mm, "end": v(3223.63, -137.4) * mm});
            skLineSegment(sketch, "E1250", {"start": v(3223.63, -137.4) * mm, "end": v(3223.63, -211.32) * mm});
            skLineSegment(sketch, "E1251", {"start": v(3145.23, -137.4) * mm, "end": v(3145.23, -211.32) * mm});
            skLineSegment(sketch, "E1252", {"start": v(3145.23, -211.32) * mm, "end": v(3084.75, -211.32) * mm});
            skLineSegment(sketch, "E1253", {"start": v(3084.75, -211.32) * mm, "end": v(3084.75, -137.4) * mm});
            skLineSegment(sketch, "E1254", {"start": v(3084.75, -137.4) * mm, "end": v(3145.23, -137.4) * mm});
            skLineSegment(sketch, "E1255", {"start": v(1675.7, -434.78) * mm, "end": v(1675.7, -117.8) * mm});
            skLineSegment(sketch, "E1256", {"start": v(1675.7, -117.8) * mm, "end": v(1500.97, -117.8) * mm});
            skLineSegment(sketch, "E1257", {"start": v(1500.97, -117.8) * mm, "end": v(1500.97, -434.78) * mm});
            skLineSegment(sketch, "E1258", {"start": v(1500.97, -434.78) * mm, "end": v(1675.7, -434.78) * mm});
            skLineSegment(sketch, "E1259", {"start": v(1518.89, -227.56) * mm, "end": v(1579.37, -227.56) * mm});
            skLineSegment(sketch, "E1260", {"start": v(1579.37, -227.56) * mm, "end": v(1579.37, -416.85) * mm});
            skLineSegment(sketch, "E1261", {"start": v(1579.37, -416.85) * mm, "end": v(1518.89, -416.85) * mm});
            skLineSegment(sketch, "E1262", {"start": v(1518.89, -416.85) * mm, "end": v(1518.89, -227.56) * mm});
            skLineSegment(sketch, "E1263", {"start": v(1597.3, -416.85) * mm, "end": v(1597.3, -227.56) * mm});
            skLineSegment(sketch, "E1264", {"start": v(1597.3, -227.56) * mm, "end": v(1657.78, -227.56) * mm});
            skLineSegment(sketch, "E1265", {"start": v(1657.78, -227.56) * mm, "end": v(1657.78, -416.85) * mm});
            skLineSegment(sketch, "E1266", {"start": v(1657.78, -416.85) * mm, "end": v(1597.3, -416.85) * mm});
            skLineSegment(sketch, "E1267", {"start": v(1657.78, -209.64) * mm, "end": v(1597.3, -209.64) * mm});
            skLineSegment(sketch, "E1268", {"start": v(1597.3, -209.64) * mm, "end": v(1597.3, -135.72) * mm});
            skLineSegment(sketch, "E1269", {"start": v(1597.3, -135.72) * mm, "end": v(1657.78, -135.72) * mm});
            skLineSegment(sketch, "E1270", {"start": v(1657.78, -135.72) * mm, "end": v(1657.78, -209.64) * mm});
            skLineSegment(sketch, "E1271", {"start": v(1579.37, -135.72) * mm, "end": v(1579.37, -209.64) * mm});
            skLineSegment(sketch, "E1272", {"start": v(1579.37, -209.64) * mm, "end": v(1518.89, -209.64) * mm});
            skLineSegment(sketch, "E1273", {"start": v(1518.89, -209.64) * mm, "end": v(1518.89, -135.72) * mm});
            skLineSegment(sketch, "E1274", {"start": v(1518.89, -135.72) * mm, "end": v(1579.37, -135.72) * mm});
            skLineSegment(sketch, "E1275", {"start": v(1760.82, -434.78) * mm, "end": v(1935.55, -434.78) * mm});
            skLineSegment(sketch, "E1276", {"start": v(1935.55, -434.78) * mm, "end": v(1935.55, -117.8) * mm});
            skLineSegment(sketch, "E1277", {"start": v(1935.55, -117.8) * mm, "end": v(1760.82, -117.8) * mm});
            skLineSegment(sketch, "E1278", {"start": v(1760.82, -117.8) * mm, "end": v(1760.82, -434.78) * mm});
            skLineSegment(sketch, "E1279", {"start": v(1778.74, -227.56) * mm, "end": v(1839.23, -227.56) * mm});
            skLineSegment(sketch, "E1280", {"start": v(1839.23, -227.56) * mm, "end": v(1839.23, -416.85) * mm});
            skLineSegment(sketch, "E1281", {"start": v(1839.23, -416.85) * mm, "end": v(1778.74, -416.85) * mm});
            skLineSegment(sketch, "E1282", {"start": v(1778.74, -416.85) * mm, "end": v(1778.74, -227.56) * mm});
            skLineSegment(sketch, "E1283", {"start": v(1857.15, -416.85) * mm, "end": v(1857.15, -227.56) * mm});
            skLineSegment(sketch, "E1284", {"start": v(1857.15, -227.56) * mm, "end": v(1917.63, -227.56) * mm});
            skLineSegment(sketch, "E1285", {"start": v(1917.63, -227.56) * mm, "end": v(1917.63, -416.85) * mm});
            skLineSegment(sketch, "E1286", {"start": v(1917.63, -416.85) * mm, "end": v(1857.15, -416.85) * mm});
            skLineSegment(sketch, "E1287", {"start": v(1917.63, -209.64) * mm, "end": v(1857.15, -209.64) * mm});
            skLineSegment(sketch, "E1288", {"start": v(1857.15, -209.64) * mm, "end": v(1857.15, -135.72) * mm});
            skLineSegment(sketch, "E1289", {"start": v(1857.15, -135.72) * mm, "end": v(1917.63, -135.72) * mm});
            skLineSegment(sketch, "E1290", {"start": v(1917.63, -135.72) * mm, "end": v(1917.63, -209.64) * mm});
            skLineSegment(sketch, "E1291", {"start": v(1839.23, -135.72) * mm, "end": v(1839.23, -209.64) * mm});
            skLineSegment(sketch, "E1292", {"start": v(1839.23, -209.64) * mm, "end": v(1778.74, -209.64) * mm});
            skLineSegment(sketch, "E1293", {"start": v(1778.74, -209.64) * mm, "end": v(1778.74, -135.72) * mm});
            skLineSegment(sketch, "E1294", {"start": v(1778.74, -135.72) * mm, "end": v(1839.23, -135.72) * mm});
            skLineSegment(sketch, "E1295", {"start": v(1675.7, 435.52) * mm, "end": v(1500.97, 435.52) * mm});
            skLineSegment(sketch, "E1296", {"start": v(1500.97, 435.52) * mm, "end": v(1500.97, 118.54) * mm});
            skLineSegment(sketch, "E1297", {"start": v(1500.97, 118.54) * mm, "end": v(1675.7, 118.54) * mm});
            skLineSegment(sketch, "E1298", {"start": v(1675.7, 118.54) * mm, "end": v(1675.7, 435.52) * mm});
            skLineSegment(sketch, "E1299", {"start": v(1657.78, 343.67) * mm, "end": v(1597.3, 343.67) * mm});
            skLineSegment(sketch, "E1300", {"start": v(1597.3, 343.67) * mm, "end": v(1597.3, 417.6) * mm});
            skLineSegment(sketch, "E1301", {"start": v(1597.3, 417.6) * mm, "end": v(1657.78, 417.6) * mm});
            skLineSegment(sketch, "E1302", {"start": v(1657.78, 417.6) * mm, "end": v(1657.78, 343.67) * mm});
            skLineSegment(sketch, "E1303", {"start": v(1579.37, 417.6) * mm, "end": v(1579.37, 343.67) * mm});
            skLineSegment(sketch, "E1304", {"start": v(1579.37, 343.67) * mm, "end": v(1518.89, 343.67) * mm});
            skLineSegment(sketch, "E1305", {"start": v(1518.89, 343.67) * mm, "end": v(1518.89, 417.6) * mm});
            skLineSegment(sketch, "E1306", {"start": v(1518.89, 417.6) * mm, "end": v(1579.37, 417.6) * mm});
            skLineSegment(sketch, "E1307", {"start": v(1518.89, 325.75) * mm, "end": v(1579.37, 325.75) * mm});
            skLineSegment(sketch, "E1308", {"start": v(1579.37, 325.75) * mm, "end": v(1579.37, 136.46) * mm});
            skLineSegment(sketch, "E1309", {"start": v(1579.37, 136.46) * mm, "end": v(1518.89, 136.46) * mm});
            skLineSegment(sketch, "E1310", {"start": v(1518.89, 136.46) * mm, "end": v(1518.89, 325.75) * mm});
            skLineSegment(sketch, "E1311", {"start": v(1597.3, 136.46) * mm, "end": v(1597.3, 325.75) * mm});
            skLineSegment(sketch, "E1312", {"start": v(1597.3, 325.75) * mm, "end": v(1657.78, 325.75) * mm});
            skLineSegment(sketch, "E1313", {"start": v(1657.78, 325.75) * mm, "end": v(1657.78, 136.46) * mm});
            skLineSegment(sketch, "E1314", {"start": v(1657.78, 136.46) * mm, "end": v(1597.3, 136.46) * mm});
            skLineSegment(sketch, "E1315", {"start": v(2361.18, 435.52) * mm, "end": v(2361.18, 118.54) * mm});
            skLineSegment(sketch, "E1316", {"start": v(2361.18, 118.54) * mm, "end": v(2535.91, 118.54) * mm});
            skLineSegment(sketch, "E1317", {"start": v(2535.91, 118.54) * mm, "end": v(2535.91, 435.52) * mm});
            skLineSegment(sketch, "E1318", {"start": v(2535.91, 435.52) * mm, "end": v(2361.18, 435.52) * mm});
            skLineSegment(sketch, "E1319", {"start": v(2518, 343.67) * mm, "end": v(2457.5, 343.67) * mm});
            skLineSegment(sketch, "E1320", {"start": v(2457.5, 343.67) * mm, "end": v(2457.5, 417.6) * mm});
            skLineSegment(sketch, "E1321", {"start": v(2457.5, 417.6) * mm, "end": v(2518, 417.6) * mm});
            skLineSegment(sketch, "E1322", {"start": v(2518, 417.6) * mm, "end": v(2518, 343.67) * mm});
            skLineSegment(sketch, "E1323", {"start": v(2439.59, 417.6) * mm, "end": v(2439.59, 343.67) * mm});
            skLineSegment(sketch, "E1324", {"start": v(2439.59, 343.67) * mm, "end": v(2379.1, 343.67) * mm});
            skLineSegment(sketch, "E1325", {"start": v(2379.1, 343.67) * mm, "end": v(2379.1, 417.6) * mm});
            skLineSegment(sketch, "E1326", {"start": v(2379.1, 417.6) * mm, "end": v(2439.59, 417.6) * mm});
            skLineSegment(sketch, "E1327", {"start": v(2379.1, 325.75) * mm, "end": v(2439.59, 325.75) * mm});
            skLineSegment(sketch, "E1328", {"start": v(2439.59, 325.75) * mm, "end": v(2439.59, 136.46) * mm});
            skLineSegment(sketch, "E1329", {"start": v(2439.59, 136.46) * mm, "end": v(2379.1, 136.46) * mm});
            skLineSegment(sketch, "E1330", {"start": v(2379.1, 136.46) * mm, "end": v(2379.1, 325.75) * mm});
            skLineSegment(sketch, "E1331", {"start": v(2457.5, 136.46) * mm, "end": v(2457.5, 325.75) * mm});
            skLineSegment(sketch, "E1332", {"start": v(2457.5, 325.75) * mm, "end": v(2518, 325.75) * mm});
            skLineSegment(sketch, "E1333", {"start": v(2518, 325.75) * mm, "end": v(2518, 136.46) * mm});
            skLineSegment(sketch, "E1334", {"start": v(2518, 136.46) * mm, "end": v(2457.5, 136.46) * mm});
            skLineSegment(sketch, "E1335", {"start": v(1675.7, 985.47) * mm, "end": v(1500.97, 985.47) * mm});
            skLineSegment(sketch, "E1336", {"start": v(1500.97, 985.47) * mm, "end": v(1500.97, 668.5) * mm});
            skLineSegment(sketch, "E1337", {"start": v(1500.97, 668.5) * mm, "end": v(1675.7, 668.5) * mm});
            skLineSegment(sketch, "E1338", {"start": v(1675.7, 668.5) * mm, "end": v(1675.7, 985.47) * mm});
            skLineSegment(sketch, "E1339", {"start": v(1657.78, 893.63) * mm, "end": v(1597.3, 893.63) * mm});
            skLineSegment(sketch, "E1340", {"start": v(1597.3, 893.63) * mm, "end": v(1597.3, 967.55) * mm});
            skLineSegment(sketch, "E1341", {"start": v(1597.3, 967.55) * mm, "end": v(1657.78, 967.55) * mm});
            skLineSegment(sketch, "E1342", {"start": v(1657.78, 967.55) * mm, "end": v(1657.78, 893.63) * mm});
            skLineSegment(sketch, "E1343", {"start": v(1579.37, 967.55) * mm, "end": v(1579.37, 893.63) * mm});
            skLineSegment(sketch, "E1344", {"start": v(1579.37, 893.63) * mm, "end": v(1518.89, 893.63) * mm});
            skLineSegment(sketch, "E1345", {"start": v(1518.89, 893.63) * mm, "end": v(1518.89, 967.55) * mm});
            skLineSegment(sketch, "E1346", {"start": v(1518.89, 967.55) * mm, "end": v(1579.37, 967.55) * mm});
            skLineSegment(sketch, "E1347", {"start": v(1518.89, 875.7) * mm, "end": v(1579.37, 875.7) * mm});
            skLineSegment(sketch, "E1348", {"start": v(1579.37, 875.7) * mm, "end": v(1579.37, 686.41) * mm});
            skLineSegment(sketch, "E1349", {"start": v(1579.37, 686.41) * mm, "end": v(1518.89, 686.41) * mm});
            skLineSegment(sketch, "E1350", {"start": v(1518.89, 686.41) * mm, "end": v(1518.89, 875.7) * mm});
            skLineSegment(sketch, "E1351", {"start": v(1597.3, 686.41) * mm, "end": v(1597.3, 875.7) * mm});
            skLineSegment(sketch, "E1352", {"start": v(1597.3, 875.7) * mm, "end": v(1657.78, 875.7) * mm});
            skLineSegment(sketch, "E1353", {"start": v(1657.78, 875.7) * mm, "end": v(1657.78, 686.41) * mm});
            skLineSegment(sketch, "E1354", {"start": v(1657.78, 686.41) * mm, "end": v(1597.3, 686.41) * mm});
            skLineSegment(sketch, "E1355", {"start": v(1935.55, 985.47) * mm, "end": v(1760.82, 985.47) * mm});
            skLineSegment(sketch, "E1356", {"start": v(1760.82, 985.47) * mm, "end": v(1760.82, 668.5) * mm});
            skLineSegment(sketch, "E1357", {"start": v(1760.82, 668.5) * mm, "end": v(1935.55, 668.5) * mm});
            skLineSegment(sketch, "E1358", {"start": v(1935.55, 668.5) * mm, "end": v(1935.55, 985.47) * mm});
            skLineSegment(sketch, "E1359", {"start": v(1917.63, 893.63) * mm, "end": v(1857.15, 893.63) * mm});
            skLineSegment(sketch, "E1360", {"start": v(1857.15, 893.63) * mm, "end": v(1857.15, 967.55) * mm});
            skLineSegment(sketch, "E1361", {"start": v(1857.15, 967.55) * mm, "end": v(1917.63, 967.55) * mm});
            skLineSegment(sketch, "E1362", {"start": v(1917.63, 967.55) * mm, "end": v(1917.63, 893.63) * mm});
            skLineSegment(sketch, "E1363", {"start": v(1839.23, 967.55) * mm, "end": v(1839.23, 893.63) * mm});
            skLineSegment(sketch, "E1364", {"start": v(1839.23, 893.63) * mm, "end": v(1778.74, 893.63) * mm});
            skLineSegment(sketch, "E1365", {"start": v(1778.74, 893.63) * mm, "end": v(1778.74, 967.55) * mm});
            skLineSegment(sketch, "E1366", {"start": v(1778.74, 967.55) * mm, "end": v(1839.23, 967.55) * mm});
            skLineSegment(sketch, "E1367", {"start": v(1778.74, 875.7) * mm, "end": v(1839.23, 875.7) * mm});
            skLineSegment(sketch, "E1368", {"start": v(1839.23, 875.7) * mm, "end": v(1839.23, 686.41) * mm});
            skLineSegment(sketch, "E1369", {"start": v(1839.23, 686.41) * mm, "end": v(1778.74, 686.41) * mm});
            skLineSegment(sketch, "E1370", {"start": v(1778.74, 686.41) * mm, "end": v(1778.74, 875.7) * mm});
            skLineSegment(sketch, "E1371", {"start": v(1857.15, 686.41) * mm, "end": v(1857.15, 875.7) * mm});
            skLineSegment(sketch, "E1372", {"start": v(1857.15, 875.7) * mm, "end": v(1917.63, 875.7) * mm});
            skLineSegment(sketch, "E1373", {"start": v(1917.63, 875.7) * mm, "end": v(1917.63, 686.41) * mm});
            skLineSegment(sketch, "E1374", {"start": v(1917.63, 686.41) * mm, "end": v(1857.15, 686.41) * mm});
            skLineSegment(sketch, "E1375", {"start": v(3066.82, -987.53) * mm, "end": v(3241.56, -987.53) * mm});
            skLineSegment(sketch, "E1376", {"start": v(3241.56, -987.53) * mm, "end": v(3241.56, -670.55) * mm});
            skLineSegment(sketch, "E1377", {"start": v(3241.56, -670.55) * mm, "end": v(3066.82, -670.55) * mm});
            skLineSegment(sketch, "E1378", {"start": v(3066.82, -670.55) * mm, "end": v(3066.82, -987.53) * mm});
            skLineSegment(sketch, "E1379", {"start": v(3084.75, -780.32) * mm, "end": v(3145.23, -780.32) * mm});
            skLineSegment(sketch, "E1380", {"start": v(3145.23, -780.32) * mm, "end": v(3145.23, -969.6) * mm});
            skLineSegment(sketch, "E1381", {"start": v(3145.23, -969.6) * mm, "end": v(3084.75, -969.6) * mm});
            skLineSegment(sketch, "E1382", {"start": v(3084.75, -969.6) * mm, "end": v(3084.75, -780.32) * mm});
            skLineSegment(sketch, "E1383", {"start": v(3163.15, -969.6) * mm, "end": v(3163.15, -780.32) * mm});
            skLineSegment(sketch, "E1384", {"start": v(3163.15, -780.32) * mm, "end": v(3223.63, -780.32) * mm});
            skLineSegment(sketch, "E1385", {"start": v(3223.63, -780.32) * mm, "end": v(3223.63, -969.6) * mm});
            skLineSegment(sketch, "E1386", {"start": v(3223.63, -969.6) * mm, "end": v(3163.15, -969.6) * mm});
            skLineSegment(sketch, "E1387", {"start": v(3223.63, -762.4) * mm, "end": v(3163.15, -762.4) * mm});
            skLineSegment(sketch, "E1388", {"start": v(3163.15, -762.4) * mm, "end": v(3163.15, -688.47) * mm});
            skLineSegment(sketch, "E1389", {"start": v(3163.15, -688.47) * mm, "end": v(3223.63, -688.47) * mm});
            skLineSegment(sketch, "E1390", {"start": v(3223.63, -688.47) * mm, "end": v(3223.63, -762.4) * mm});
            skLineSegment(sketch, "E1391", {"start": v(3145.23, -688.47) * mm, "end": v(3145.23, -762.4) * mm});
            skLineSegment(sketch, "E1392", {"start": v(3145.23, -762.4) * mm, "end": v(3084.75, -762.4) * mm});
            skLineSegment(sketch, "E1393", {"start": v(3084.75, -762.4) * mm, "end": v(3084.75, -688.47) * mm});
            skLineSegment(sketch, "E1394", {"start": v(3084.75, -688.47) * mm, "end": v(3145.23, -688.47) * mm});
            skLineSegment(sketch, "E1395", {"start": v(2189.81, -987.53) * mm, "end": v(2364.54, -987.53) * mm});
            skLineSegment(sketch, "E1396", {"start": v(2364.54, -987.53) * mm, "end": v(2364.54, -670.55) * mm});
            skLineSegment(sketch, "E1397", {"start": v(2364.54, -670.55) * mm, "end": v(2189.81, -670.55) * mm});
            skLineSegment(sketch, "E1398", {"start": v(2189.81, -670.55) * mm, "end": v(2189.81, -987.53) * mm});
            skLineSegment(sketch, "E1399", {"start": v(2207.73, -780.32) * mm, "end": v(2268.21, -780.32) * mm});
            skLineSegment(sketch, "E1400", {"start": v(2268.21, -780.32) * mm, "end": v(2268.21, -969.6) * mm});
            skLineSegment(sketch, "E1401", {"start": v(2268.21, -969.6) * mm, "end": v(2207.73, -969.6) * mm});
            skLineSegment(sketch, "E1402", {"start": v(2207.73, -969.6) * mm, "end": v(2207.73, -780.32) * mm});
            skLineSegment(sketch, "E1403", {"start": v(2286.14, -969.6) * mm, "end": v(2286.14, -780.32) * mm});
            skLineSegment(sketch, "E1404", {"start": v(2286.14, -780.32) * mm, "end": v(2346.62, -780.32) * mm});
            skLineSegment(sketch, "E1405", {"start": v(2346.62, -780.32) * mm, "end": v(2346.62, -969.6) * mm});
            skLineSegment(sketch, "E1406", {"start": v(2346.62, -969.6) * mm, "end": v(2286.14, -969.6) * mm});
            skLineSegment(sketch, "E1407", {"start": v(2346.62, -762.4) * mm, "end": v(2286.14, -762.4) * mm});
            skLineSegment(sketch, "E1408", {"start": v(2286.14, -762.4) * mm, "end": v(2286.14, -688.47) * mm});
            skLineSegment(sketch, "E1409", {"start": v(2286.14, -688.47) * mm, "end": v(2346.62, -688.47) * mm});
            skLineSegment(sketch, "E1410", {"start": v(2346.62, -688.47) * mm, "end": v(2346.62, -762.4) * mm});
            skLineSegment(sketch, "E1411", {"start": v(2268.21, -688.47) * mm, "end": v(2268.21, -762.4) * mm});
            skLineSegment(sketch, "E1412", {"start": v(2268.21, -762.4) * mm, "end": v(2207.73, -762.4) * mm});
            skLineSegment(sketch, "E1413", {"start": v(2207.73, -762.4) * mm, "end": v(2207.73, -688.47) * mm});
            skLineSegment(sketch, "E1414", {"start": v(2207.73, -688.47) * mm, "end": v(2268.21, -688.47) * mm});
            skLineSegment(sketch, "E1415", {"start": v(1760.82, -987.53) * mm, "end": v(1935.55, -987.53) * mm});
            skLineSegment(sketch, "E1416", {"start": v(1935.55, -987.53) * mm, "end": v(1935.55, -670.55) * mm});
            skLineSegment(sketch, "E1417", {"start": v(1935.55, -670.55) * mm, "end": v(1760.82, -670.55) * mm});
            skLineSegment(sketch, "E1418", {"start": v(1760.82, -670.55) * mm, "end": v(1760.82, -987.53) * mm});
            skLineSegment(sketch, "E1419", {"start": v(1778.74, -780.32) * mm, "end": v(1839.23, -780.32) * mm});
            skLineSegment(sketch, "E1420", {"start": v(1839.23, -780.32) * mm, "end": v(1839.23, -969.6) * mm});
            skLineSegment(sketch, "E1421", {"start": v(1839.23, -969.6) * mm, "end": v(1778.74, -969.6) * mm});
            skLineSegment(sketch, "E1422", {"start": v(1778.74, -969.6) * mm, "end": v(1778.74, -780.32) * mm});
            skLineSegment(sketch, "E1423", {"start": v(1857.15, -969.6) * mm, "end": v(1857.15, -780.32) * mm});
            skLineSegment(sketch, "E1424", {"start": v(1857.15, -780.32) * mm, "end": v(1917.63, -780.32) * mm});
            skLineSegment(sketch, "E1425", {"start": v(1917.63, -780.32) * mm, "end": v(1917.63, -969.6) * mm});
            skLineSegment(sketch, "E1426", {"start": v(1917.63, -969.6) * mm, "end": v(1857.15, -969.6) * mm});
            skLineSegment(sketch, "E1427", {"start": v(1917.63, -762.4) * mm, "end": v(1857.15, -762.4) * mm});
            skLineSegment(sketch, "E1428", {"start": v(1857.15, -762.4) * mm, "end": v(1857.15, -688.47) * mm});
            skLineSegment(sketch, "E1429", {"start": v(1857.15, -688.47) * mm, "end": v(1917.63, -688.47) * mm});
            skLineSegment(sketch, "E1430", {"start": v(1917.63, -688.47) * mm, "end": v(1917.63, -762.4) * mm});
            skLineSegment(sketch, "E1431", {"start": v(1839.23, -688.47) * mm, "end": v(1839.23, -762.4) * mm});
            skLineSegment(sketch, "E1432", {"start": v(1839.23, -762.4) * mm, "end": v(1778.74, -762.4) * mm});
            skLineSegment(sketch, "E1433", {"start": v(1778.74, -762.4) * mm, "end": v(1778.74, -688.47) * mm});
            skLineSegment(sketch, "E1434", {"start": v(1778.74, -688.47) * mm, "end": v(1839.23, -688.47) * mm});
            skLineSegment(sketch, "E1435", {"start": v(1500.97, -987.53) * mm, "end": v(1675.7, -987.53) * mm});
            skLineSegment(sketch, "E1436", {"start": v(1675.7, -987.53) * mm, "end": v(1675.7, -670.55) * mm});
            skLineSegment(sketch, "E1437", {"start": v(1675.7, -670.55) * mm, "end": v(1500.97, -670.55) * mm});
            skLineSegment(sketch, "E1438", {"start": v(1500.97, -670.55) * mm, "end": v(1500.97, -987.53) * mm});
            skLineSegment(sketch, "E1439", {"start": v(1518.89, -780.32) * mm, "end": v(1579.37, -780.32) * mm});
            skLineSegment(sketch, "E1440", {"start": v(1579.37, -780.32) * mm, "end": v(1579.37, -969.6) * mm});
            skLineSegment(sketch, "E1441", {"start": v(1579.37, -969.6) * mm, "end": v(1518.89, -969.6) * mm});
            skLineSegment(sketch, "E1442", {"start": v(1518.89, -969.6) * mm, "end": v(1518.89, -780.32) * mm});
            skLineSegment(sketch, "E1443", {"start": v(1597.3, -969.6) * mm, "end": v(1597.3, -780.32) * mm});
            skLineSegment(sketch, "E1444", {"start": v(1597.3, -780.32) * mm, "end": v(1657.78, -780.32) * mm});
            skLineSegment(sketch, "E1445", {"start": v(1657.78, -780.32) * mm, "end": v(1657.78, -969.6) * mm});
            skLineSegment(sketch, "E1446", {"start": v(1657.78, -969.6) * mm, "end": v(1597.3, -969.6) * mm});
            skLineSegment(sketch, "E1447", {"start": v(1657.78, -762.4) * mm, "end": v(1597.3, -762.4) * mm});
            skLineSegment(sketch, "E1448", {"start": v(1597.3, -762.4) * mm, "end": v(1597.3, -688.47) * mm});
            skLineSegment(sketch, "E1449", {"start": v(1597.3, -688.47) * mm, "end": v(1657.78, -688.47) * mm});
            skLineSegment(sketch, "E1450", {"start": v(1657.78, -688.47) * mm, "end": v(1657.78, -762.4) * mm});
            skLineSegment(sketch, "E1451", {"start": v(1579.37, -688.47) * mm, "end": v(1579.37, -762.4) * mm});
            skLineSegment(sketch, "E1452", {"start": v(1579.37, -762.4) * mm, "end": v(1518.89, -762.4) * mm});
            skLineSegment(sketch, "E1453", {"start": v(1518.89, -762.4) * mm, "end": v(1518.89, -688.47) * mm});
            skLineSegment(sketch, "E1454", {"start": v(1518.89, -688.47) * mm, "end": v(1579.37, -688.47) * mm});
            skLineSegment(sketch, "E1455", {"start": v(2926.82, 988.27) * mm, "end": v(2823.77, 988.27) * mm});
            skLineSegment(sketch, "E1456", {"start": v(2823.77, 988.27) * mm, "end": v(2823.77, 669.8) * mm});
            skLineSegment(sketch, "E1457", {"start": v(2823.77, 669.8) * mm, "end": v(2926.82, 669.8) * mm});
            skLineSegment(sketch, "E1458", {"start": v(2926.82, 669.8) * mm, "end": v(2926.82, 988.27) * mm});
            skLineSegment(sketch, "E1459", {"start": v(2908.9, 970.35) * mm, "end": v(2908.9, 896.43) * mm});
            skLineSegment(sketch, "E1460", {"start": v(2908.9, 896.43) * mm, "end": v(2841.7, 896.43) * mm});
            skLineSegment(sketch, "E1461", {"start": v(2841.7, 896.43) * mm, "end": v(2841.7, 970.35) * mm});
            skLineSegment(sketch, "E1462", {"start": v(2841.7, 970.35) * mm, "end": v(2908.9, 970.35) * mm});
            skLineSegment(sketch, "E1463", {"start": v(2841.7, 687.72) * mm, "end": v(2841.7, 878.5) * mm});
            skLineSegment(sketch, "E1464", {"start": v(2841.7, 878.5) * mm, "end": v(2908.9, 878.5) * mm});
            skLineSegment(sketch, "E1465", {"start": v(2908.9, 878.5) * mm, "end": v(2908.9, 687.72) * mm});
            skLineSegment(sketch, "E1466", {"start": v(2908.9, 687.72) * mm, "end": v(2841.7, 687.72) * mm});
            skLineSegment(sketch, "E1467", {"start": v(2608.72, 988.27) * mm, "end": v(2505.67, 988.27) * mm});
            skLineSegment(sketch, "E1468", {"start": v(2505.67, 988.27) * mm, "end": v(2505.67, 669.8) * mm});
            skLineSegment(sketch, "E1469", {"start": v(2505.67, 669.8) * mm, "end": v(2608.72, 669.8) * mm});
            skLineSegment(sketch, "E1470", {"start": v(2608.72, 669.8) * mm, "end": v(2608.72, 988.27) * mm});
            skLineSegment(sketch, "E1471", {"start": v(2590.8, 970.35) * mm, "end": v(2590.8, 896.43) * mm});
            skLineSegment(sketch, "E1472", {"start": v(2590.8, 896.43) * mm, "end": v(2523.6, 896.43) * mm});
            skLineSegment(sketch, "E1473", {"start": v(2523.6, 896.43) * mm, "end": v(2523.6, 970.35) * mm});
            skLineSegment(sketch, "E1474", {"start": v(2523.6, 970.35) * mm, "end": v(2590.8, 970.35) * mm});
            skLineSegment(sketch, "E1475", {"start": v(2523.6, 687.72) * mm, "end": v(2523.6, 878.5) * mm});
            skLineSegment(sketch, "E1476", {"start": v(2523.6, 878.5) * mm, "end": v(2590.8, 878.5) * mm});
            skLineSegment(sketch, "E1477", {"start": v(2590.8, 878.5) * mm, "end": v(2590.8, 687.72) * mm});
            skLineSegment(sketch, "E1478", {"start": v(2590.8, 687.72) * mm, "end": v(2523.6, 687.72) * mm});
            skLineSegment(sketch, "E1479", {"start": v(2803.05, -435.7) * mm, "end": v(2803.05, -118.72) * mm});
            skLineSegment(sketch, "E1480", {"start": v(2803.05, -118.72) * mm, "end": v(2628.32, -118.72) * mm});
            skLineSegment(sketch, "E1481", {"start": v(2628.32, -118.72) * mm, "end": v(2628.32, -435.7) * mm});
            skLineSegment(sketch, "E1482", {"start": v(2628.32, -435.7) * mm, "end": v(2803.05, -435.7) * mm});
            skLineSegment(sketch, "E1483", {"start": v(2646.24, -228.49) * mm, "end": v(2706.72, -228.49) * mm});
            skLineSegment(sketch, "E1484", {"start": v(2706.72, -228.49) * mm, "end": v(2706.72, -417.78) * mm});
            skLineSegment(sketch, "E1485", {"start": v(2706.72, -417.78) * mm, "end": v(2646.24, -417.78) * mm});
            skLineSegment(sketch, "E1486", {"start": v(2646.24, -417.78) * mm, "end": v(2646.24, -228.49) * mm});
            skLineSegment(sketch, "E1487", {"start": v(2724.64, -417.78) * mm, "end": v(2724.64, -228.49) * mm});
            skLineSegment(sketch, "E1488", {"start": v(2724.64, -228.49) * mm, "end": v(2785.13, -228.49) * mm});
            skLineSegment(sketch, "E1489", {"start": v(2785.13, -228.49) * mm, "end": v(2785.13, -417.78) * mm});
            skLineSegment(sketch, "E1490", {"start": v(2785.13, -417.78) * mm, "end": v(2724.64, -417.78) * mm});
            skLineSegment(sketch, "E1491", {"start": v(2785.13, -136.64) * mm, "end": v(2785.13, -210.57) * mm});
            skLineSegment(sketch, "E1492", {"start": v(2785.13, -210.57) * mm, "end": v(2646.24, -210.57) * mm});
            skLineSegment(sketch, "E1493", {"start": v(2646.24, -210.57) * mm, "end": v(2646.24, -136.64) * mm});
            skLineSegment(sketch, "E1494", {"start": v(2646.24, -136.64) * mm, "end": v(2785.13, -136.64) * mm});
            skLineSegment(sketch, "E1495", {"start": v(2926.26, -437.2) * mm, "end": v(2926.26, -118.72) * mm});
            skLineSegment(sketch, "E1496", {"start": v(2926.26, -118.72) * mm, "end": v(2823.2, -118.72) * mm});
            skLineSegment(sketch, "E1497", {"start": v(2823.2, -118.72) * mm, "end": v(2823.2, -437.2) * mm});
            skLineSegment(sketch, "E1498", {"start": v(2823.2, -437.2) * mm, "end": v(2926.26, -437.2) * mm});
            skLineSegment(sketch, "E1499", {"start": v(2841.13, -419.28) * mm, "end": v(2841.13, -228.49) * mm});
            skLineSegment(sketch, "E1500", {"start": v(2841.13, -228.49) * mm, "end": v(2908.33, -228.49) * mm});
            skLineSegment(sketch, "E1501", {"start": v(2908.33, -228.49) * mm, "end": v(2908.33, -419.28) * mm});
            skLineSegment(sketch, "E1502", {"start": v(2908.33, -419.28) * mm, "end": v(2841.13, -419.28) * mm});
            skLineSegment(sketch, "E1503", {"start": v(2908.33, -136.64) * mm, "end": v(2908.33, -210.57) * mm});
            skLineSegment(sketch, "E1504", {"start": v(2908.33, -210.57) * mm, "end": v(2841.13, -210.57) * mm});
            skLineSegment(sketch, "E1505", {"start": v(2841.13, -210.57) * mm, "end": v(2841.13, -136.64) * mm});
            skLineSegment(sketch, "E1506", {"start": v(2841.13, -136.64) * mm, "end": v(2908.33, -136.64) * mm});
            skLineSegment(sketch, "E1507", {"start": v(2608.16, -437.2) * mm, "end": v(2608.16, -118.72) * mm});
            skLineSegment(sketch, "E1508", {"start": v(2608.16, -118.72) * mm, "end": v(2505.1, -118.72) * mm});
            skLineSegment(sketch, "E1509", {"start": v(2505.1, -118.72) * mm, "end": v(2505.1, -437.2) * mm});
            skLineSegment(sketch, "E1510", {"start": v(2505.1, -437.2) * mm, "end": v(2608.16, -437.2) * mm});
            skLineSegment(sketch, "E1511", {"start": v(2523.03, -419.28) * mm, "end": v(2523.03, -228.49) * mm});
            skLineSegment(sketch, "E1512", {"start": v(2523.03, -228.49) * mm, "end": v(2590.23, -228.49) * mm});
            skLineSegment(sketch, "E1513", {"start": v(2590.23, -228.49) * mm, "end": v(2590.23, -419.28) * mm});
            skLineSegment(sketch, "E1514", {"start": v(2590.23, -419.28) * mm, "end": v(2523.03, -419.28) * mm});
            skLineSegment(sketch, "E1515", {"start": v(2590.23, -136.64) * mm, "end": v(2590.23, -210.57) * mm});
            skLineSegment(sketch, "E1516", {"start": v(2590.23, -210.57) * mm, "end": v(2523.03, -210.57) * mm});
            skLineSegment(sketch, "E1517", {"start": v(2523.03, -210.57) * mm, "end": v(2523.03, -136.64) * mm});
            skLineSegment(sketch, "E1518", {"start": v(2523.03, -136.64) * mm, "end": v(2590.23, -136.64) * mm});
            skLineSegment(sketch, "E1519", {"start": v(2628.88, -986.78) * mm, "end": v(2803.6, -986.78) * mm});
            skLineSegment(sketch, "E1520", {"start": v(2803.6, -986.78) * mm, "end": v(2803.6, -669.8) * mm});
            skLineSegment(sketch, "E1521", {"start": v(2803.6, -669.8) * mm, "end": v(2628.88, -669.8) * mm});
            skLineSegment(sketch, "E1522", {"start": v(2628.88, -669.8) * mm, "end": v(2628.88, -986.78) * mm});
            skLineSegment(sketch, "E1523", {"start": v(2646.8, -779.56) * mm, "end": v(2707.28, -779.56) * mm});
            skLineSegment(sketch, "E1524", {"start": v(2707.28, -779.56) * mm, "end": v(2707.28, -968.86) * mm});
            skLineSegment(sketch, "E1525", {"start": v(2707.28, -968.86) * mm, "end": v(2646.8, -968.86) * mm});
            skLineSegment(sketch, "E1526", {"start": v(2646.8, -968.86) * mm, "end": v(2646.8, -779.56) * mm});
            skLineSegment(sketch, "E1527", {"start": v(2725.2, -968.86) * mm, "end": v(2725.2, -779.56) * mm});
            skLineSegment(sketch, "E1528", {"start": v(2725.2, -779.56) * mm, "end": v(2785.69, -779.56) * mm});
            skLineSegment(sketch, "E1529", {"start": v(2785.69, -779.56) * mm, "end": v(2785.69, -968.86) * mm});
            skLineSegment(sketch, "E1530", {"start": v(2785.69, -968.86) * mm, "end": v(2725.2, -968.86) * mm});
            skLineSegment(sketch, "E1531", {"start": v(2785.69, -687.72) * mm, "end": v(2785.69, -761.64) * mm});
            skLineSegment(sketch, "E1532", {"start": v(2785.69, -761.64) * mm, "end": v(2646.8, -761.64) * mm});
            skLineSegment(sketch, "E1533", {"start": v(2646.8, -761.64) * mm, "end": v(2646.8, -687.72) * mm});
            skLineSegment(sketch, "E1534", {"start": v(2646.8, -687.72) * mm, "end": v(2785.69, -687.72) * mm});
            skLineSegment(sketch, "E1535", {"start": v(2823.77, -988.27) * mm, "end": v(2926.82, -988.27) * mm});
            skLineSegment(sketch, "E1536", {"start": v(2926.82, -988.27) * mm, "end": v(2926.82, -669.8) * mm});
            skLineSegment(sketch, "E1537", {"start": v(2926.82, -669.8) * mm, "end": v(2823.77, -669.8) * mm});
            skLineSegment(sketch, "E1538", {"start": v(2823.77, -669.8) * mm, "end": v(2823.77, -988.27) * mm});
            skLineSegment(sketch, "E1539", {"start": v(2841.7, -970.35) * mm, "end": v(2841.7, -779.56) * mm});
            skLineSegment(sketch, "E1540", {"start": v(2841.7, -779.56) * mm, "end": v(2908.9, -779.56) * mm});
            skLineSegment(sketch, "E1541", {"start": v(2908.9, -779.56) * mm, "end": v(2908.9, -970.35) * mm});
            skLineSegment(sketch, "E1542", {"start": v(2908.9, -970.35) * mm, "end": v(2841.7, -970.35) * mm});
            skLineSegment(sketch, "E1543", {"start": v(2908.9, -687.72) * mm, "end": v(2908.9, -761.64) * mm});
            skLineSegment(sketch, "E1544", {"start": v(2908.9, -761.64) * mm, "end": v(2841.7, -761.64) * mm});
            skLineSegment(sketch, "E1545", {"start": v(2841.7, -761.64) * mm, "end": v(2841.7, -687.72) * mm});
            skLineSegment(sketch, "E1546", {"start": v(2841.7, -687.72) * mm, "end": v(2908.9, -687.72) * mm});
            skLineSegment(sketch, "E1547", {"start": v(2505.67, -988.27) * mm, "end": v(2608.72, -988.27) * mm});
            skLineSegment(sketch, "E1548", {"start": v(2608.72, -988.27) * mm, "end": v(2608.72, -669.8) * mm});
            skLineSegment(sketch, "E1549", {"start": v(2608.72, -669.8) * mm, "end": v(2505.67, -669.8) * mm});
            skLineSegment(sketch, "E1550", {"start": v(2505.67, -669.8) * mm, "end": v(2505.67, -988.27) * mm});
            skLineSegment(sketch, "E1551", {"start": v(2523.6, -970.35) * mm, "end": v(2523.6, -779.56) * mm});
            skLineSegment(sketch, "E1552", {"start": v(2523.6, -779.56) * mm, "end": v(2590.8, -779.56) * mm});
            skLineSegment(sketch, "E1553", {"start": v(2590.8, -779.56) * mm, "end": v(2590.8, -970.35) * mm});
            skLineSegment(sketch, "E1554", {"start": v(2590.8, -970.35) * mm, "end": v(2523.6, -970.35) * mm});
            skLineSegment(sketch, "E1555", {"start": v(2590.8, -687.72) * mm, "end": v(2590.8, -761.64) * mm});
            skLineSegment(sketch, "E1556", {"start": v(2590.8, -761.64) * mm, "end": v(2523.6, -761.64) * mm});
            skLineSegment(sketch, "E1557", {"start": v(2523.6, -761.64) * mm, "end": v(2523.6, -687.72) * mm});
            skLineSegment(sketch, "E1558", {"start": v(2523.6, -687.72) * mm, "end": v(2590.8, -687.72) * mm});
            skLineSegment(sketch, "E1559", {"start": v(2023.48, 142.3) * mm, "end": v(2101.88, 142.3) * mm});
            skLineSegment(sketch, "E1560", {"start": v(2101.88, 142.3) * mm, "end": v(2101.88, 433.84) * mm});
            skLineSegment(sketch, "E1561", {"start": v(2101.88, 433.84) * mm, "end": v(1927.15, 433.84) * mm});
            skLineSegment(sketch, "E1562", {"start": v(1927.15, 433.84) * mm, "end": v(1927.15, 142.3) * mm});
            skLineSegment(sketch, "E1563", {"start": v(1927.15, 142.3) * mm, "end": v(2005.56, 142.3) * mm});
            skLineSegment(sketch, "E1564", {"start": v(2005.56, 142.3) * mm, "end": v(2023.48, 142.3) * mm});
            skLineSegment(sketch, "E1565", {"start": v(2023.48, 416.69) * mm, "end": v(2083.96, 416.69) * mm});
            skLineSegment(sketch, "E1566", {"start": v(2083.96, 416.69) * mm, "end": v(2083.96, 345.95) * mm});
            skLineSegment(sketch, "E1567", {"start": v(2083.96, 345.95) * mm, "end": v(2023.48, 345.95) * mm});
            skLineSegment(sketch, "E1568", {"start": v(2023.48, 345.95) * mm, "end": v(2023.48, 416.69) * mm});
            skLineSegment(sketch, "E1569", {"start": v(2023.48, 328.8) * mm, "end": v(2083.96, 328.8) * mm});
            skLineSegment(sketch, "E1570", {"start": v(2083.96, 328.8) * mm, "end": v(2083.96, 159.45) * mm});
            skLineSegment(sketch, "E1571", {"start": v(2083.96, 159.45) * mm, "end": v(2023.48, 159.45) * mm});
            skLineSegment(sketch, "E1572", {"start": v(2023.48, 159.45) * mm, "end": v(2023.48, 328.8) * mm});
            skLineSegment(sketch, "E1573", {"start": v(1945.07, 416.69) * mm, "end": v(2005.56, 416.69) * mm});
            skLineSegment(sketch, "E1574", {"start": v(2005.56, 416.69) * mm, "end": v(2005.56, 345.95) * mm});
            skLineSegment(sketch, "E1575", {"start": v(2005.56, 345.95) * mm, "end": v(1945.07, 345.95) * mm});
            skLineSegment(sketch, "E1576", {"start": v(1945.07, 345.95) * mm, "end": v(1945.07, 416.69) * mm});
            skLineSegment(sketch, "E1577", {"start": v(1945.07, 328.8) * mm, "end": v(2005.56, 328.8) * mm});
            skLineSegment(sketch, "E1578", {"start": v(2005.56, 328.8) * mm, "end": v(2005.56, 159.45) * mm});
            skLineSegment(sketch, "E1579", {"start": v(2005.56, 159.45) * mm, "end": v(1945.07, 159.45) * mm});
            skLineSegment(sketch, "E1580", {"start": v(1945.07, 159.45) * mm, "end": v(1945.07, 328.8) * mm});
            skLineSegment(sketch, "E1581", {"start": v(2225.1, 433.84) * mm, "end": v(2122.05, 433.84) * mm});
            skLineSegment(sketch, "E1582", {"start": v(2122.05, 433.84) * mm, "end": v(2122.05, 142.3) * mm});
            skLineSegment(sketch, "E1583", {"start": v(2122.05, 142.3) * mm, "end": v(2225.1, 142.3) * mm});
            skLineSegment(sketch, "E1584", {"start": v(2225.1, 142.3) * mm, "end": v(2225.1, 433.84) * mm});
            skLineSegment(sketch, "E1585", {"start": v(2207.17, 416.69) * mm, "end": v(2207.17, 347.6) * mm});
            skLineSegment(sketch, "E1586", {"start": v(2207.17, 347.6) * mm, "end": v(2139.97, 347.6) * mm});
            skLineSegment(sketch, "E1587", {"start": v(2139.97, 347.6) * mm, "end": v(2139.97, 416.69) * mm});
            skLineSegment(sketch, "E1588", {"start": v(2139.97, 416.69) * mm, "end": v(2207.17, 416.69) * mm});
            skLineSegment(sketch, "E1589", {"start": v(2139.97, 159.45) * mm, "end": v(2139.97, 329.67) * mm});
            skLineSegment(sketch, "E1590", {"start": v(2139.97, 329.67) * mm, "end": v(2207.17, 329.67) * mm});
            skLineSegment(sketch, "E1591", {"start": v(2207.17, 329.67) * mm, "end": v(2207.17, 159.45) * mm});
            skLineSegment(sketch, "E1592", {"start": v(2207.17, 159.45) * mm, "end": v(2139.97, 159.45) * mm});
            skLineSegment(sketch, "E1593", {"start": v(1803.95, 433.84) * mm, "end": v(1803.95, 142.3) * mm});
            skLineSegment(sketch, "E1594", {"start": v(1803.95, 142.3) * mm, "end": v(1907, 142.3) * mm});
            skLineSegment(sketch, "E1595", {"start": v(1907, 142.3) * mm, "end": v(1907, 433.84) * mm});
            skLineSegment(sketch, "E1596", {"start": v(1907, 433.84) * mm, "end": v(1803.95, 433.84) * mm});
            skLineSegment(sketch, "E1597", {"start": v(1889.07, 159.45) * mm, "end": v(1821.87, 159.45) * mm});
            skLineSegment(sketch, "E1598", {"start": v(1821.87, 159.45) * mm, "end": v(1821.87, 334.16) * mm});
            skLineSegment(sketch, "E1599", {"start": v(1821.87, 334.16) * mm, "end": v(1889.07, 334.16) * mm});
            skLineSegment(sketch, "E1600", {"start": v(1889.07, 334.16) * mm, "end": v(1889.07, 159.45) * mm});
            skLineSegment(sketch, "E1601", {"start": v(1889.07, 351.3) * mm, "end": v(1821.87, 351.3) * mm});
            skLineSegment(sketch, "E1602", {"start": v(1821.87, 351.3) * mm, "end": v(1821.87, 416.69) * mm});
            skLineSegment(sketch, "E1603", {"start": v(1821.87, 416.69) * mm, "end": v(1889.07, 416.69) * mm});
            skLineSegment(sketch, "E1604", {"start": v(1889.07, 416.69) * mm, "end": v(1889.07, 351.3) * mm});
            skLineSegment(sketch, "E1605", {"start": v(-87.71, 142.3) * mm, "end": v(-9.3, 142.3) * mm});
            skLineSegment(sketch, "E1606", {"start": v(-9.3, 142.3) * mm, "end": v(8.61, 142.3) * mm});
            skLineSegment(sketch, "E1607", {"start": v(8.61, 142.3) * mm, "end": v(87.02, 142.3) * mm});
            skLineSegment(sketch, "E1608", {"start": v(87.02, 142.3) * mm, "end": v(87.02, 433.84) * mm});
            skLineSegment(sketch, "E1609", {"start": v(87.02, 433.84) * mm, "end": v(-87.71, 433.84) * mm});
            skLineSegment(sketch, "E1610", {"start": v(-87.71, 433.84) * mm, "end": v(-87.71, 142.3) * mm});
            skLineSegment(sketch, "E1611", {"start": v(8.61, 416.69) * mm, "end": v(69.1, 416.69) * mm});
            skLineSegment(sketch, "E1612", {"start": v(69.1, 416.69) * mm, "end": v(69.1, 345.95) * mm});
            skLineSegment(sketch, "E1613", {"start": v(69.1, 345.95) * mm, "end": v(8.61, 345.95) * mm});
            skLineSegment(sketch, "E1614", {"start": v(8.61, 345.95) * mm, "end": v(8.61, 416.69) * mm});
            skLineSegment(sketch, "E1615", {"start": v(8.61, 328.8) * mm, "end": v(69.1, 328.8) * mm});
            skLineSegment(sketch, "E1616", {"start": v(69.1, 328.8) * mm, "end": v(69.1, 159.45) * mm});
            skLineSegment(sketch, "E1617", {"start": v(69.1, 159.45) * mm, "end": v(8.61, 159.45) * mm});
            skLineSegment(sketch, "E1618", {"start": v(8.61, 159.45) * mm, "end": v(8.61, 328.8) * mm});
            skLineSegment(sketch, "E1619", {"start": v(-69.79, 416.69) * mm, "end": v(-9.3, 416.69) * mm});
            skLineSegment(sketch, "E1620", {"start": v(-9.3, 416.69) * mm, "end": v(-9.3, 345.95) * mm});
            skLineSegment(sketch, "E1621", {"start": v(-9.3, 345.95) * mm, "end": v(-69.79, 345.95) * mm});
            skLineSegment(sketch, "E1622", {"start": v(-69.79, 345.95) * mm, "end": v(-69.79, 416.69) * mm});
            skLineSegment(sketch, "E1623", {"start": v(-69.79, 328.8) * mm, "end": v(-9.3, 328.8) * mm});
            skLineSegment(sketch, "E1624", {"start": v(-9.3, 328.8) * mm, "end": v(-9.3, 159.45) * mm});
            skLineSegment(sketch, "E1625", {"start": v(-9.3, 159.45) * mm, "end": v(-69.79, 159.45) * mm});
            skLineSegment(sketch, "E1626", {"start": v(-69.79, 159.45) * mm, "end": v(-69.79, 328.8) * mm});
            skLineSegment(sketch, "E1627", {"start": v(-210.92, 142.3) * mm, "end": v(-107.87, 142.3) * mm});
            skLineSegment(sketch, "E1628", {"start": v(-107.87, 142.3) * mm, "end": v(-107.87, 433.84) * mm});
            skLineSegment(sketch, "E1629", {"start": v(-107.87, 433.84) * mm, "end": v(-210.92, 433.84) * mm});
            skLineSegment(sketch, "E1630", {"start": v(-210.92, 433.84) * mm, "end": v(-210.92, 142.3) * mm});
            skLineSegment(sketch, "E1631", {"start": v(-193, 159.45) * mm, "end": v(-193, 329.67) * mm});
            skLineSegment(sketch, "E1632", {"start": v(-193, 329.67) * mm, "end": v(-125.8, 329.67) * mm});
            skLineSegment(sketch, "E1633", {"start": v(-125.8, 329.67) * mm, "end": v(-125.8, 159.45) * mm});
            skLineSegment(sketch, "E1634", {"start": v(-125.8, 159.45) * mm, "end": v(-193, 159.45) * mm});
            skLineSegment(sketch, "E1635", {"start": v(-125.8, 416.69) * mm, "end": v(-125.8, 347.6) * mm});
            skLineSegment(sketch, "E1636", {"start": v(-125.8, 347.6) * mm, "end": v(-193, 347.6) * mm});
            skLineSegment(sketch, "E1637", {"start": v(-193, 347.6) * mm, "end": v(-193, 416.69) * mm});
            skLineSegment(sketch, "E1638", {"start": v(-193, 416.69) * mm, "end": v(-125.8, 416.69) * mm});
            skLineSegment(sketch, "E1639", {"start": v(107.18, 142.3) * mm, "end": v(210.23, 142.3) * mm});
            skLineSegment(sketch, "E1640", {"start": v(210.23, 142.3) * mm, "end": v(210.23, 433.84) * mm});
            skLineSegment(sketch, "E1641", {"start": v(210.23, 433.84) * mm, "end": v(107.18, 433.84) * mm});
            skLineSegment(sketch, "E1642", {"start": v(107.18, 433.84) * mm, "end": v(107.18, 142.3) * mm});
            skLineSegment(sketch, "E1643", {"start": v(125.1, 416.69) * mm, "end": v(192.3, 416.69) * mm});
            skLineSegment(sketch, "E1644", {"start": v(192.3, 416.69) * mm, "end": v(192.3, 351.3) * mm});
            skLineSegment(sketch, "E1645", {"start": v(192.3, 351.3) * mm, "end": v(125.1, 351.3) * mm});
            skLineSegment(sketch, "E1646", {"start": v(125.1, 351.3) * mm, "end": v(125.1, 416.69) * mm});
            skLineSegment(sketch, "E1647", {"start": v(125.1, 334.16) * mm, "end": v(192.3, 334.16) * mm});
            skLineSegment(sketch, "E1648", {"start": v(192.3, 334.16) * mm, "end": v(192.3, 159.45) * mm});
            skLineSegment(sketch, "E1649", {"start": v(192.3, 159.45) * mm, "end": v(125.1, 159.45) * mm});
            skLineSegment(sketch, "E1650", {"start": v(125.1, 159.45) * mm, "end": v(125.1, 334.16) * mm});
            skLineSegment(sketch, "E1651", {"start": v(3154.19, 70.18) * mm, "end": v(2255.21, 70.18) * mm});
            skLineSegment(sketch, "E1652", {"start": v(2255.21, 70.18) * mm, "end": v(2255.21, 17.17) * mm});
            skLineSegment(sketch, "E1653", {"start": v(2255.21, 17.17) * mm, "end": v(3154.19, 17.17) * mm});
            skLineSegment(sketch, "E1654", {"start": v(3154.19, 17.17) * mm, "end": v(3154.19, 70.18) * mm});
            skSolve(sketch);
        }
        {
            var Q0;
            Q0 = qSketchRegion(id + "F4", true);
            extrude(context, id + "F5", {"entities" : qUnion([Q0]), "depth" : 25 * mm, "offsetDistance" : 25 * mm});
        }
    });
